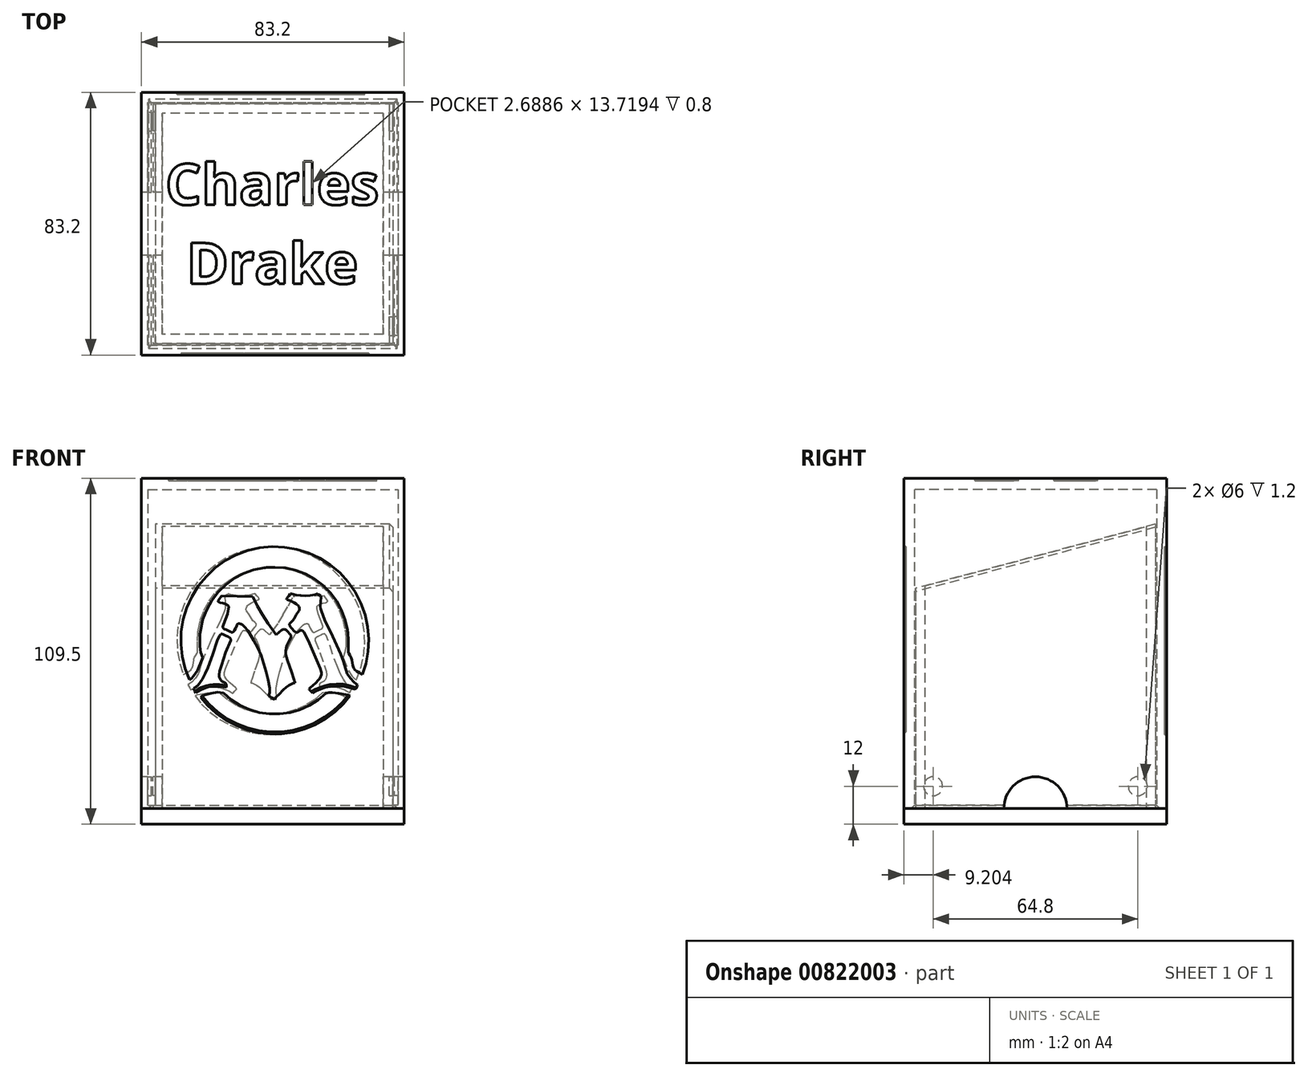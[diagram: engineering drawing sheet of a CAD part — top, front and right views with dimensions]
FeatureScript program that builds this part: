
annotation { "Feature Type Name" : "Feature", "Feature Type Description" : "" }
export const myFeature = defineFeature(function(context is Context, id is Id, definition is map)
    precondition{}
    {
        {
            var Q0;
            Q0=qCreatedBy(makeId("Top.planeOp"),FACE);
            var sketch = newSketch(context, id + "F0", { "sketchPlane" : qUnion([Q0])});
            skLineSegment(sketch, "E0.bottom", {"start": v(-37.57, 59.17) * mm, "end": v(32.43, 59.17) * mm});
            skLineSegment(sketch, "E0.top", {"start": v(-37.57, -10.83) * mm, "end": v(32.43, -10.83) * mm});
            skLineSegment(sketch, "E0.left", {"start": v(-37.57, 59.17) * mm, "end": v(-37.57, -10.83) * mm});
            skLineSegment(sketch, "E0.right", {"start": v(32.43, 59.17) * mm, "end": v(32.43, -10.83) * mm});
            skLineSegment(sketch, "E1.0", {"start": v(-40.57, 62.17) * mm, "end": v(35.43, 62.17) * mm});
            skLineSegment(sketch, "E1.1", {"start": v(-40.57, 62.17) * mm, "end": v(-40.57, -13.83) * mm});
            skLineSegment(sketch, "E1.2", {"start": v(-40.57, -13.83) * mm, "end": v(35.43, -13.83) * mm});
            skLineSegment(sketch, "E1.3", {"start": v(35.43, 62.17) * mm, "end": v(35.43, -13.83) * mm});
            skSolve(sketch);
        }
        {
            var Q0;
            Q0=makeQuery(id+"F0.imprint","IMPRINT",FACE,{"disambiguationData":[TD([[makeQuery(id+"F0.imprint","IMPRINT",EDGE,{"derivedFrom":sQuery(id+"F0.wireOp",EDGE,"E0.bottom")}),1.0]])]});
            extrude(context, id + "F1", {"entities" : qUnion([Q0]), "depth" : 101 * mm, "offsetDistance" : 25 * mm});
        }
        {
            var Q0;
            Q0=makeQuery(id+"F1.opExtrude","CAP_FACE",FACE,{"disambiguationData":[OSD([sQuery(id+"F0.wireOp",EDGE,"E0.bottom"),sQuery(id+"F0.wireOp",EDGE,"E0.top"),sQuery(id+"F0.wireOp",EDGE,"E0.left"),sQuery(id+"F0.wireOp",EDGE,"E0.right"),sQuery(id+"F0.wireOp",EDGE,"E1.0"),sQuery(id+"F0.wireOp",EDGE,"E1.1"),sQuery(id+"F0.wireOp",EDGE,"E1.2"),sQuery(id+"F0.wireOp",EDGE,"E1.3")])],"isStart":true});
            var sketch = newSketch(context, id + "F2", { "sketchPlane" : qUnion([Q0])});
            skLineSegment(sketch, "E2.0", {"start": v(-44.17, 17.43) * mm, "end": v(39.03, 17.43) * mm});
            skLineSegment(sketch, "E2.1", {"start": v(-44.17, -65.77) * mm, "end": v(-44.17, 17.43) * mm});
            skLineSegment(sketch, "E2.2", {"start": v(-44.17, -65.77) * mm, "end": v(39.03, -65.77) * mm});
            skLineSegment(sketch, "E2.3", {"start": v(39.03, -65.77) * mm, "end": v(39.03, 17.43) * mm});
            skSolve(sketch);
        }
        {
            var Q0;
            Q0=makeQuery(id+"F2.imprint","IMPRINT",FACE,{"disambiguationData":[TD([[makeQuery(id+"F2.imprint","IMPRINT",EDGE,{"derivedFrom":sQuery(id+"F2.wireOp",EDGE,"E2.0")}),-1.0]])]});
            var Q1;
            Q1=makeQuery(id+"F2.imprint","IMPRINT",FACE,{"disambiguationData":[TD([[makeQuery(id+"F2.imprint","IMPRINT",EDGE,{"derivedFrom":makeQuery(id+"F1.opExtrude","CAP_EDGE",EDGE,{"disambiguationData":[OSD([sQuery(id+"F0.wireOp",EDGE,"E0.bottom")])],"isStart":true})}),1.0]])]});
            var Q2;
            Q2=makeQuery(id+"F2.imprint","IMPRINT",FACE,{"disambiguationData":[TD([[makeQuery(id+"F2.imprint","IMPRINT",EDGE,{"derivedFrom":makeQuery(id+"F1.opExtrude","CAP_EDGE",EDGE,{"disambiguationData":[OSD([sQuery(id+"F0.wireOp",EDGE,"E0.bottom")])],"isStart":true})}),-1.0]])]});
            extrude(context, id + "F3", {"entities" : qUnion([Q0, Q1, Q2]), "operationType" : NewBodyOperationType.ADD, "depth" : 5 * mm, "offsetDistance" : 25 * mm});
        }
        {
            var Q0;
            Q0=makeQuery(id+"F1.opExtrude","SWEPT_FACE",FACE,{"disambiguationData":[OSD([sQuery(id+"F0.wireOp",EDGE,"E1.1")])]});
            var sketch = newSketch(context, id + "F4", { "sketchPlane" : qUnion([Q0])});
            skLineSegment(sketch, "E3", {"start": v(-62.17, 90) * mm, "end": v(13.83, 69.64) * mm});
            skSolve(sketch);
        }
        {
            var Q0;
            {var subQ0=sQuery(id+"F4.wireOp",EDGE,"E3");Q0=makeQuery(id+"F4.imprint","IMPRINT",FACE,{"disambiguationData":[TD([[makeQuery(id+"F4.imprint","IMPRINT",EDGE,{"derivedFrom":subQ0}),1.0]])]});}
            extrude(context, id + "F5", {"entities" : qUnion([Q0]), "operationType" : NewBodyOperationType.REMOVE, "endBound" : BoundingType.THROUGH_ALL, "oppositeDirection" : true, "depth" : 25 * mm, "offsetDistance" : 25 * mm});
        }
        {
            var Q0;
            {var subQ0=sQuery(id+"F2.wireOp",EDGE,"E2.3");var subQ1=sQuery(id+"F2.wireOp",EDGE,"E2.0");var subQ2=sQuery(id+"F2.wireOp",EDGE,"E2.1");var subQ3=sQuery(id+"F2.wireOp",EDGE,"E2.2");Q0=makeQuery(id+"F3.boolean.opBoolean","SPLIT",FACE,{"disambiguationData":[TD([makeQuery(id+"F1.opExtrude","SWEPT_FACE",FACE,{"disambiguationData":[OSD([sQuery(id+"F0.wireOp",EDGE,"E1.0")])]})])],"derivedFrom":makeQuery(id+"F3.opExtrude","CAP_FACE",FACE,{"disambiguationData":[OSD([subQ1,subQ2,subQ3,subQ0])],"isStart":true})});}
            var sketch = newSketch(context, id + "F6", { "sketchPlane" : qUnion([Q0])});
            skLineSegment(sketch, "E4.0", {"start": v(-44.17, 65.77) * mm, "end": v(-44.17, -17.43) * mm});
            skLineSegment(sketch, "E5.0", {"start": v(-44.17, -17.43) * mm, "end": v(39.03, -17.43) * mm});
            skLineSegment(sketch, "E6.0", {"start": v(39.03, 65.77) * mm, "end": v(39.03, -17.43) * mm});
            skLineSegment(sketch, "E7.0", {"start": v(-44.17, 65.77) * mm, "end": v(39.03, 65.77) * mm});
            skLineSegment(sketch, "E8.0", {"start": v(-40.97, 62.57) * mm, "end": v(35.83, 62.57) * mm});
            skLineSegment(sketch, "E8.1", {"start": v(-40.97, 62.57) * mm, "end": v(-40.97, -14.23) * mm});
            skLineSegment(sketch, "E8.2", {"start": v(-40.97, -14.23) * mm, "end": v(35.83, -14.23) * mm});
            skLineSegment(sketch, "E8.3", {"start": v(35.83, 62.57) * mm, "end": v(35.83, -14.23) * mm});
            skSolve(sketch);
        }
        {
            var Q0;
            Q0=makeQuery(id+"F6.imprint","IMPRINT",FACE,{"disambiguationData":[TD([[makeQuery(id+"F6.imprint","IMPRINT",EDGE,{"derivedFrom":sQuery(id+"F6.wireOp",EDGE,"E4.0")}),1.0]])]});
            extrude(context, id + "F7", {"entities" : qUnion([Q0]), "depth" : 101 * mm, "offsetDistance" : 25 * mm});
        }
        {
            var Q0;
            Q0=makeQuery(id+"F7.opExtrude","CAP_FACE",FACE,{"disambiguationData":[OSD([sQuery(id+"F6.wireOp",EDGE,"E4.0"),sQuery(id+"F6.wireOp",EDGE,"E5.0"),sQuery(id+"F6.wireOp",EDGE,"E6.0"),sQuery(id+"F6.wireOp",EDGE,"E7.0"),sQuery(id+"F6.wireOp",EDGE,"E8.0"),sQuery(id+"F6.wireOp",EDGE,"E8.1"),sQuery(id+"F6.wireOp",EDGE,"E8.2"),sQuery(id+"F6.wireOp",EDGE,"E8.3")])],"isStart":false});
            var sketch = newSketch(context, id + "F8", { "sketchPlane" : qUnion([Q0])});
            skSolve(sketch);
        }
        {
            var Q0;
            Q0=makeQuery(id+"F8.imprint","IMPRINT",FACE,{"disambiguationData":[TD([[makeQuery(id+"F8.imprint","IMPRINT",EDGE,{"derivedFrom":makeQuery(id+"F7.opExtrude","CAP_EDGE",EDGE,{"disambiguationData":[OSD([sQuery(id+"F6.wireOp",EDGE,"E4.0")])],"isStart":false})}),1.0]])]});
            var Q1;
            Q1=makeQuery(id+"F8.imprint","IMPRINT",FACE,{"disambiguationData":[TD([[makeQuery(id+"F8.imprint","IMPRINT",EDGE,{"derivedFrom":makeQuery(id+"F7.opExtrude","CAP_EDGE",EDGE,{"disambiguationData":[OSD([sQuery(id+"F6.wireOp",EDGE,"E8.0")])],"isStart":false})}),-1.0]])]});
            extrude(context, id + "F9", {"entities" : qUnion([Q0, Q1]), "operationType" : NewBodyOperationType.ADD, "depth" : 3.5 * mm, "offsetDistance" : 25 * mm});
        }
        {
            var Q0;
            Q0=makeQuery(id+"F9.opExtrude","CAP_FACE",FACE,{"disambiguationData":[OSD([sQuery(id+"F6.wireOp",EDGE,"E4.0"),sQuery(id+"F6.wireOp",EDGE,"E5.0"),sQuery(id+"F6.wireOp",EDGE,"E6.0"),sQuery(id+"F6.wireOp",EDGE,"E7.0")])],"isStart":false});
            var sketch = newSketch(context, id + "F10", { "sketchPlane" : qUnion([Q0])});
            skLineSegment(sketch, "E9", {"start": v(-2.57, 65.77) * mm, "end": v(-2.57, -17.43) * mm, "construction": true});
            skLineSegment(sketch, "E10", {"start": v(-44.17, 24.17) * mm, "end": v(39.03, 24.17) * mm, "construction": true});
            skText(sketch, "E11", { "text": "Charles", "fontName": "OpenSans-Bold.ttf"});
            skText(sketch, "E12", { "text": "Drake", "fontName": "OpenSans-Bold.ttf"});
            const initialGuessF10  = {"E11": [-0.03662, 0.03017, 1, 0, 0.013], "E12": [-0.02993, 0.00517, 1, 0, 0.013]};
            skSetInitialGuess(sketch, initialGuessF10);
            skSolve(sketch);
        }
        {
            var Q0;
            Q0 = qSketchRegion(id + "F10", true);
            extrude(context, id + "F11", {"entities" : qUnion([Q0]), "operationType" : NewBodyOperationType.REMOVE, "oppositeDirection" : true, "depth" : 0.8 * mm, "offsetDistance" : 25 * mm});
        }
        {
            var Q0;
            {var subQ0=sQuery(id+"F6.wireOp",EDGE,"E5.0");Q0=makeQuery(id+"F9.boolean.opBoolean","MERGE",FACE,{"derivedFrom":[makeQuery(id+"F7.opExtrude","SWEPT_FACE",FACE,{"disambiguationData":[OSD([subQ0])]}),makeQuery(id+"F9.opExtrude","SWEPT_FACE",FACE,{"disambiguationData":[OSD([subQ0])]})]});}
            var sketch = newSketch(context, id + "F12", { "sketchPlane" : qUnion([Q0])});
            skLineSegment(sketch, "E13", {"start": v(-6.68, 82.48) * mm, "end": v(-2.78, 82.85) * mm});
            skLineSegment(sketch, "E14", {"start": v(-10.5, 81.6) * mm, "end": v(-6.68, 82.48) * mm});
            skLineSegment(sketch, "E15", {"start": v(-14.17, 80.24) * mm, "end": v(-10.5, 81.6) * mm});
            skLineSegment(sketch, "E16", {"start": v(-17.63, 78.4) * mm, "end": v(-14.17, 80.24) * mm});
            skLineSegment(sketch, "E17", {"start": v(-20.82, 76.12) * mm, "end": v(-17.63, 78.4) * mm});
            skLineSegment(sketch, "E18", {"start": v(-23.68, 73.44) * mm, "end": v(-20.82, 76.12) * mm});
            skLineSegment(sketch, "E19", {"start": v(-26.17, 70.4) * mm, "end": v(-23.68, 73.44) * mm});
            skLineSegment(sketch, "E20", {"start": v(-28.23, 67.07) * mm, "end": v(-26.17, 70.4) * mm});
            skLineSegment(sketch, "E21", {"start": v(-29.84, 63.5) * mm, "end": v(-28.23, 67.07) * mm});
            skLineSegment(sketch, "E22", {"start": v(-30.96, 59.74) * mm, "end": v(-29.84, 63.5) * mm});
            skLineSegment(sketch, "E23", {"start": v(-31.58, 55.87) * mm, "end": v(-30.96, 59.74) * mm});
            skLineSegment(sketch, "E24", {"start": v(-31.69, 51.95) * mm, "end": v(-31.58, 55.87) * mm});
            skLineSegment(sketch, "E25", {"start": v(-31.28, 48.06) * mm, "end": v(-31.69, 51.95) * mm});
            skLineSegment(sketch, "E26", {"start": v(-30.36, 44.25) * mm, "end": v(-31.28, 48.06) * mm});
            skLineSegment(sketch, "E27", {"start": v(-29.02, 40.8) * mm, "end": v(-30.36, 44.25) * mm});
            skLineSegment(sketch, "E28", {"start": v(-28.74, 40.9) * mm, "end": v(-29.02, 40.8) * mm});
            skLineSegment(sketch, "E29", {"start": v(-28.52, 41) * mm, "end": v(-28.74, 40.9) * mm});
            skLineSegment(sketch, "E30", {"start": v(-28.34, 41.12) * mm, "end": v(-28.52, 41) * mm});
            skLineSegment(sketch, "E31", {"start": v(-27.64, 41.91) * mm, "end": v(-28.34, 41.12) * mm});
            skLineSegment(sketch, "E32", {"start": v(-26.45, 43.7) * mm, "end": v(-27.64, 41.91) * mm});
            skLineSegment(sketch, "E33", {"start": v(-24.83, 47.7) * mm, "end": v(-26.45, 43.7) * mm});
            skLineSegment(sketch, "E34", {"start": v(-25.38, 49.39) * mm, "end": v(-24.83, 47.7) * mm});
            skLineSegment(sketch, "E35", {"start": v(-25.68, 51.24) * mm, "end": v(-25.38, 49.39) * mm});
            skLineSegment(sketch, "E36", {"start": v(-25.7, 53.11) * mm, "end": v(-25.68, 51.24) * mm});
            skLineSegment(sketch, "E37", {"start": v(-25.7, 53.37) * mm, "end": v(-25.7, 53.11) * mm});
            skLineSegment(sketch, "E38", {"start": v(-25.7, 53.63) * mm, "end": v(-25.7, 53.37) * mm});
            skLineSegment(sketch, "E39", {"start": v(-25.68, 54.14) * mm, "end": v(-25.7, 53.63) * mm});
            skLineSegment(sketch, "E40", {"start": v(-25.61, 55.16) * mm, "end": v(-25.68, 54.14) * mm});
            skLineSegment(sketch, "E41", {"start": v(-25.46, 56.47) * mm, "end": v(-25.61, 55.16) * mm});
            skLineSegment(sketch, "E42", {"start": v(-24.73, 59.75) * mm, "end": v(-25.46, 56.47) * mm});
            skLineSegment(sketch, "E43", {"start": v(-23.54, 62.89) * mm, "end": v(-24.73, 59.75) * mm});
            skLineSegment(sketch, "E44", {"start": v(-21.9, 65.83) * mm, "end": v(-23.54, 62.89) * mm});
            skLineSegment(sketch, "E45", {"start": v(-19.86, 68.5) * mm, "end": v(-21.9, 65.83) * mm});
            skLineSegment(sketch, "E46", {"start": v(-17.46, 70.85) * mm, "end": v(-19.86, 68.5) * mm});
            skLineSegment(sketch, "E47", {"start": v(-14.75, 72.83) * mm, "end": v(-17.46, 70.85) * mm});
            skLineSegment(sketch, "E48", {"start": v(-11.77, 74.4) * mm, "end": v(-14.75, 72.83) * mm});
            skLineSegment(sketch, "E49", {"start": v(-8.6, 75.53) * mm, "end": v(-11.77, 74.4) * mm});
            skLineSegment(sketch, "E50", {"start": v(-5.32, 76.18) * mm, "end": v(-8.6, 75.53) * mm});
            skLineSegment(sketch, "E51", {"start": v(-5.23, 76.2) * mm, "end": v(-5.32, 76.18) * mm});
            skLineSegment(sketch, "E52", {"start": v(-5.14, 76.2) * mm, "end": v(-5.23, 76.2) * mm});
            skLineSegment(sketch, "E53", {"start": v(-4.98, 76.22) * mm, "end": v(-5.14, 76.2) * mm});
            skLineSegment(sketch, "E54", {"start": v(-4.64, 76.26) * mm, "end": v(-4.98, 76.22) * mm});
            skLineSegment(sketch, "E55", {"start": v(-1.95, 76.36) * mm, "end": v(-4.64, 76.26) * mm});
            skLineSegment(sketch, "E56", {"start": v(1.35, 76.13) * mm, "end": v(-1.95, 76.36) * mm});
            skLineSegment(sketch, "E57", {"start": v(4.6, 75.42) * mm, "end": v(1.35, 76.13) * mm});
            skLineSegment(sketch, "E58", {"start": v(7.7, 74.26) * mm, "end": v(4.6, 75.42) * mm});
            skLineSegment(sketch, "E59", {"start": v(10.61, 72.67) * mm, "end": v(7.7, 74.26) * mm});
            skLineSegment(sketch, "E60", {"start": v(13.27, 70.68) * mm, "end": v(10.61, 72.67) * mm});
            skLineSegment(sketch, "E61", {"start": v(15.61, 68.34) * mm, "end": v(13.27, 70.68) * mm});
            skLineSegment(sketch, "E62", {"start": v(17.6, 65.68) * mm, "end": v(15.61, 68.34) * mm});
            skLineSegment(sketch, "E63", {"start": v(19.2, 62.77) * mm, "end": v(17.6, 65.68) * mm});
            skLineSegment(sketch, "E64", {"start": v(20.35, 59.66) * mm, "end": v(19.2, 62.77) * mm});
            skLineSegment(sketch, "E65", {"start": v(21.05, 56.43) * mm, "end": v(20.35, 59.66) * mm});
            skLineSegment(sketch, "E66", {"start": v(21.07, 56.34) * mm, "end": v(21.05, 56.43) * mm});
            skLineSegment(sketch, "E67", {"start": v(21.08, 56.26) * mm, "end": v(21.07, 56.34) * mm});
            skLineSegment(sketch, "E68", {"start": v(21.1, 56.1) * mm, "end": v(21.08, 56.26) * mm});
            skLineSegment(sketch, "E69", {"start": v(21.14, 55.76) * mm, "end": v(21.1, 56.1) * mm});
            skLineSegment(sketch, "E70", {"start": v(21.3, 53.12) * mm, "end": v(21.14, 55.76) * mm});
            skLineSegment(sketch, "E71", {"start": v(21.28, 49.86) * mm, "end": v(21.3, 53.12) * mm});
            skLineSegment(sketch, "E72", {"start": v(21.31, 49.49) * mm, "end": v(21.28, 49.86) * mm});
            skLineSegment(sketch, "E73", {"start": v(21.41, 49.15) * mm, "end": v(21.31, 49.49) * mm});
            skLineSegment(sketch, "E74", {"start": v(21.8, 48.47) * mm, "end": v(21.41, 49.15) * mm});
            skLineSegment(sketch, "E75", {"start": v(22.25, 47.76) * mm, "end": v(21.8, 48.47) * mm});
            skLineSegment(sketch, "E76", {"start": v(22.4, 47.34) * mm, "end": v(22.25, 47.76) * mm});
            skLineSegment(sketch, "E77", {"start": v(22.48, 46.91) * mm, "end": v(22.4, 47.34) * mm});
            skLineSegment(sketch, "E78", {"start": v(22.7, 45.3) * mm, "end": v(22.48, 46.91) * mm});
            skLineSegment(sketch, "E79", {"start": v(22.95, 44.58) * mm, "end": v(22.7, 45.3) * mm});
            skLineSegment(sketch, "E80", {"start": v(23.14, 44.26) * mm, "end": v(22.95, 44.58) * mm});
            skLineSegment(sketch, "E81", {"start": v(23.36, 43.97) * mm, "end": v(23.14, 44.26) * mm});
            skLineSegment(sketch, "E82", {"start": v(23.94, 43.46) * mm, "end": v(23.36, 43.97) * mm});
            skLineSegment(sketch, "E83", {"start": v(24.62, 43.01) * mm, "end": v(23.94, 43.46) * mm});
            skLineSegment(sketch, "E84", {"start": v(25.76, 42.37) * mm, "end": v(24.62, 43.01) * mm});
            skLineSegment(sketch, "E85", {"start": v(26.88, 45.83) * mm, "end": v(25.76, 42.37) * mm});
            skLineSegment(sketch, "E86", {"start": v(27.6, 49.68) * mm, "end": v(26.88, 45.83) * mm});
            skLineSegment(sketch, "E87", {"start": v(27.79, 53.6) * mm, "end": v(27.6, 49.68) * mm});
            skLineSegment(sketch, "E88", {"start": v(27.46, 57.5) * mm, "end": v(27.79, 53.6) * mm});
            skLineSegment(sketch, "E89", {"start": v(26.63, 61.33) * mm, "end": v(27.46, 57.5) * mm});
            skLineSegment(sketch, "E90", {"start": v(25.3, 65.02) * mm, "end": v(26.63, 61.33) * mm});
            skLineSegment(sketch, "E91", {"start": v(23.5, 68.5) * mm, "end": v(25.3, 65.02) * mm});
            skLineSegment(sketch, "E92", {"start": v(21.26, 71.71) * mm, "end": v(23.5, 68.5) * mm});
            skLineSegment(sketch, "E93", {"start": v(18.61, 74.6) * mm, "end": v(21.26, 71.71) * mm});
            skLineSegment(sketch, "E94", {"start": v(15.6, 77.12) * mm, "end": v(18.61, 74.6) * mm});
            skLineSegment(sketch, "E95", {"start": v(12.3, 79.22) * mm, "end": v(15.6, 77.12) * mm});
            skLineSegment(sketch, "E96", {"start": v(8.74, 80.87) * mm, "end": v(12.3, 79.22) * mm});
            skLineSegment(sketch, "E97", {"start": v(5, 82.04) * mm, "end": v(8.74, 80.87) * mm});
            skLineSegment(sketch, "E98", {"start": v(1.14, 82.7) * mm, "end": v(5, 82.04) * mm});
            skLineSegment(sketch, "E99", {"start": v(-2.78, 82.85) * mm, "end": v(1.14, 82.7) * mm});
            skLineSegment(sketch, "E100", {"start": v(4.29, 40.3) * mm, "end": v(4.3, 40.25) * mm});
            skLineSegment(sketch, "E101", {"start": v(4.27, 40.35) * mm, "end": v(4.29, 40.3) * mm});
            skLineSegment(sketch, "E102", {"start": v(4.24, 40.46) * mm, "end": v(4.27, 40.35) * mm});
            skLineSegment(sketch, "E103", {"start": v(4.18, 40.67) * mm, "end": v(4.24, 40.46) * mm});
            skLineSegment(sketch, "E104", {"start": v(3.3, 43.43) * mm, "end": v(4.18, 40.67) * mm});
            skLineSegment(sketch, "E105", {"start": v(2.11, 46.57) * mm, "end": v(3.3, 43.43) * mm});
            skLineSegment(sketch, "E106", {"start": v(1.67, 48.21) * mm, "end": v(2.11, 46.57) * mm});
            skLineSegment(sketch, "E107", {"start": v(1.55, 49.08) * mm, "end": v(1.67, 48.21) * mm});
            skLineSegment(sketch, "E108", {"start": v(1.55, 49.95) * mm, "end": v(1.55, 49.08) * mm});
            skLineSegment(sketch, "E109", {"start": v(1.68, 50.82) * mm, "end": v(1.55, 49.95) * mm});
            skLineSegment(sketch, "E110", {"start": v(1.93, 51.65) * mm, "end": v(1.68, 50.82) * mm});
            skLineSegment(sketch, "E111", {"start": v(2.6, 53.23) * mm, "end": v(1.93, 51.65) * mm});
            skLineSegment(sketch, "E112", {"start": v(3.2, 54.07) * mm, "end": v(2.6, 53.23) * mm});
            skLineSegment(sketch, "E113", {"start": v(3.21, 54.13) * mm, "end": v(3.2, 54.07) * mm});
            skLineSegment(sketch, "E114", {"start": v(3.22, 54.2) * mm, "end": v(3.21, 54.13) * mm});
            skLineSegment(sketch, "E115", {"start": v(3.2, 54.43) * mm, "end": v(3.22, 54.2) * mm});
            skLineSegment(sketch, "E116", {"start": v(3.17, 54.67) * mm, "end": v(3.2, 54.43) * mm});
            skLineSegment(sketch, "E117", {"start": v(3.14, 54.76) * mm, "end": v(3.17, 54.67) * mm});
            skLineSegment(sketch, "E118", {"start": v(3.12, 54.8) * mm, "end": v(3.14, 54.76) * mm});
            skLineSegment(sketch, "E119", {"start": v(1.79, 56.34) * mm, "end": v(3.12, 54.8) * mm});
            skLineSegment(sketch, "E120", {"start": v(1.62, 56.49) * mm, "end": v(1.79, 56.34) * mm});
            skLineSegment(sketch, "E121", {"start": v(1.45, 56.6) * mm, "end": v(1.62, 56.49) * mm});
            skLineSegment(sketch, "E122", {"start": v(1.26, 56.67) * mm, "end": v(1.45, 56.6) * mm});
            skLineSegment(sketch, "E123", {"start": v(1.07, 56.7) * mm, "end": v(1.26, 56.67) * mm});
            skLineSegment(sketch, "E124", {"start": v(0.6, 56.63) * mm, "end": v(1.07, 56.7) * mm});
            skLineSegment(sketch, "E125", {"start": v(0.4, 56.57) * mm, "end": v(0.6, 56.63) * mm});
            skLineSegment(sketch, "E126", {"start": v(0.22, 56.47) * mm, "end": v(0.4, 56.57) * mm});
            skLineSegment(sketch, "E127", {"start": v(-1.5, 54.94) * mm, "end": v(0.22, 56.47) * mm});
            skLineSegment(sketch, "E128", {"start": v(-2.16, 55.83) * mm, "end": v(-1.5, 54.94) * mm});
            skLineSegment(sketch, "E129", {"start": v(-4.07, 58.52) * mm, "end": v(-2.16, 55.83) * mm});
            skLineSegment(sketch, "E130", {"start": v(-5.83, 61.31) * mm, "end": v(-4.07, 58.52) * mm});
            skLineSegment(sketch, "E131", {"start": v(-5.83, 61.31) * mm, "end": v(-7.5, 64.16) * mm});
            skLineSegment(sketch, "E132", {"start": v(-7.5, 64.16) * mm, "end": v(-8.91, 66.97) * mm});
            skLineSegment(sketch, "E133", {"start": v(-18.83, 67.26) * mm, "end": v(-8.91, 66.97) * mm});
            skLineSegment(sketch, "E134", {"start": v(-19.75, 65.97) * mm, "end": v(-18.83, 67.26) * mm});
            skLineSegment(sketch, "E135", {"start": v(-19.99, 65.62) * mm, "end": v(-19.75, 65.97) * mm});
            skLineSegment(sketch, "E136", {"start": v(-19.92, 65.55) * mm, "end": v(-19.99, 65.62) * mm});
            skLineSegment(sketch, "E137", {"start": v(-19.62, 65.28) * mm, "end": v(-19.92, 65.55) * mm});
            skLineSegment(sketch, "E138", {"start": v(-19.48, 65.2) * mm, "end": v(-19.62, 65.28) * mm});
            skLineSegment(sketch, "E139", {"start": v(-19.33, 65.14) * mm, "end": v(-19.48, 65.2) * mm});
            skLineSegment(sketch, "E140", {"start": v(-18.48, 65.04) * mm, "end": v(-19.33, 65.14) * mm});
            skLineSegment(sketch, "E141", {"start": v(-17.64, 64.74) * mm, "end": v(-18.48, 65.04) * mm});
            skLineSegment(sketch, "E142", {"start": v(-17.21, 64.54) * mm, "end": v(-17.64, 64.74) * mm});
            skLineSegment(sketch, "E143", {"start": v(-16.98, 64.42) * mm, "end": v(-17.21, 64.54) * mm});
            skLineSegment(sketch, "E144", {"start": v(-16.77, 64.26) * mm, "end": v(-16.98, 64.42) * mm});
            skLineSegment(sketch, "E145", {"start": v(-16.67, 64.14) * mm, "end": v(-16.77, 64.26) * mm});
            skLineSegment(sketch, "E146", {"start": v(-16.6, 64) * mm, "end": v(-16.67, 64.14) * mm});
            skLineSegment(sketch, "E147", {"start": v(-16.56, 63.86) * mm, "end": v(-16.6, 64) * mm});
            skLineSegment(sketch, "E148", {"start": v(-16.54, 63.7) * mm, "end": v(-16.56, 63.86) * mm});
            skLineSegment(sketch, "E149", {"start": v(-16.58, 63.22) * mm, "end": v(-16.54, 63.7) * mm});
            skLineSegment(sketch, "E150", {"start": v(-16.95, 61.52) * mm, "end": v(-16.58, 63.22) * mm});
            skLineSegment(sketch, "E151", {"start": v(-17.58, 59.88) * mm, "end": v(-16.95, 61.52) * mm});
            skLineSegment(sketch, "E152", {"start": v(-18.2, 58.29) * mm, "end": v(-17.58, 59.88) * mm});
            skLineSegment(sketch, "E153", {"start": v(-18.33, 57.88) * mm, "end": v(-18.2, 58.29) * mm});
            skLineSegment(sketch, "E154", {"start": v(-18.41, 57.5) * mm, "end": v(-18.33, 57.88) * mm});
            skLineSegment(sketch, "E155", {"start": v(-18.4, 57.35) * mm, "end": v(-18.41, 57.5) * mm});
            skLineSegment(sketch, "E156", {"start": v(-18.36, 57.2) * mm, "end": v(-18.4, 57.35) * mm});
            skLineSegment(sketch, "E157", {"start": v(-18.28, 57.07) * mm, "end": v(-18.36, 57.2) * mm});
            skLineSegment(sketch, "E158", {"start": v(-18.17, 56.94) * mm, "end": v(-18.28, 57.07) * mm});
            skLineSegment(sketch, "E159", {"start": v(-18.03, 56.84) * mm, "end": v(-18.17, 56.94) * mm});
            skLineSegment(sketch, "E160", {"start": v(-17.86, 56.76) * mm, "end": v(-18.03, 56.84) * mm});
            skLineSegment(sketch, "E161", {"start": v(-17.46, 56.6) * mm, "end": v(-17.86, 56.76) * mm});
            skLineSegment(sketch, "E162", {"start": v(-16.68, 56.25) * mm, "end": v(-17.46, 56.6) * mm});
            skLineSegment(sketch, "E163", {"start": v(-15.89, 55.84) * mm, "end": v(-16.68, 56.25) * mm});
            skLineSegment(sketch, "E164", {"start": v(-15.72, 55.78) * mm, "end": v(-15.89, 55.84) * mm});
            skLineSegment(sketch, "E165", {"start": v(-15.55, 55.74) * mm, "end": v(-15.72, 55.78) * mm});
            skLineSegment(sketch, "E166", {"start": v(-15.49, 55.74) * mm, "end": v(-15.55, 55.74) * mm});
            skLineSegment(sketch, "E167", {"start": v(-15.43, 55.75) * mm, "end": v(-15.49, 55.74) * mm});
            skLineSegment(sketch, "E168", {"start": v(-15.28, 55.8) * mm, "end": v(-15.43, 55.75) * mm});
            skLineSegment(sketch, "E169", {"start": v(-15.13, 55.89) * mm, "end": v(-15.28, 55.8) * mm});
            skLineSegment(sketch, "E170", {"start": v(-15, 56) * mm, "end": v(-15.13, 55.89) * mm});
            skLineSegment(sketch, "E171", {"start": v(-14.76, 56.31) * mm, "end": v(-15, 56) * mm});
            skLineSegment(sketch, "E172", {"start": v(-14.38, 57.05) * mm, "end": v(-14.76, 56.31) * mm});
            skLineSegment(sketch, "E173", {"start": v(-14.02, 57.88) * mm, "end": v(-14.38, 57.05) * mm});
            skLineSegment(sketch, "E174", {"start": v(-13.92, 58.1) * mm, "end": v(-14.02, 57.88) * mm});
            skLineSegment(sketch, "E175", {"start": v(-13.84, 58.22) * mm, "end": v(-13.92, 58.1) * mm});
            skLineSegment(sketch, "E176", {"start": v(-13.74, 58.33) * mm, "end": v(-13.84, 58.22) * mm});
            skLineSegment(sketch, "E177", {"start": v(-13.61, 58.42) * mm, "end": v(-13.74, 58.33) * mm});
            skLineSegment(sketch, "E178", {"start": v(-13.46, 58.47) * mm, "end": v(-13.61, 58.42) * mm});
            skLineSegment(sketch, "E179", {"start": v(-13.3, 58.49) * mm, "end": v(-13.46, 58.47) * mm});
            skLineSegment(sketch, "E180", {"start": v(-13.16, 58.48) * mm, "end": v(-13.3, 58.49) * mm});
            skLineSegment(sketch, "E181", {"start": v(-12.9, 58.43) * mm, "end": v(-13.16, 58.48) * mm});
            skLineSegment(sketch, "E182", {"start": v(-12.65, 58.33) * mm, "end": v(-12.9, 58.43) * mm});
            skLineSegment(sketch, "E183", {"start": v(-12.26, 58.09) * mm, "end": v(-12.65, 58.33) * mm});
            skLineSegment(sketch, "E184", {"start": v(-12.26, 58.09) * mm, "end": v(-11.56, 57.53) * mm});
            skLineSegment(sketch, "E185", {"start": v(-11.56, 57.53) * mm, "end": v(-10.37, 56.22) * mm});
            skLineSegment(sketch, "E186", {"start": v(-8.6, 53.23) * mm, "end": v(-10.37, 56.22) * mm});
            skLineSegment(sketch, "E187", {"start": v(-7.35, 50.86) * mm, "end": v(-8.6, 53.23) * mm});
            skLineSegment(sketch, "E188", {"start": v(-6.25, 48.4) * mm, "end": v(-7.35, 50.86) * mm});
            skLineSegment(sketch, "E189", {"start": v(-4.75, 43.27) * mm, "end": v(-6.25, 48.4) * mm});
            skLineSegment(sketch, "E190", {"start": v(-4.11, 40.68) * mm, "end": v(-4.75, 43.27) * mm});
            skLineSegment(sketch, "E191", {"start": v(-3.6, 38.02) * mm, "end": v(-4.11, 40.68) * mm});
            skLineSegment(sketch, "E192", {"start": v(-3.55, 37.32) * mm, "end": v(-3.6, 38.02) * mm});
            skLineSegment(sketch, "E193", {"start": v(-3.62, 36.62) * mm, "end": v(-3.55, 37.32) * mm});
            skLineSegment(sketch, "E194", {"start": v(-3.79, 35.94) * mm, "end": v(-3.62, 36.62) * mm});
            skLineSegment(sketch, "E195", {"start": v(-3.85, 35.76) * mm, "end": v(-3.79, 35.94) * mm});
            skLineSegment(sketch, "E196", {"start": v(-3.94, 35.6) * mm, "end": v(-3.85, 35.76) * mm});
            skLineSegment(sketch, "E197", {"start": v(-3.97, 35.54) * mm, "end": v(-3.94, 35.6) * mm});
            skLineSegment(sketch, "E198", {"start": v(-3.85, 35.51) * mm, "end": v(-3.97, 35.54) * mm});
            skLineSegment(sketch, "E199", {"start": v(-3.49, 35.36) * mm, "end": v(-3.85, 35.51) * mm});
            skLineSegment(sketch, "E200", {"start": v(-2.92, 35.01) * mm, "end": v(-3.49, 35.36) * mm});
            skLineSegment(sketch, "E201", {"start": v(-2.35, 34.67) * mm, "end": v(-2.92, 35.01) * mm});
            skLineSegment(sketch, "E202", {"start": v(-2.05, 34.46) * mm, "end": v(-2.35, 34.67) * mm});
            skLineSegment(sketch, "E203", {"start": v(-1.94, 34.34) * mm, "end": v(-2.05, 34.46) * mm});
            skLineSegment(sketch, "E204", {"start": v(-1.79, 34.73) * mm, "end": v(-1.94, 34.34) * mm});
            skLineSegment(sketch, "E205", {"start": v(-1.48, 35.22) * mm, "end": v(-1.79, 34.73) * mm});
            skLineSegment(sketch, "E206", {"start": v(-0.7, 36.02) * mm, "end": v(-1.48, 35.22) * mm});
            skLineSegment(sketch, "E207", {"start": v(0.82, 37.56) * mm, "end": v(-0.7, 36.02) * mm});
            skLineSegment(sketch, "E208", {"start": v(1.62, 38.33) * mm, "end": v(0.82, 37.56) * mm});
            skLineSegment(sketch, "E209", {"start": v(2.54, 38.92) * mm, "end": v(1.62, 38.33) * mm});
            skLineSegment(sketch, "E210", {"start": v(3.5, 39.5) * mm, "end": v(2.54, 38.92) * mm});
            skLineSegment(sketch, "E211", {"start": v(3.76, 39.63) * mm, "end": v(3.5, 39.5) * mm});
            skLineSegment(sketch, "E212", {"start": v(4.05, 39.73) * mm, "end": v(3.76, 39.63) * mm});
            skLineSegment(sketch, "E213", {"start": v(4.36, 39.77) * mm, "end": v(4.05, 39.73) * mm});
            skLineSegment(sketch, "E214", {"start": v(4.4, 39.77) * mm, "end": v(4.36, 39.77) * mm});
            skLineSegment(sketch, "E215", {"start": v(4.4, 39.89) * mm, "end": v(4.4, 39.77) * mm});
            skLineSegment(sketch, "E216", {"start": v(4.3, 40.25) * mm, "end": v(4.4, 39.89) * mm});
            skLineSegment(sketch, "E217", {"start": v(16.41, 54.4) * mm, "end": v(17.06, 53) * mm});
            skLineSegment(sketch, "E218", {"start": v(13.86, 59.7) * mm, "end": v(16.41, 54.4) * mm});
            skLineSegment(sketch, "E219", {"start": v(12.79, 62.44) * mm, "end": v(13.86, 59.7) * mm});
            skLineSegment(sketch, "E220", {"start": v(12.57, 63.17) * mm, "end": v(12.79, 62.44) * mm});
            skLineSegment(sketch, "E221", {"start": v(12.5, 63.94) * mm, "end": v(12.57, 63.17) * mm});
            skLineSegment(sketch, "E222", {"start": v(12.56, 65.43) * mm, "end": v(12.5, 63.94) * mm});
            skLineSegment(sketch, "E223", {"start": v(12.7, 66.88) * mm, "end": v(12.56, 65.43) * mm});
            skLineSegment(sketch, "E224", {"start": v(12.7, 67.05) * mm, "end": v(12.7, 66.88) * mm});
            skLineSegment(sketch, "E225", {"start": v(12.67, 67.2) * mm, "end": v(12.7, 67.05) * mm});
            skLineSegment(sketch, "E226", {"start": v(12.65, 67.25) * mm, "end": v(12.67, 67.2) * mm});
            skLineSegment(sketch, "E227", {"start": v(12.62, 67.28) * mm, "end": v(12.65, 67.25) * mm});
            skLineSegment(sketch, "E228", {"start": v(12.57, 67.31) * mm, "end": v(12.62, 67.28) * mm});
            skLineSegment(sketch, "E229", {"start": v(11.93, 67.66) * mm, "end": v(12.57, 67.31) * mm});
            skLineSegment(sketch, "E230", {"start": v(11.63, 67.85) * mm, "end": v(11.93, 67.66) * mm});
            skLineSegment(sketch, "E231", {"start": v(11.58, 67.87) * mm, "end": v(11.63, 67.85) * mm});
            skLineSegment(sketch, "E232", {"start": v(11.54, 67.88) * mm, "end": v(11.58, 67.87) * mm});
            skLineSegment(sketch, "E233", {"start": v(11.5, 67.88) * mm, "end": v(11.54, 67.88) * mm});
            skLineSegment(sketch, "E234", {"start": v(11.45, 67.88) * mm, "end": v(11.5, 67.88) * mm});
            skLineSegment(sketch, "E235", {"start": v(10.74, 67.63) * mm, "end": v(11.45, 67.88) * mm});
            skLineSegment(sketch, "E236", {"start": v(9.28, 67.35) * mm, "end": v(10.74, 67.63) * mm});
            skLineSegment(sketch, "E237", {"start": v(7.79, 67.26) * mm, "end": v(9.28, 67.35) * mm});
            skLineSegment(sketch, "E238", {"start": v(6.3, 67.4) * mm, "end": v(7.79, 67.26) * mm});
            skLineSegment(sketch, "E239", {"start": v(4.82, 67.53) * mm, "end": v(6.3, 67.4) * mm});
            skLineSegment(sketch, "E240", {"start": v(3.4, 67.94) * mm, "end": v(4.82, 67.53) * mm});
            skLineSegment(sketch, "E241", {"start": v(3.26, 67.97) * mm, "end": v(3.4, 67.94) * mm});
            skLineSegment(sketch, "E242", {"start": v(3.13, 67.97) * mm, "end": v(3.26, 67.97) * mm});
            skLineSegment(sketch, "E243", {"start": v(3.1, 67.96) * mm, "end": v(3.13, 67.97) * mm});
            skLineSegment(sketch, "E244", {"start": v(3.06, 67.95) * mm, "end": v(3.1, 67.96) * mm});
            skLineSegment(sketch, "E245", {"start": v(2.95, 67.87) * mm, "end": v(3.06, 67.95) * mm});
            skLineSegment(sketch, "E246", {"start": v(2.47, 67.34) * mm, "end": v(2.95, 67.87) * mm});
            skLineSegment(sketch, "E247", {"start": v(2.02, 66.8) * mm, "end": v(2.47, 67.34) * mm});
            skLineSegment(sketch, "E248", {"start": v(1.84, 66.52) * mm, "end": v(2.02, 66.8) * mm});
            skLineSegment(sketch, "E249", {"start": v(1.8, 66.4) * mm, "end": v(1.84, 66.52) * mm});
            skLineSegment(sketch, "E250", {"start": v(1.77, 66.25) * mm, "end": v(1.8, 66.4) * mm});
            skLineSegment(sketch, "E251", {"start": v(1.77, 66.2) * mm, "end": v(1.77, 66.25) * mm});
            skLineSegment(sketch, "E252", {"start": v(1.8, 66.18) * mm, "end": v(1.77, 66.2) * mm});
            skLineSegment(sketch, "E253", {"start": v(1.93, 66.11) * mm, "end": v(1.8, 66.18) * mm});
            skLineSegment(sketch, "E254", {"start": v(2.11, 66.05) * mm, "end": v(1.93, 66.11) * mm});
            skLineSegment(sketch, "E255", {"start": v(2.87, 65.76) * mm, "end": v(2.11, 66.05) * mm});
            skLineSegment(sketch, "E256", {"start": v(4.15, 65.08) * mm, "end": v(2.87, 65.76) * mm});
            skLineSegment(sketch, "E257", {"start": v(4.78, 64.7) * mm, "end": v(4.15, 65.08) * mm});
            skLineSegment(sketch, "E258", {"start": v(5.1, 64.48) * mm, "end": v(4.78, 64.7) * mm});
            skLineSegment(sketch, "E259", {"start": v(5.4, 64.2) * mm, "end": v(5.1, 64.48) * mm});
            skLineSegment(sketch, "E260", {"start": v(5.65, 63.87) * mm, "end": v(5.4, 64.2) * mm});
            skLineSegment(sketch, "E261", {"start": v(5.82, 63.48) * mm, "end": v(5.65, 63.87) * mm});
            skLineSegment(sketch, "E262", {"start": v(5.88, 63.26) * mm, "end": v(5.82, 63.48) * mm});
            skLineSegment(sketch, "E263", {"start": v(5.9, 63.03) * mm, "end": v(5.88, 63.26) * mm});
            skLineSegment(sketch, "E264", {"start": v(5.86, 62.8) * mm, "end": v(5.9, 63.03) * mm});
            skLineSegment(sketch, "E265", {"start": v(5.78, 62.58) * mm, "end": v(5.86, 62.8) * mm});
            skLineSegment(sketch, "E266", {"start": v(4.88, 61.35) * mm, "end": v(5.78, 62.58) * mm});
            skLineSegment(sketch, "E267", {"start": v(4.17, 60.09) * mm, "end": v(4.88, 61.35) * mm});
            skLineSegment(sketch, "E268", {"start": v(3.72, 59.45) * mm, "end": v(4.17, 60.09) * mm});
            skLineSegment(sketch, "E269", {"start": v(3.15, 58.9) * mm, "end": v(3.72, 59.45) * mm});
            skLineSegment(sketch, "E270", {"start": v(2.88, 58.66) * mm, "end": v(3.15, 58.9) * mm});
            skLineSegment(sketch, "E271", {"start": v(2.78, 58.55) * mm, "end": v(2.88, 58.66) * mm});
            skLineSegment(sketch, "E272", {"start": v(2.72, 58.44) * mm, "end": v(2.78, 58.55) * mm});
            skLineSegment(sketch, "E273", {"start": v(2.68, 58.33) * mm, "end": v(2.72, 58.44) * mm});
            skLineSegment(sketch, "E274", {"start": v(2.67, 58.2) * mm, "end": v(2.68, 58.33) * mm});
            skLineSegment(sketch, "E275", {"start": v(2.69, 58.06) * mm, "end": v(2.67, 58.2) * mm});
            skLineSegment(sketch, "E276", {"start": v(2.73, 57.93) * mm, "end": v(2.69, 58.06) * mm});
            skLineSegment(sketch, "E277", {"start": v(2.88, 57.65) * mm, "end": v(2.73, 57.93) * mm});
            skLineSegment(sketch, "E278", {"start": v(3.08, 57.37) * mm, "end": v(2.88, 57.65) * mm});
            skLineSegment(sketch, "E279", {"start": v(3.54, 56.82) * mm, "end": v(3.08, 57.37) * mm});
            skLineSegment(sketch, "E280", {"start": v(4.03, 56.28) * mm, "end": v(3.54, 56.82) * mm});
            skLineSegment(sketch, "E281", {"start": v(4.28, 56.02) * mm, "end": v(4.03, 56.28) * mm});
            skLineSegment(sketch, "E282", {"start": v(4.4, 55.93) * mm, "end": v(4.28, 56.02) * mm});
            skLineSegment(sketch, "E283", {"start": v(4.51, 55.86) * mm, "end": v(4.4, 55.93) * mm});
            skLineSegment(sketch, "E284", {"start": v(4.64, 55.8) * mm, "end": v(4.51, 55.86) * mm});
            skLineSegment(sketch, "E285", {"start": v(4.8, 55.77) * mm, "end": v(4.64, 55.8) * mm});
            skLineSegment(sketch, "E286", {"start": v(5.14, 55.73) * mm, "end": v(4.8, 55.77) * mm});
            skLineSegment(sketch, "E287", {"start": v(5.19, 55.73) * mm, "end": v(5.14, 55.73) * mm});
            skLineSegment(sketch, "E288", {"start": v(5.24, 55.74) * mm, "end": v(5.19, 55.73) * mm});
            skLineSegment(sketch, "E289", {"start": v(5.28, 55.76) * mm, "end": v(5.24, 55.74) * mm});
            skLineSegment(sketch, "E290", {"start": v(5.32, 55.78) * mm, "end": v(5.28, 55.76) * mm});
            skLineSegment(sketch, "E291", {"start": v(5.6, 56.02) * mm, "end": v(5.32, 55.78) * mm});
            skLineSegment(sketch, "E292", {"start": v(5.94, 56.24) * mm, "end": v(5.6, 56.02) * mm});
            skLineSegment(sketch, "E293", {"start": v(6.16, 56.33) * mm, "end": v(5.94, 56.24) * mm});
            skLineSegment(sketch, "E294", {"start": v(6.28, 56.36) * mm, "end": v(6.16, 56.33) * mm});
            skLineSegment(sketch, "E295", {"start": v(6.42, 56.36) * mm, "end": v(6.28, 56.36) * mm});
            skLineSegment(sketch, "E296", {"start": v(6.55, 56.35) * mm, "end": v(6.42, 56.36) * mm});
            skLineSegment(sketch, "E297", {"start": v(6.69, 56.3) * mm, "end": v(6.55, 56.35) * mm});
            skLineSegment(sketch, "E298", {"start": v(6.9, 56.2) * mm, "end": v(6.69, 56.3) * mm});
            skLineSegment(sketch, "E299", {"start": v(7.07, 56.04) * mm, "end": v(6.9, 56.2) * mm});
            skLineSegment(sketch, "E300", {"start": v(7.22, 55.86) * mm, "end": v(7.07, 56.04) * mm});
            skLineSegment(sketch, "E301", {"start": v(8.57, 53.22) * mm, "end": v(7.22, 55.86) * mm});
            skLineSegment(sketch, "E302", {"start": v(12.44, 44.28) * mm, "end": v(8.57, 53.22) * mm});
            skLineSegment(sketch, "E303", {"start": v(12.8, 43.07) * mm, "end": v(12.44, 44.28) * mm});
            skLineSegment(sketch, "E304", {"start": v(12.83, 42.72) * mm, "end": v(12.8, 43.07) * mm});
            skLineSegment(sketch, "E305", {"start": v(12.8, 42.38) * mm, "end": v(12.83, 42.72) * mm});
            skLineSegment(sketch, "E306", {"start": v(12.72, 42.05) * mm, "end": v(12.8, 42.38) * mm});
            skLineSegment(sketch, "E307", {"start": v(12.6, 41.73) * mm, "end": v(12.72, 42.05) * mm});
            skLineSegment(sketch, "E308", {"start": v(12.27, 41.17) * mm, "end": v(12.6, 41.73) * mm});
            skLineSegment(sketch, "E309", {"start": v(11.87, 40.66) * mm, "end": v(12.27, 41.17) * mm});
            skLineSegment(sketch, "E310", {"start": v(10.98, 39.78) * mm, "end": v(11.87, 40.66) * mm});
            skLineSegment(sketch, "E311", {"start": v(9.21, 38.17) * mm, "end": v(10.98, 39.78) * mm});
            skLineSegment(sketch, "E312", {"start": v(9, 37.95) * mm, "end": v(9.21, 38.17) * mm});
            skLineSegment(sketch, "E313", {"start": v(8.9, 37.83) * mm, "end": v(9, 37.95) * mm});
            skLineSegment(sketch, "E314", {"start": v(8.86, 37.77) * mm, "end": v(8.9, 37.83) * mm});
            skLineSegment(sketch, "E315", {"start": v(9.08, 37.55) * mm, "end": v(8.86, 37.77) * mm});
            skLineSegment(sketch, "E316", {"start": v(9.56, 37.07) * mm, "end": v(9.08, 37.55) * mm});
            skLineSegment(sketch, "E317", {"start": v(9.89, 36.62) * mm, "end": v(9.56, 37.07) * mm});
            skLineSegment(sketch, "E318", {"start": v(10.15, 36.42) * mm, "end": v(9.89, 36.62) * mm});
            skLineSegment(sketch, "E319", {"start": v(11.28, 37.12) * mm, "end": v(10.15, 36.42) * mm});
            skLineSegment(sketch, "E320", {"start": v(12.67, 37.7) * mm, "end": v(11.28, 37.12) * mm});
            skLineSegment(sketch, "E321", {"start": v(14.1, 38.19) * mm, "end": v(12.67, 37.7) * mm});
            skLineSegment(sketch, "E322", {"start": v(15.57, 38.5) * mm, "end": v(14.1, 38.19) * mm});
            skLineSegment(sketch, "E323", {"start": v(17.6, 38.66) * mm, "end": v(15.57, 38.5) * mm});
            skLineSegment(sketch, "E324", {"start": v(19.66, 38.64) * mm, "end": v(17.6, 38.66) * mm});
            skLineSegment(sketch, "E325", {"start": v(21.67, 38.16) * mm, "end": v(19.66, 38.64) * mm});
            skLineSegment(sketch, "E326", {"start": v(23.39, 37.54) * mm, "end": v(21.67, 38.16) * mm});
            skLineSegment(sketch, "E327", {"start": v(23.68, 38.03) * mm, "end": v(23.39, 37.54) * mm});
            skLineSegment(sketch, "E328", {"start": v(24.06, 38.7) * mm, "end": v(23.68, 38.03) * mm});
            skLineSegment(sketch, "E329", {"start": v(24.3, 39.15) * mm, "end": v(24.06, 38.7) * mm});
            skLineSegment(sketch, "E330", {"start": v(23.77, 39.42) * mm, "end": v(24.3, 39.15) * mm});
            skLineSegment(sketch, "E331", {"start": v(23.08, 39.98) * mm, "end": v(23.77, 39.42) * mm});
            skLineSegment(sketch, "E332", {"start": v(21.98, 41.3) * mm, "end": v(23.08, 39.98) * mm});
            skLineSegment(sketch, "E333", {"start": v(21, 42.7) * mm, "end": v(21.98, 41.3) * mm});
            skLineSegment(sketch, "E334", {"start": v(20.68, 43.52) * mm, "end": v(21, 42.7) * mm});
            skLineSegment(sketch, "E335", {"start": v(20.5, 44.35) * mm, "end": v(20.68, 43.52) * mm});
            skLineSegment(sketch, "E336", {"start": v(19.84, 46.43) * mm, "end": v(20.5, 44.35) * mm});
            skLineSegment(sketch, "E337", {"start": v(18.91, 48.82) * mm, "end": v(19.84, 46.43) * mm});
            skLineSegment(sketch, "E338", {"start": v(17.06, 53) * mm, "end": v(18.91, 48.82) * mm});
            skLineSegment(sketch, "E339", {"start": v(-27.6, 38.1) * mm, "end": v(-27.47, 38.14) * mm});
            skLineSegment(sketch, "E340", {"start": v(-27.65, 38.08) * mm, "end": v(-27.6, 38.1) * mm});
            skLineSegment(sketch, "E341", {"start": v(-27.27, 37.13) * mm, "end": v(-27.65, 38.08) * mm});
            skLineSegment(sketch, "E342", {"start": v(-26.82, 36.5) * mm, "end": v(-27.27, 37.13) * mm});
            skLineSegment(sketch, "E343", {"start": v(-26.54, 36.74) * mm, "end": v(-26.82, 36.5) * mm});
            skLineSegment(sketch, "E344", {"start": v(-26.11, 37.01) * mm, "end": v(-26.54, 36.74) * mm});
            skLineSegment(sketch, "E345", {"start": v(-25.26, 37.53) * mm, "end": v(-26.11, 37.01) * mm});
            skLineSegment(sketch, "E346", {"start": v(-23.4, 38.21) * mm, "end": v(-25.26, 37.53) * mm});
            skLineSegment(sketch, "E347", {"start": v(-22.42, 38.42) * mm, "end": v(-23.4, 38.21) * mm});
            skLineSegment(sketch, "E348", {"start": v(-21.43, 38.48) * mm, "end": v(-22.42, 38.42) * mm});
            skLineSegment(sketch, "E349", {"start": v(-19.47, 38.47) * mm, "end": v(-21.43, 38.48) * mm});
            skLineSegment(sketch, "E350", {"start": v(-17.3, 38.28) * mm, "end": v(-19.47, 38.47) * mm});
            skLineSegment(sketch, "E351", {"start": v(-17.3, 39.04) * mm, "end": v(-17.3, 38.28) * mm});
            skLineSegment(sketch, "E352", {"start": v(-17.33, 39.27) * mm, "end": v(-17.3, 39.04) * mm});
            skLineSegment(sketch, "E353", {"start": v(-17.36, 39.35) * mm, "end": v(-17.33, 39.27) * mm});
            skLineSegment(sketch, "E354", {"start": v(-17.4, 39.42) * mm, "end": v(-17.36, 39.35) * mm});
            skLineSegment(sketch, "E355", {"start": v(-17.45, 39.49) * mm, "end": v(-17.4, 39.42) * mm});
            skLineSegment(sketch, "E356", {"start": v(-17.52, 39.55) * mm, "end": v(-17.45, 39.49) * mm});
            skLineSegment(sketch, "E357", {"start": v(-17.72, 39.68) * mm, "end": v(-17.52, 39.55) * mm});
            skLineSegment(sketch, "E358", {"start": v(-18.66, 40.19) * mm, "end": v(-17.72, 39.68) * mm});
            skLineSegment(sketch, "E359", {"start": v(-19.06, 40.63) * mm, "end": v(-18.66, 40.19) * mm});
            skLineSegment(sketch, "E360", {"start": v(-19.35, 41.14) * mm, "end": v(-19.06, 40.63) * mm});
            skLineSegment(sketch, "E361", {"start": v(-19.54, 41.69) * mm, "end": v(-19.35, 41.14) * mm});
            skLineSegment(sketch, "E362", {"start": v(-19.61, 42.26) * mm, "end": v(-19.54, 41.69) * mm});
            skLineSegment(sketch, "E363", {"start": v(-19.46, 43.35) * mm, "end": v(-19.61, 42.26) * mm});
            skLineSegment(sketch, "E364", {"start": v(-18.86, 45.37) * mm, "end": v(-19.46, 43.35) * mm});
            skLineSegment(sketch, "E365", {"start": v(-17.51, 49.35) * mm, "end": v(-18.86, 45.37) * mm});
            skLineSegment(sketch, "E366", {"start": v(-15.93, 53.17) * mm, "end": v(-17.51, 49.35) * mm});
            skLineSegment(sketch, "E367", {"start": v(-15.91, 53.55) * mm, "end": v(-15.93, 53.17) * mm});
            skLineSegment(sketch, "E368", {"start": v(-15.94, 53.72) * mm, "end": v(-15.91, 53.55) * mm});
            skLineSegment(sketch, "E369", {"start": v(-15.97, 53.77) * mm, "end": v(-15.94, 53.72) * mm});
            skLineSegment(sketch, "E370", {"start": v(-16, 53.81) * mm, "end": v(-15.97, 53.77) * mm});
            skLineSegment(sketch, "E371", {"start": v(-16.13, 53.93) * mm, "end": v(-16, 53.81) * mm});
            skLineSegment(sketch, "E372", {"start": v(-16.3, 54.04) * mm, "end": v(-16.13, 53.93) * mm});
            skLineSegment(sketch, "E373", {"start": v(-16.7, 54.28) * mm, "end": v(-16.3, 54.04) * mm});
            skLineSegment(sketch, "E374", {"start": v(-16.82, 54.36) * mm, "end": v(-16.7, 54.28) * mm});
            skLineSegment(sketch, "E375", {"start": v(-16.96, 54.43) * mm, "end": v(-16.82, 54.36) * mm});
            skLineSegment(sketch, "E376", {"start": v(-17.23, 54.58) * mm, "end": v(-16.96, 54.43) * mm});
            skLineSegment(sketch, "E377", {"start": v(-17.79, 54.85) * mm, "end": v(-17.23, 54.58) * mm});
            skLineSegment(sketch, "E378", {"start": v(-18.25, 55.05) * mm, "end": v(-17.79, 54.85) * mm});
            skLineSegment(sketch, "E379", {"start": v(-18.65, 55.2) * mm, "end": v(-18.25, 55.05) * mm});
            skLineSegment(sketch, "E380", {"start": v(-18.72, 55.22) * mm, "end": v(-18.65, 55.2) * mm});
            skLineSegment(sketch, "E381", {"start": v(-18.8, 55.22) * mm, "end": v(-18.72, 55.22) * mm});
            skLineSegment(sketch, "E382", {"start": v(-18.88, 55.21) * mm, "end": v(-18.8, 55.22) * mm});
            skLineSegment(sketch, "E383", {"start": v(-18.96, 55.2) * mm, "end": v(-18.88, 55.21) * mm});
            skLineSegment(sketch, "E384", {"start": v(-19.04, 55.16) * mm, "end": v(-18.96, 55.2) * mm});
            skLineSegment(sketch, "E385", {"start": v(-19.1, 55.13) * mm, "end": v(-19.04, 55.16) * mm});
            skLineSegment(sketch, "E386", {"start": v(-19.22, 55.01) * mm, "end": v(-19.1, 55.13) * mm});
            skLineSegment(sketch, "E387", {"start": v(-19.45, 54.67) * mm, "end": v(-19.22, 55.01) * mm});
            skLineSegment(sketch, "E388", {"start": v(-20.17, 53.02) * mm, "end": v(-19.45, 54.67) * mm});
            skLineSegment(sketch, "E389", {"start": v(-21.53, 48.78) * mm, "end": v(-20.17, 53.02) * mm});
            skLineSegment(sketch, "E390", {"start": v(-23.12, 44.57) * mm, "end": v(-21.53, 48.78) * mm});
            skLineSegment(sketch, "E391", {"start": v(-23.95, 42.67) * mm, "end": v(-23.12, 44.57) * mm});
            skLineSegment(sketch, "E392", {"start": v(-24.92, 40.83) * mm, "end": v(-23.95, 42.67) * mm});
            skLineSegment(sketch, "E393", {"start": v(-26.11, 39.1) * mm, "end": v(-24.92, 40.83) * mm});
            skLineSegment(sketch, "E394", {"start": v(-26.94, 38.42) * mm, "end": v(-26.11, 39.1) * mm});
            skLineSegment(sketch, "E395", {"start": v(-27.19, 38.26) * mm, "end": v(-26.94, 38.42) * mm});
            skLineSegment(sketch, "E396", {"start": v(-27.47, 38.14) * mm, "end": v(-27.19, 38.26) * mm});
            skLineSegment(sketch, "E397", {"start": v(21.45, 35.88) * mm, "end": v(22.1, 35.65) * mm});
            skLineSegment(sketch, "E398", {"start": v(20.43, 36.09) * mm, "end": v(21.45, 35.88) * mm});
            skLineSegment(sketch, "E399", {"start": v(18.32, 36.37) * mm, "end": v(20.43, 36.09) * mm});
            skLineSegment(sketch, "E400", {"start": v(16.2, 36.65) * mm, "end": v(18.32, 36.37) * mm});
            skLineSegment(sketch, "E401", {"start": v(15.18, 36.64) * mm, "end": v(16.2, 36.65) * mm});
            skLineSegment(sketch, "E402", {"start": v(14.23, 36.43) * mm, "end": v(15.18, 36.64) * mm});
            skLineSegment(sketch, "E403", {"start": v(11.79, 34.36) * mm, "end": v(14.23, 36.43) * mm});
            skLineSegment(sketch, "E404", {"start": v(9.02, 32.62) * mm, "end": v(11.79, 34.36) * mm});
            skLineSegment(sketch, "E405", {"start": v(6.03, 31.28) * mm, "end": v(9.02, 32.62) * mm});
            skLineSegment(sketch, "E406", {"start": v(2.88, 30.37) * mm, "end": v(6.03, 31.28) * mm});
            skLineSegment(sketch, "E407", {"start": v(-0.36, 29.92) * mm, "end": v(2.88, 30.37) * mm});
            skLineSegment(sketch, "E408", {"start": v(-3.64, 29.92) * mm, "end": v(-0.36, 29.92) * mm});
            skLineSegment(sketch, "E409", {"start": v(-6.88, 30.39) * mm, "end": v(-3.64, 29.92) * mm});
            skLineSegment(sketch, "E410", {"start": v(-10.02, 31.3) * mm, "end": v(-6.88, 30.39) * mm});
            skLineSegment(sketch, "E411", {"start": v(-13, 32.65) * mm, "end": v(-10.02, 31.3) * mm});
            skLineSegment(sketch, "E412", {"start": v(-15.77, 34.4) * mm, "end": v(-13, 32.65) * mm});
            skLineSegment(sketch, "E413", {"start": v(-18.2, 36.49) * mm, "end": v(-15.77, 34.4) * mm});
            skLineSegment(sketch, "E414", {"start": v(-19.13, 36.72) * mm, "end": v(-18.2, 36.49) * mm});
            skLineSegment(sketch, "E415", {"start": v(-20.1, 36.77) * mm, "end": v(-19.13, 36.72) * mm});
            skLineSegment(sketch, "E416", {"start": v(-22.13, 36.46) * mm, "end": v(-20.1, 36.77) * mm});
            skLineSegment(sketch, "E417", {"start": v(-24.1, 35.93) * mm, "end": v(-22.13, 36.46) * mm});
            skLineSegment(sketch, "E418", {"start": v(-24.97, 35.48) * mm, "end": v(-24.1, 35.93) * mm});
            skLineSegment(sketch, "E419", {"start": v(-25.59, 35.06) * mm, "end": v(-24.97, 35.48) * mm});
            skLineSegment(sketch, "E420", {"start": v(-23.34, 32.42) * mm, "end": v(-25.59, 35.06) * mm});
            skLineSegment(sketch, "E421", {"start": v(-20.58, 29.91) * mm, "end": v(-23.34, 32.42) * mm});
            skLineSegment(sketch, "E422", {"start": v(-17.53, 27.76) * mm, "end": v(-20.58, 29.91) * mm});
            skLineSegment(sketch, "E423", {"start": v(-14.24, 26.02) * mm, "end": v(-17.53, 27.76) * mm});
            skLineSegment(sketch, "E424", {"start": v(-10.75, 24.7) * mm, "end": v(-14.24, 26.02) * mm});
            skLineSegment(sketch, "E425", {"start": v(-7.13, 23.81) * mm, "end": v(-10.75, 24.7) * mm});
            skLineSegment(sketch, "E426", {"start": v(-3.42, 23.4) * mm, "end": v(-7.13, 23.81) * mm});
            skLineSegment(sketch, "E427", {"start": v(0.3, 23.45) * mm, "end": v(-3.42, 23.4) * mm});
            skLineSegment(sketch, "E428", {"start": v(4, 23.97) * mm, "end": v(0.3, 23.45) * mm});
            skLineSegment(sketch, "E429", {"start": v(7.6, 24.94) * mm, "end": v(4, 23.97) * mm});
            skLineSegment(sketch, "E430", {"start": v(11.05, 26.36) * mm, "end": v(7.6, 24.94) * mm});
            skLineSegment(sketch, "E431", {"start": v(14.3, 28.2) * mm, "end": v(11.05, 26.36) * mm});
            skLineSegment(sketch, "E432", {"start": v(17.28, 30.42) * mm, "end": v(14.3, 28.2) * mm});
            skLineSegment(sketch, "E433", {"start": v(19.97, 33.01) * mm, "end": v(17.28, 30.42) * mm});
            skLineSegment(sketch, "E434", {"start": v(22.1, 35.65) * mm, "end": v(19.97, 33.01) * mm});
            skSolve(sketch);
        }
        {
            var Q0;
            Q0=makeQuery(id+"F12.imprint","IMPRINT",FACE,{"disambiguationData":[TD([[makeQuery(id+"F12.imprint","IMPRINT",EDGE,{"derivedFrom":sQuery(id+"F12.wireOp",EDGE,"E13")}),-1.0]])]});
            var Q1;
            Q1=makeQuery(id+"F12.imprint","IMPRINT",FACE,{"disambiguationData":[TD([[makeQuery(id+"F12.imprint","IMPRINT",EDGE,{"derivedFrom":sQuery(id+"F12.wireOp",EDGE,"E100")}),-1.0]])]});
            var Q2;
            Q2=makeQuery(id+"F12.imprint","IMPRINT",FACE,{"disambiguationData":[TD([[makeQuery(id+"F12.imprint","IMPRINT",EDGE,{"derivedFrom":sQuery(id+"F12.wireOp",EDGE,"E217")}),-1.0]])]});
            var Q3;
            Q3=makeQuery(id+"F12.imprint","IMPRINT",FACE,{"disambiguationData":[TD([[makeQuery(id+"F12.imprint","IMPRINT",EDGE,{"derivedFrom":sQuery(id+"F12.wireOp",EDGE,"E397")}),-1.0]])]});
            var Q4;
            Q4=makeQuery(id+"F12.imprint","IMPRINT",FACE,{"disambiguationData":[TD([[makeQuery(id+"F12.imprint","IMPRINT",EDGE,{"derivedFrom":sQuery(id+"F12.wireOp",EDGE,"E339")}),-1.0]])]});
            var Q5;
            Q5=sQuery(id+"F12.wireOp",EDGE,"E13");
            var Q6;
            Q6=sQuery(id+"F12.wireOp",EDGE,"E14");
            var Q7;
            Q7=sQuery(id+"F12.wireOp",EDGE,"E15");
            var Q8;
            Q8=sQuery(id+"F12.wireOp",EDGE,"E16");
            var Q9;
            Q9=sQuery(id+"F12.wireOp",EDGE,"E17");
            var Q10;
            Q10=sQuery(id+"F12.wireOp",EDGE,"E18");
            var Q11;
            Q11=sQuery(id+"F12.wireOp",EDGE,"E19");
            var Q12;
            Q12=sQuery(id+"F12.wireOp",EDGE,"E20");
            var Q13;
            Q13=sQuery(id+"F12.wireOp",EDGE,"E21");
            var Q14;
            Q14=sQuery(id+"F12.wireOp",EDGE,"E22");
            var Q15;
            Q15=sQuery(id+"F12.wireOp",EDGE,"E23");
            var Q16;
            Q16=sQuery(id+"F12.wireOp",EDGE,"E24");
            var Q17;
            Q17=sQuery(id+"F12.wireOp",EDGE,"E25");
            var Q18;
            Q18=sQuery(id+"F12.wireOp",EDGE,"E26");
            var Q19;
            Q19=sQuery(id+"F12.wireOp",EDGE,"E27");
            var Q20;
            Q20=sQuery(id+"F12.wireOp",EDGE,"E28");
            var Q21;
            Q21=sQuery(id+"F12.wireOp",EDGE,"E29");
            var Q22;
            Q22=sQuery(id+"F12.wireOp",EDGE,"E30");
            var Q23;
            Q23=sQuery(id+"F12.wireOp",EDGE,"E31");
            var Q24;
            Q24=sQuery(id+"F12.wireOp",EDGE,"E32");
            var Q25;
            Q25=sQuery(id+"F12.wireOp",EDGE,"E33");
            var Q26;
            Q26=sQuery(id+"F12.wireOp",EDGE,"E34");
            var Q27;
            Q27=sQuery(id+"F12.wireOp",EDGE,"E35");
            var Q28;
            Q28=sQuery(id+"F12.wireOp",EDGE,"E36");
            var Q29;
            Q29=sQuery(id+"F12.wireOp",EDGE,"E37");
            var Q30;
            Q30=sQuery(id+"F12.wireOp",EDGE,"E38");
            var Q31;
            Q31=sQuery(id+"F12.wireOp",EDGE,"E39");
            var Q32;
            Q32=sQuery(id+"F12.wireOp",EDGE,"E40");
            var Q33;
            Q33=sQuery(id+"F12.wireOp",EDGE,"E41");
            var Q34;
            Q34=sQuery(id+"F12.wireOp",EDGE,"E42");
            var Q35;
            Q35=sQuery(id+"F12.wireOp",EDGE,"E43");
            var Q36;
            Q36=sQuery(id+"F12.wireOp",EDGE,"E44");
            var Q37;
            Q37=sQuery(id+"F12.wireOp",EDGE,"E45");
            var Q38;
            Q38=sQuery(id+"F12.wireOp",EDGE,"E46");
            var Q39;
            Q39=sQuery(id+"F12.wireOp",EDGE,"E47");
            var Q40;
            Q40=sQuery(id+"F12.wireOp",EDGE,"E48");
            var Q41;
            Q41=sQuery(id+"F12.wireOp",EDGE,"E49");
            var Q42;
            Q42=sQuery(id+"F12.wireOp",EDGE,"E50");
            var Q43;
            Q43=sQuery(id+"F12.wireOp",EDGE,"E51");
            var Q44;
            Q44=sQuery(id+"F12.wireOp",EDGE,"E52");
            var Q45;
            Q45=sQuery(id+"F12.wireOp",EDGE,"E53");
            var Q46;
            Q46=sQuery(id+"F12.wireOp",EDGE,"E54");
            var Q47;
            Q47=sQuery(id+"F12.wireOp",EDGE,"E55");
            var Q48;
            Q48=sQuery(id+"F12.wireOp",EDGE,"E56");
            var Q49;
            Q49=sQuery(id+"F12.wireOp",EDGE,"E57");
            var Q50;
            Q50=sQuery(id+"F12.wireOp",EDGE,"E58");
            var Q51;
            Q51=sQuery(id+"F12.wireOp",EDGE,"E59");
            var Q52;
            Q52=sQuery(id+"F12.wireOp",EDGE,"E60");
            var Q53;
            Q53=sQuery(id+"F12.wireOp",EDGE,"E61");
            var Q54;
            Q54=sQuery(id+"F12.wireOp",EDGE,"E62");
            var Q55;
            Q55=sQuery(id+"F12.wireOp",EDGE,"E63");
            var Q56;
            Q56=sQuery(id+"F12.wireOp",EDGE,"E64");
            var Q57;
            Q57=sQuery(id+"F12.wireOp",EDGE,"E65");
            var Q58;
            Q58=sQuery(id+"F12.wireOp",EDGE,"E66");
            var Q59;
            Q59=sQuery(id+"F12.wireOp",EDGE,"E67");
            var Q60;
            Q60=sQuery(id+"F12.wireOp",EDGE,"E68");
            var Q61;
            Q61=sQuery(id+"F12.wireOp",EDGE,"E69");
            var Q62;
            Q62=sQuery(id+"F12.wireOp",EDGE,"E70");
            var Q63;
            Q63=sQuery(id+"F12.wireOp",EDGE,"E71");
            var Q64;
            Q64=sQuery(id+"F12.wireOp",EDGE,"E72");
            var Q65;
            Q65=sQuery(id+"F12.wireOp",EDGE,"E73");
            var Q66;
            Q66=sQuery(id+"F12.wireOp",EDGE,"E74");
            var Q67;
            Q67=sQuery(id+"F12.wireOp",EDGE,"E75");
            var Q68;
            Q68=sQuery(id+"F12.wireOp",EDGE,"E76");
            var Q69;
            Q69=sQuery(id+"F12.wireOp",EDGE,"E77");
            var Q70;
            Q70=sQuery(id+"F12.wireOp",EDGE,"E78");
            var Q71;
            Q71=sQuery(id+"F12.wireOp",EDGE,"E79");
            var Q72;
            Q72=sQuery(id+"F12.wireOp",EDGE,"E80");
            var Q73;
            Q73=sQuery(id+"F12.wireOp",EDGE,"E81");
            var Q74;
            Q74=sQuery(id+"F12.wireOp",EDGE,"E82");
            var Q75;
            Q75=sQuery(id+"F12.wireOp",EDGE,"E83");
            var Q76;
            Q76=sQuery(id+"F12.wireOp",EDGE,"E84");
            var Q77;
            Q77=sQuery(id+"F12.wireOp",EDGE,"E85");
            var Q78;
            Q78=sQuery(id+"F12.wireOp",EDGE,"E86");
            var Q79;
            Q79=sQuery(id+"F12.wireOp",EDGE,"E87");
            var Q80;
            Q80=sQuery(id+"F12.wireOp",EDGE,"E88");
            var Q81;
            Q81=sQuery(id+"F12.wireOp",EDGE,"E89");
            var Q82;
            Q82=sQuery(id+"F12.wireOp",EDGE,"E90");
            var Q83;
            Q83=sQuery(id+"F12.wireOp",EDGE,"E91");
            var Q84;
            Q84=sQuery(id+"F12.wireOp",EDGE,"E92");
            var Q85;
            Q85=sQuery(id+"F12.wireOp",EDGE,"E93");
            var Q86;
            Q86=sQuery(id+"F12.wireOp",EDGE,"E94");
            var Q87;
            Q87=sQuery(id+"F12.wireOp",EDGE,"E95");
            var Q88;
            Q88=sQuery(id+"F12.wireOp",EDGE,"E96");
            var Q89;
            Q89=sQuery(id+"F12.wireOp",EDGE,"E97");
            var Q90;
            Q90=sQuery(id+"F12.wireOp",EDGE,"E98");
            var Q91;
            Q91=sQuery(id+"F12.wireOp",EDGE,"E99");
            var Q92;
            Q92=sQuery(id+"F12.wireOp",EDGE,"E100");
            var Q93;
            Q93=sQuery(id+"F12.wireOp",EDGE,"E101");
            var Q94;
            Q94=sQuery(id+"F12.wireOp",EDGE,"E102");
            var Q95;
            Q95=sQuery(id+"F12.wireOp",EDGE,"E103");
            var Q96;
            Q96=sQuery(id+"F12.wireOp",EDGE,"E104");
            var Q97;
            Q97=sQuery(id+"F12.wireOp",EDGE,"E105");
            var Q98;
            Q98=sQuery(id+"F12.wireOp",EDGE,"E106");
            var Q99;
            Q99=sQuery(id+"F12.wireOp",EDGE,"E107");
            var Q100;
            Q100=sQuery(id+"F12.wireOp",EDGE,"E108");
            var Q101;
            Q101=sQuery(id+"F12.wireOp",EDGE,"E109");
            var Q102;
            Q102=sQuery(id+"F12.wireOp",EDGE,"E110");
            var Q103;
            Q103=sQuery(id+"F12.wireOp",EDGE,"E111");
            var Q104;
            Q104=sQuery(id+"F12.wireOp",EDGE,"E112");
            var Q105;
            Q105=sQuery(id+"F12.wireOp",EDGE,"E113");
            var Q106;
            Q106=sQuery(id+"F12.wireOp",EDGE,"E114");
            var Q107;
            Q107=sQuery(id+"F12.wireOp",EDGE,"E115");
            var Q108;
            Q108=sQuery(id+"F12.wireOp",EDGE,"E116");
            var Q109;
            Q109=sQuery(id+"F12.wireOp",EDGE,"E117");
            var Q110;
            Q110=sQuery(id+"F12.wireOp",EDGE,"E118");
            var Q111;
            Q111=sQuery(id+"F12.wireOp",EDGE,"E119");
            var Q112;
            Q112=sQuery(id+"F12.wireOp",EDGE,"E120");
            var Q113;
            Q113=sQuery(id+"F12.wireOp",EDGE,"E121");
            var Q114;
            Q114=sQuery(id+"F12.wireOp",EDGE,"E122");
            var Q115;
            Q115=sQuery(id+"F12.wireOp",EDGE,"E123");
            var Q116;
            Q116=sQuery(id+"F12.wireOp",EDGE,"E124");
            var Q117;
            Q117=sQuery(id+"F12.wireOp",EDGE,"E125");
            var Q118;
            Q118=sQuery(id+"F12.wireOp",EDGE,"E126");
            var Q119;
            Q119=sQuery(id+"F12.wireOp",EDGE,"E127");
            var Q120;
            Q120=sQuery(id+"F12.wireOp",EDGE,"E128");
            var Q121;
            Q121=sQuery(id+"F12.wireOp",EDGE,"E129");
            var Q122;
            Q122=sQuery(id+"F12.wireOp",EDGE,"E130");
            var Q123;
            Q123=sQuery(id+"F12.wireOp",EDGE,"E131");
            var Q124;
            Q124=sQuery(id+"F12.wireOp",EDGE,"E132");
            var Q125;
            Q125=sQuery(id+"F12.wireOp",EDGE,"E133");
            var Q126;
            Q126=sQuery(id+"F12.wireOp",EDGE,"E134");
            var Q127;
            Q127=sQuery(id+"F12.wireOp",EDGE,"E135");
            var Q128;
            Q128=sQuery(id+"F12.wireOp",EDGE,"E136");
            var Q129;
            Q129=sQuery(id+"F12.wireOp",EDGE,"E137");
            var Q130;
            Q130=sQuery(id+"F12.wireOp",EDGE,"E138");
            var Q131;
            Q131=sQuery(id+"F12.wireOp",EDGE,"E139");
            var Q132;
            Q132=sQuery(id+"F12.wireOp",EDGE,"E140");
            var Q133;
            Q133=sQuery(id+"F12.wireOp",EDGE,"E141");
            var Q134;
            Q134=sQuery(id+"F12.wireOp",EDGE,"E142");
            var Q135;
            Q135=sQuery(id+"F12.wireOp",EDGE,"E143");
            var Q136;
            Q136=sQuery(id+"F12.wireOp",EDGE,"E144");
            var Q137;
            Q137=sQuery(id+"F12.wireOp",EDGE,"E145");
            var Q138;
            Q138=sQuery(id+"F12.wireOp",EDGE,"E146");
            var Q139;
            Q139=sQuery(id+"F12.wireOp",EDGE,"E147");
            var Q140;
            Q140=sQuery(id+"F12.wireOp",EDGE,"E148");
            var Q141;
            Q141=sQuery(id+"F12.wireOp",EDGE,"E149");
            var Q142;
            Q142=sQuery(id+"F12.wireOp",EDGE,"E150");
            var Q143;
            Q143=sQuery(id+"F12.wireOp",EDGE,"E151");
            var Q144;
            Q144=sQuery(id+"F12.wireOp",EDGE,"E152");
            var Q145;
            Q145=sQuery(id+"F12.wireOp",EDGE,"E153");
            var Q146;
            Q146=sQuery(id+"F12.wireOp",EDGE,"E154");
            var Q147;
            Q147=sQuery(id+"F12.wireOp",EDGE,"E155");
            var Q148;
            Q148=sQuery(id+"F12.wireOp",EDGE,"E156");
            var Q149;
            Q149=sQuery(id+"F12.wireOp",EDGE,"E157");
            var Q150;
            Q150=sQuery(id+"F12.wireOp",EDGE,"E158");
            var Q151;
            Q151=sQuery(id+"F12.wireOp",EDGE,"E159");
            var Q152;
            Q152=sQuery(id+"F12.wireOp",EDGE,"E160");
            var Q153;
            Q153=sQuery(id+"F12.wireOp",EDGE,"E161");
            var Q154;
            Q154=sQuery(id+"F12.wireOp",EDGE,"E162");
            var Q155;
            Q155=sQuery(id+"F12.wireOp",EDGE,"E163");
            var Q156;
            Q156=sQuery(id+"F12.wireOp",EDGE,"E164");
            var Q157;
            Q157=sQuery(id+"F12.wireOp",EDGE,"E165");
            var Q158;
            Q158=sQuery(id+"F12.wireOp",EDGE,"E166");
            var Q159;
            Q159=sQuery(id+"F12.wireOp",EDGE,"E167");
            var Q160;
            Q160=sQuery(id+"F12.wireOp",EDGE,"E168");
            var Q161;
            Q161=sQuery(id+"F12.wireOp",EDGE,"E169");
            var Q162;
            Q162=sQuery(id+"F12.wireOp",EDGE,"E170");
            var Q163;
            Q163=sQuery(id+"F12.wireOp",EDGE,"E171");
            var Q164;
            Q164=sQuery(id+"F12.wireOp",EDGE,"E172");
            var Q165;
            Q165=sQuery(id+"F12.wireOp",EDGE,"E173");
            var Q166;
            Q166=sQuery(id+"F12.wireOp",EDGE,"E174");
            var Q167;
            Q167=sQuery(id+"F12.wireOp",EDGE,"E175");
            var Q168;
            Q168=sQuery(id+"F12.wireOp",EDGE,"E176");
            var Q169;
            Q169=sQuery(id+"F12.wireOp",EDGE,"E177");
            var Q170;
            Q170=sQuery(id+"F12.wireOp",EDGE,"E178");
            var Q171;
            Q171=sQuery(id+"F12.wireOp",EDGE,"E179");
            var Q172;
            Q172=sQuery(id+"F12.wireOp",EDGE,"E180");
            var Q173;
            Q173=sQuery(id+"F12.wireOp",EDGE,"E181");
            var Q174;
            Q174=sQuery(id+"F12.wireOp",EDGE,"E182");
            var Q175;
            Q175=sQuery(id+"F12.wireOp",EDGE,"E183");
            var Q176;
            Q176=sQuery(id+"F12.wireOp",EDGE,"E184");
            var Q177;
            Q177=sQuery(id+"F12.wireOp",EDGE,"E185");
            var Q178;
            Q178=sQuery(id+"F12.wireOp",EDGE,"E186");
            var Q179;
            Q179=sQuery(id+"F12.wireOp",EDGE,"E187");
            var Q180;
            Q180=sQuery(id+"F12.wireOp",EDGE,"E188");
            var Q181;
            Q181=sQuery(id+"F12.wireOp",EDGE,"E189");
            var Q182;
            Q182=sQuery(id+"F12.wireOp",EDGE,"E190");
            var Q183;
            Q183=sQuery(id+"F12.wireOp",EDGE,"E191");
            var Q184;
            Q184=sQuery(id+"F12.wireOp",EDGE,"E192");
            var Q185;
            Q185=sQuery(id+"F12.wireOp",EDGE,"E193");
            var Q186;
            Q186=sQuery(id+"F12.wireOp",EDGE,"E194");
            var Q187;
            Q187=sQuery(id+"F12.wireOp",EDGE,"E195");
            var Q188;
            Q188=sQuery(id+"F12.wireOp",EDGE,"E196");
            var Q189;
            Q189=sQuery(id+"F12.wireOp",EDGE,"E197");
            var Q190;
            Q190=sQuery(id+"F12.wireOp",EDGE,"E198");
            var Q191;
            Q191=sQuery(id+"F12.wireOp",EDGE,"E199");
            var Q192;
            Q192=sQuery(id+"F12.wireOp",EDGE,"E200");
            var Q193;
            Q193=sQuery(id+"F12.wireOp",EDGE,"E201");
            var Q194;
            Q194=sQuery(id+"F12.wireOp",EDGE,"E202");
            var Q195;
            Q195=sQuery(id+"F12.wireOp",EDGE,"E203");
            var Q196;
            Q196=sQuery(id+"F12.wireOp",EDGE,"E204");
            var Q197;
            Q197=sQuery(id+"F12.wireOp",EDGE,"E205");
            var Q198;
            Q198=sQuery(id+"F12.wireOp",EDGE,"E206");
            var Q199;
            Q199=sQuery(id+"F12.wireOp",EDGE,"E207");
            var Q200;
            Q200=sQuery(id+"F12.wireOp",EDGE,"E208");
            var Q201;
            Q201=sQuery(id+"F12.wireOp",EDGE,"E209");
            var Q202;
            Q202=sQuery(id+"F12.wireOp",EDGE,"E210");
            var Q203;
            Q203=sQuery(id+"F12.wireOp",EDGE,"E211");
            var Q204;
            Q204=sQuery(id+"F12.wireOp",EDGE,"E212");
            var Q205;
            Q205=sQuery(id+"F12.wireOp",EDGE,"E213");
            var Q206;
            Q206=sQuery(id+"F12.wireOp",EDGE,"E214");
            var Q207;
            Q207=sQuery(id+"F12.wireOp",EDGE,"E215");
            var Q208;
            Q208=sQuery(id+"F12.wireOp",EDGE,"E216");
            var Q209;
            Q209=sQuery(id+"F12.wireOp",EDGE,"E217");
            var Q210;
            Q210=sQuery(id+"F12.wireOp",EDGE,"E218");
            var Q211;
            Q211=sQuery(id+"F12.wireOp",EDGE,"E219");
            var Q212;
            Q212=sQuery(id+"F12.wireOp",EDGE,"E220");
            var Q213;
            Q213=sQuery(id+"F12.wireOp",EDGE,"E221");
            var Q214;
            Q214=sQuery(id+"F12.wireOp",EDGE,"E222");
            var Q215;
            Q215=sQuery(id+"F12.wireOp",EDGE,"E223");
            var Q216;
            Q216=sQuery(id+"F12.wireOp",EDGE,"E224");
            var Q217;
            Q217=sQuery(id+"F12.wireOp",EDGE,"E225");
            var Q218;
            Q218=sQuery(id+"F12.wireOp",EDGE,"E226");
            var Q219;
            Q219=sQuery(id+"F12.wireOp",EDGE,"E227");
            var Q220;
            Q220=sQuery(id+"F12.wireOp",EDGE,"E228");
            var Q221;
            Q221=sQuery(id+"F12.wireOp",EDGE,"E229");
            var Q222;
            Q222=sQuery(id+"F12.wireOp",EDGE,"E230");
            var Q223;
            Q223=sQuery(id+"F12.wireOp",EDGE,"E231");
            var Q224;
            Q224=sQuery(id+"F12.wireOp",EDGE,"E232");
            var Q225;
            Q225=sQuery(id+"F12.wireOp",EDGE,"E233");
            var Q226;
            Q226=sQuery(id+"F12.wireOp",EDGE,"E234");
            var Q227;
            Q227=sQuery(id+"F12.wireOp",EDGE,"E235");
            var Q228;
            Q228=sQuery(id+"F12.wireOp",EDGE,"E236");
            var Q229;
            Q229=sQuery(id+"F12.wireOp",EDGE,"E237");
            var Q230;
            Q230=sQuery(id+"F12.wireOp",EDGE,"E238");
            var Q231;
            Q231=sQuery(id+"F12.wireOp",EDGE,"E239");
            var Q232;
            Q232=sQuery(id+"F12.wireOp",EDGE,"E240");
            var Q233;
            Q233=sQuery(id+"F12.wireOp",EDGE,"E241");
            var Q234;
            Q234=sQuery(id+"F12.wireOp",EDGE,"E242");
            var Q235;
            Q235=sQuery(id+"F12.wireOp",EDGE,"E243");
            var Q236;
            Q236=sQuery(id+"F12.wireOp",EDGE,"E244");
            var Q237;
            Q237=sQuery(id+"F12.wireOp",EDGE,"E245");
            var Q238;
            Q238=sQuery(id+"F12.wireOp",EDGE,"E246");
            var Q239;
            Q239=sQuery(id+"F12.wireOp",EDGE,"E247");
            var Q240;
            Q240=sQuery(id+"F12.wireOp",EDGE,"E248");
            var Q241;
            Q241=sQuery(id+"F12.wireOp",EDGE,"E249");
            var Q242;
            Q242=sQuery(id+"F12.wireOp",EDGE,"E250");
            var Q243;
            Q243=sQuery(id+"F12.wireOp",EDGE,"E251");
            var Q244;
            Q244=sQuery(id+"F12.wireOp",EDGE,"E252");
            var Q245;
            Q245=sQuery(id+"F12.wireOp",EDGE,"E253");
            var Q246;
            Q246=sQuery(id+"F12.wireOp",EDGE,"E254");
            var Q247;
            Q247=sQuery(id+"F12.wireOp",EDGE,"E255");
            var Q248;
            Q248=sQuery(id+"F12.wireOp",EDGE,"E256");
            var Q249;
            Q249=sQuery(id+"F12.wireOp",EDGE,"E257");
            var Q250;
            Q250=sQuery(id+"F12.wireOp",EDGE,"E258");
            var Q251;
            Q251=sQuery(id+"F12.wireOp",EDGE,"E259");
            var Q252;
            Q252=sQuery(id+"F12.wireOp",EDGE,"E260");
            var Q253;
            Q253=sQuery(id+"F12.wireOp",EDGE,"E261");
            var Q254;
            Q254=sQuery(id+"F12.wireOp",EDGE,"E262");
            var Q255;
            Q255=sQuery(id+"F12.wireOp",EDGE,"E263");
            var Q256;
            Q256=sQuery(id+"F12.wireOp",EDGE,"E264");
            var Q257;
            Q257=sQuery(id+"F12.wireOp",EDGE,"E265");
            var Q258;
            Q258=sQuery(id+"F12.wireOp",EDGE,"E266");
            var Q259;
            Q259=sQuery(id+"F12.wireOp",EDGE,"E267");
            var Q260;
            Q260=sQuery(id+"F12.wireOp",EDGE,"E268");
            var Q261;
            Q261=sQuery(id+"F12.wireOp",EDGE,"E269");
            var Q262;
            Q262=sQuery(id+"F12.wireOp",EDGE,"E270");
            var Q263;
            Q263=sQuery(id+"F12.wireOp",EDGE,"E271");
            var Q264;
            Q264=sQuery(id+"F12.wireOp",EDGE,"E272");
            var Q265;
            Q265=sQuery(id+"F12.wireOp",EDGE,"E273");
            var Q266;
            Q266=sQuery(id+"F12.wireOp",EDGE,"E274");
            var Q267;
            Q267=sQuery(id+"F12.wireOp",EDGE,"E275");
            var Q268;
            Q268=sQuery(id+"F12.wireOp",EDGE,"E276");
            var Q269;
            Q269=sQuery(id+"F12.wireOp",EDGE,"E277");
            var Q270;
            Q270=sQuery(id+"F12.wireOp",EDGE,"E278");
            var Q271;
            Q271=sQuery(id+"F12.wireOp",EDGE,"E279");
            var Q272;
            Q272=sQuery(id+"F12.wireOp",EDGE,"E280");
            var Q273;
            Q273=sQuery(id+"F12.wireOp",EDGE,"E281");
            var Q274;
            Q274=sQuery(id+"F12.wireOp",EDGE,"E282");
            var Q275;
            Q275=sQuery(id+"F12.wireOp",EDGE,"E283");
            var Q276;
            Q276=sQuery(id+"F12.wireOp",EDGE,"E284");
            var Q277;
            Q277=sQuery(id+"F12.wireOp",EDGE,"E285");
            var Q278;
            Q278=sQuery(id+"F12.wireOp",EDGE,"E286");
            var Q279;
            Q279=sQuery(id+"F12.wireOp",EDGE,"E287");
            var Q280;
            Q280=sQuery(id+"F12.wireOp",EDGE,"E288");
            var Q281;
            Q281=sQuery(id+"F12.wireOp",EDGE,"E289");
            var Q282;
            Q282=sQuery(id+"F12.wireOp",EDGE,"E290");
            var Q283;
            Q283=sQuery(id+"F12.wireOp",EDGE,"E291");
            var Q284;
            Q284=sQuery(id+"F12.wireOp",EDGE,"E292");
            var Q285;
            Q285=sQuery(id+"F12.wireOp",EDGE,"E293");
            var Q286;
            Q286=sQuery(id+"F12.wireOp",EDGE,"E294");
            var Q287;
            Q287=sQuery(id+"F12.wireOp",EDGE,"E295");
            var Q288;
            Q288=sQuery(id+"F12.wireOp",EDGE,"E296");
            var Q289;
            Q289=sQuery(id+"F12.wireOp",EDGE,"E297");
            var Q290;
            Q290=sQuery(id+"F12.wireOp",EDGE,"E298");
            var Q291;
            Q291=sQuery(id+"F12.wireOp",EDGE,"E299");
            var Q292;
            Q292=sQuery(id+"F12.wireOp",EDGE,"E300");
            var Q293;
            Q293=sQuery(id+"F12.wireOp",EDGE,"E301");
            var Q294;
            Q294=sQuery(id+"F12.wireOp",EDGE,"E302");
            var Q295;
            Q295=sQuery(id+"F12.wireOp",EDGE,"E303");
            var Q296;
            Q296=sQuery(id+"F12.wireOp",EDGE,"E304");
            var Q297;
            Q297=sQuery(id+"F12.wireOp",EDGE,"E305");
            var Q298;
            Q298=sQuery(id+"F12.wireOp",EDGE,"E306");
            var Q299;
            Q299=sQuery(id+"F12.wireOp",EDGE,"E307");
            var Q300;
            Q300=sQuery(id+"F12.wireOp",EDGE,"E308");
            var Q301;
            Q301=sQuery(id+"F12.wireOp",EDGE,"E309");
            var Q302;
            Q302=sQuery(id+"F12.wireOp",EDGE,"E310");
            var Q303;
            Q303=sQuery(id+"F12.wireOp",EDGE,"E311");
            var Q304;
            Q304=sQuery(id+"F12.wireOp",EDGE,"E312");
            var Q305;
            Q305=sQuery(id+"F12.wireOp",EDGE,"E313");
            var Q306;
            Q306=sQuery(id+"F12.wireOp",EDGE,"E314");
            var Q307;
            Q307=sQuery(id+"F12.wireOp",EDGE,"E315");
            var Q308;
            Q308=sQuery(id+"F12.wireOp",EDGE,"E316");
            var Q309;
            Q309=sQuery(id+"F12.wireOp",EDGE,"E317");
            var Q310;
            Q310=sQuery(id+"F12.wireOp",EDGE,"E318");
            var Q311;
            Q311=sQuery(id+"F12.wireOp",EDGE,"E319");
            var Q312;
            Q312=sQuery(id+"F12.wireOp",EDGE,"E320");
            var Q313;
            Q313=sQuery(id+"F12.wireOp",EDGE,"E321");
            var Q314;
            Q314=sQuery(id+"F12.wireOp",EDGE,"E322");
            var Q315;
            Q315=sQuery(id+"F12.wireOp",EDGE,"E323");
            var Q316;
            Q316=sQuery(id+"F12.wireOp",EDGE,"E324");
            var Q317;
            Q317=sQuery(id+"F12.wireOp",EDGE,"E325");
            var Q318;
            Q318=sQuery(id+"F12.wireOp",EDGE,"E326");
            var Q319;
            Q319=sQuery(id+"F12.wireOp",EDGE,"E327");
            var Q320;
            Q320=sQuery(id+"F12.wireOp",EDGE,"E328");
            var Q321;
            Q321=sQuery(id+"F12.wireOp",EDGE,"E329");
            var Q322;
            Q322=sQuery(id+"F12.wireOp",EDGE,"E330");
            var Q323;
            Q323=sQuery(id+"F12.wireOp",EDGE,"E331");
            var Q324;
            Q324=sQuery(id+"F12.wireOp",EDGE,"E332");
            var Q325;
            Q325=sQuery(id+"F12.wireOp",EDGE,"E333");
            var Q326;
            Q326=sQuery(id+"F12.wireOp",EDGE,"E334");
            var Q327;
            Q327=sQuery(id+"F12.wireOp",EDGE,"E335");
            var Q328;
            Q328=sQuery(id+"F12.wireOp",EDGE,"E336");
            var Q329;
            Q329=sQuery(id+"F12.wireOp",EDGE,"E337");
            var Q330;
            Q330=sQuery(id+"F12.wireOp",EDGE,"E338");
            var Q331;
            Q331=sQuery(id+"F12.wireOp",EDGE,"E339");
            var Q332;
            Q332=sQuery(id+"F12.wireOp",EDGE,"E340");
            var Q333;
            Q333=sQuery(id+"F12.wireOp",EDGE,"E341");
            var Q334;
            Q334=sQuery(id+"F12.wireOp",EDGE,"E342");
            var Q335;
            Q335=sQuery(id+"F12.wireOp",EDGE,"E343");
            var Q336;
            Q336=sQuery(id+"F12.wireOp",EDGE,"E344");
            var Q337;
            Q337=sQuery(id+"F12.wireOp",EDGE,"E345");
            var Q338;
            Q338=sQuery(id+"F12.wireOp",EDGE,"E346");
            var Q339;
            Q339=sQuery(id+"F12.wireOp",EDGE,"E347");
            var Q340;
            Q340=sQuery(id+"F12.wireOp",EDGE,"E348");
            var Q341;
            Q341=sQuery(id+"F12.wireOp",EDGE,"E349");
            var Q342;
            Q342=sQuery(id+"F12.wireOp",EDGE,"E350");
            var Q343;
            Q343=sQuery(id+"F12.wireOp",EDGE,"E351");
            var Q344;
            Q344=sQuery(id+"F12.wireOp",EDGE,"E352");
            var Q345;
            Q345=sQuery(id+"F12.wireOp",EDGE,"E353");
            var Q346;
            Q346=sQuery(id+"F12.wireOp",EDGE,"E354");
            var Q347;
            Q347=sQuery(id+"F12.wireOp",EDGE,"E355");
            var Q348;
            Q348=sQuery(id+"F12.wireOp",EDGE,"E356");
            var Q349;
            Q349=sQuery(id+"F12.wireOp",EDGE,"E357");
            var Q350;
            Q350=sQuery(id+"F12.wireOp",EDGE,"E358");
            var Q351;
            Q351=sQuery(id+"F12.wireOp",EDGE,"E359");
            var Q352;
            Q352=sQuery(id+"F12.wireOp",EDGE,"E360");
            var Q353;
            Q353=sQuery(id+"F12.wireOp",EDGE,"E361");
            var Q354;
            Q354=sQuery(id+"F12.wireOp",EDGE,"E362");
            var Q355;
            Q355=sQuery(id+"F12.wireOp",EDGE,"E363");
            var Q356;
            Q356=sQuery(id+"F12.wireOp",EDGE,"E364");
            var Q357;
            Q357=sQuery(id+"F12.wireOp",EDGE,"E365");
            var Q358;
            Q358=sQuery(id+"F12.wireOp",EDGE,"E366");
            var Q359;
            Q359=sQuery(id+"F12.wireOp",EDGE,"E367");
            var Q360;
            Q360=sQuery(id+"F12.wireOp",EDGE,"E368");
            var Q361;
            Q361=sQuery(id+"F12.wireOp",EDGE,"E369");
            var Q362;
            Q362=sQuery(id+"F12.wireOp",EDGE,"E370");
            var Q363;
            Q363=sQuery(id+"F12.wireOp",EDGE,"E371");
            var Q364;
            Q364=sQuery(id+"F12.wireOp",EDGE,"E372");
            var Q365;
            Q365=sQuery(id+"F12.wireOp",EDGE,"E373");
            var Q366;
            Q366=sQuery(id+"F12.wireOp",EDGE,"E374");
            var Q367;
            Q367=sQuery(id+"F12.wireOp",EDGE,"E375");
            var Q368;
            Q368=sQuery(id+"F12.wireOp",EDGE,"E376");
            var Q369;
            Q369=sQuery(id+"F12.wireOp",EDGE,"E377");
            var Q370;
            Q370=sQuery(id+"F12.wireOp",EDGE,"E378");
            var Q371;
            Q371=sQuery(id+"F12.wireOp",EDGE,"E379");
            var Q372;
            Q372=sQuery(id+"F12.wireOp",EDGE,"E380");
            var Q373;
            Q373=sQuery(id+"F12.wireOp",EDGE,"E381");
            var Q374;
            Q374=sQuery(id+"F12.wireOp",EDGE,"E382");
            var Q375;
            Q375=sQuery(id+"F12.wireOp",EDGE,"E383");
            var Q376;
            Q376=sQuery(id+"F12.wireOp",EDGE,"E384");
            var Q377;
            Q377=sQuery(id+"F12.wireOp",EDGE,"E385");
            var Q378;
            Q378=sQuery(id+"F12.wireOp",EDGE,"E386");
            var Q379;
            Q379=sQuery(id+"F12.wireOp",EDGE,"E387");
            var Q380;
            Q380=sQuery(id+"F12.wireOp",EDGE,"E388");
            var Q381;
            Q381=sQuery(id+"F12.wireOp",EDGE,"E389");
            var Q382;
            Q382=sQuery(id+"F12.wireOp",EDGE,"E390");
            var Q383;
            Q383=sQuery(id+"F12.wireOp",EDGE,"E391");
            var Q384;
            Q384=sQuery(id+"F12.wireOp",EDGE,"E392");
            var Q385;
            Q385=sQuery(id+"F12.wireOp",EDGE,"E393");
            var Q386;
            Q386=sQuery(id+"F12.wireOp",EDGE,"E394");
            var Q387;
            Q387=sQuery(id+"F12.wireOp",EDGE,"E395");
            var Q388;
            Q388=sQuery(id+"F12.wireOp",EDGE,"E396");
            var Q389;
            Q389=sQuery(id+"F12.wireOp",EDGE,"E397");
            var Q390;
            Q390=sQuery(id+"F12.wireOp",EDGE,"E398");
            var Q391;
            Q391=sQuery(id+"F12.wireOp",EDGE,"E399");
            var Q392;
            Q392=sQuery(id+"F12.wireOp",EDGE,"E400");
            var Q393;
            Q393=sQuery(id+"F12.wireOp",EDGE,"E401");
            var Q394;
            Q394=sQuery(id+"F12.wireOp",EDGE,"E402");
            var Q395;
            Q395=sQuery(id+"F12.wireOp",EDGE,"E403");
            var Q396;
            Q396=sQuery(id+"F12.wireOp",EDGE,"E404");
            var Q397;
            Q397=sQuery(id+"F12.wireOp",EDGE,"E405");
            var Q398;
            Q398=sQuery(id+"F12.wireOp",EDGE,"E406");
            var Q399;
            Q399=sQuery(id+"F12.wireOp",EDGE,"E407");
            var Q400;
            Q400=sQuery(id+"F12.wireOp",EDGE,"E408");
            var Q401;
            Q401=sQuery(id+"F12.wireOp",EDGE,"E409");
            var Q402;
            Q402=sQuery(id+"F12.wireOp",EDGE,"E410");
            var Q403;
            Q403=sQuery(id+"F12.wireOp",EDGE,"E411");
            var Q404;
            Q404=sQuery(id+"F12.wireOp",EDGE,"E412");
            var Q405;
            Q405=sQuery(id+"F12.wireOp",EDGE,"E413");
            var Q406;
            Q406=sQuery(id+"F12.wireOp",EDGE,"E414");
            var Q407;
            Q407=sQuery(id+"F12.wireOp",EDGE,"E415");
            var Q408;
            Q408=sQuery(id+"F12.wireOp",EDGE,"E416");
            var Q409;
            Q409=sQuery(id+"F12.wireOp",EDGE,"E417");
            var Q410;
            Q410=sQuery(id+"F12.wireOp",EDGE,"E418");
            var Q411;
            Q411=sQuery(id+"F12.wireOp",EDGE,"E419");
            var Q412;
            Q412=sQuery(id+"F12.wireOp",EDGE,"E420");
            var Q413;
            Q413=sQuery(id+"F12.wireOp",EDGE,"E421");
            var Q414;
            Q414=sQuery(id+"F12.wireOp",EDGE,"E422");
            var Q415;
            Q415=sQuery(id+"F12.wireOp",EDGE,"E423");
            var Q416;
            Q416=sQuery(id+"F12.wireOp",EDGE,"E424");
            var Q417;
            Q417=sQuery(id+"F12.wireOp",EDGE,"E425");
            var Q418;
            Q418=sQuery(id+"F12.wireOp",EDGE,"E426");
            var Q419;
            Q419=sQuery(id+"F12.wireOp",EDGE,"E427");
            var Q420;
            Q420=sQuery(id+"F12.wireOp",EDGE,"E428");
            var Q421;
            Q421=sQuery(id+"F12.wireOp",EDGE,"E429");
            var Q422;
            Q422=sQuery(id+"F12.wireOp",EDGE,"E430");
            var Q423;
            Q423=sQuery(id+"F12.wireOp",EDGE,"E431");
            var Q424;
            Q424=sQuery(id+"F12.wireOp",EDGE,"E432");
            var Q425;
            Q425=sQuery(id+"F12.wireOp",EDGE,"E433");
            var Q426;
            Q426=sQuery(id+"F12.wireOp",EDGE,"E434");
            extrude(context, id + "F13", {"entities" : qUnion([Q0, Q1, Q2, Q3, Q4]), "operationType" : NewBodyOperationType.REMOVE, "surfaceEntities" : qUnion([Q5, Q6, Q7, Q8, Q9, Q10, Q11, Q12, Q13, Q14, Q15, Q16, Q17, Q18, Q19, Q20, Q21, Q22, Q23, Q24, Q25, Q26, Q27, Q28, Q29, Q30, Q31, Q32, Q33, Q34, Q35, Q36, Q37, Q38, Q39, Q40, Q41, Q42, Q43, Q44, Q45, Q46, Q47, Q48, Q49, Q50, Q51, Q52, Q53, Q54, Q55, Q56, Q57, Q58, Q59, Q60, Q61, Q62, Q63, Q64, Q65, Q66, Q67, Q68, Q69, Q70, Q71, Q72, Q73, Q74, Q75, Q76, Q77, Q78, Q79, Q80, Q81, Q82, Q83, Q84, Q85, Q86, Q87, Q88, Q89, Q90, Q91, Q92, Q93, Q94, Q95, Q96, Q97, Q98, Q99, Q100, Q101, Q102, Q103, Q104, Q105, Q106, Q107, Q108, Q109, Q110, Q111, Q112, Q113, Q114, Q115, Q116, Q117, Q118, Q119, Q120, Q121, Q122, Q123, Q124, Q125, Q126, Q127, Q128, Q129, Q130, Q131, Q132, Q133, Q134, Q135, Q136, Q137, Q138, Q139, Q140, Q141, Q142, Q143, Q144, Q145, Q146, Q147, Q148, Q149, Q150, Q151, Q152, Q153, Q154, Q155, Q156, Q157, Q158, Q159, Q160, Q161, Q162, Q163, Q164, Q165, Q166, Q167, Q168, Q169, Q170, Q171, Q172, Q173, Q174, Q175, Q176, Q177, Q178, Q179, Q180, Q181, Q182, Q183, Q184, Q185, Q186, Q187, Q188, Q189, Q190, Q191, Q192, Q193, Q194, Q195, Q196, Q197, Q198, Q199, Q200, Q201, Q202, Q203, Q204, Q205, Q206, Q207, Q208, Q209, Q210, Q211, Q212, Q213, Q214, Q215, Q216, Q217, Q218, Q219, Q220, Q221, Q222, Q223, Q224, Q225, Q226, Q227, Q228, Q229, Q230, Q231, Q232, Q233, Q234, Q235, Q236, Q237, Q238, Q239, Q240, Q241, Q242, Q243, Q244, Q245, Q246, Q247, Q248, Q249, Q250, Q251, Q252, Q253, Q254, Q255, Q256, Q257, Q258, Q259, Q260, Q261, Q262, Q263, Q264, Q265, Q266, Q267, Q268, Q269, Q270, Q271, Q272, Q273, Q274, Q275, Q276, Q277, Q278, Q279, Q280, Q281, Q282, Q283, Q284, Q285, Q286, Q287, Q288, Q289, Q290, Q291, Q292, Q293, Q294, Q295, Q296, Q297, Q298, Q299, Q300, Q301, Q302, Q303, Q304, Q305, Q306, Q307, Q308, Q309, Q310, Q311, Q312, Q313, Q314, Q315, Q316, Q317, Q318, Q319, Q320, Q321, Q322, Q323, Q324, Q325, Q326, Q327, Q328, Q329, Q330, Q331, Q332, Q333, Q334, Q335, Q336, Q337, Q338, Q339, Q340, Q341, Q342, Q343, Q344, Q345, Q346, Q347, Q348, Q349, Q350, Q351, Q352, Q353, Q354, Q355, Q356, Q357, Q358, Q359, Q360, Q361, Q362, Q363, Q364, Q365, Q366, Q367, Q368, Q369, Q370, Q371, Q372, Q373, Q374, Q375, Q376, Q377, Q378, Q379, Q380, Q381, Q382, Q383, Q384, Q385, Q386, Q387, Q388, Q389, Q390, Q391, Q392, Q393, Q394, Q395, Q396, Q397, Q398, Q399, Q400, Q401, Q402, Q403, Q404, Q405, Q406, Q407, Q408, Q409, Q410, Q411, Q412, Q413, Q414, Q415, Q416, Q417, Q418, Q419, Q420, Q421, Q422, Q423, Q424, Q425, Q426]), "oppositeDirection" : true, "depth" : .6 * mm, "offsetDistance" : 25 * mm});
        }
        {
            var Q0;
            {var subQ0=sQuery(id+"F6.wireOp",EDGE,"E4.0");Q0=makeQuery(id+"F9.boolean.opBoolean","MERGE",FACE,{"derivedFrom":[makeQuery(id+"F7.opExtrude","SWEPT_FACE",FACE,{"disambiguationData":[OSD([subQ0])]}),makeQuery(id+"F9.opExtrude","SWEPT_FACE",FACE,{"disambiguationData":[OSD([subQ0])]})]});}
            var sketch = newSketch(context, id + "F14", { "sketchPlane" : qUnion([Q0])});
            skLineSegment(sketch, "E435", {"start": v(-24.17, 104.5) * mm, "end": v(-24.17, 0) * mm, "construction": true});
            skCircle(sketch, "E436", {"center": v(-24.17, 0) * mm, "radius": 10 * mm});
            skSolve(sketch);
        }
        {
            var Q0;
            {var subQ0=sQuery(id+"F14.wireOp",EDGE,"E436");var subQ1=makeQuery(id+"F7.opExtrude","CAP_EDGE",EDGE,{"disambiguationData":[OSD([sQuery(id+"F6.wireOp",EDGE,"E4.0")])],"isStart":true});var subQ2=makeQuery(id+"F14.imprint","INTERSECT",VERTEX,{"disambiguationData":[OD(0.0)],"derivedFrom":[subQ1,subQ0]});Q0=makeQuery(id+"F14.imprint","IMPRINT",FACE,{"disambiguationData":[TD([[makeQuery(id+"F14.imprint","IMPRINT",EDGE,{"disambiguationData":[TD([[subQ2,-1.0]])],"derivedFrom":subQ0}),1.0]])]});}
            extrude(context, id + "F15", {"entities" : qUnion([Q0]), "operationType" : NewBodyOperationType.REMOVE, "endBound" : BoundingType.THROUGH_ALL, "oppositeDirection" : true, "depth" : 25 * mm, "offsetDistance" : 25 * mm});
        }
        {
            var Q0;
            {var subQ0=sQuery(id+"F6.wireOp",EDGE,"E7.0");Q0=makeQuery(id+"F9.boolean.opBoolean","MERGE",FACE,{"derivedFrom":[makeQuery(id+"F7.opExtrude","SWEPT_FACE",FACE,{"disambiguationData":[OSD([subQ0])]}),makeQuery(id+"F9.opExtrude","SWEPT_FACE",FACE,{"disambiguationData":[OSD([subQ0])]})]});}
            var sketch = newSketch(context, id + "F16", { "sketchPlane" : qUnion([Q0])});
            skLineSegment(sketch, "E437", {"start": v(-1.54, 82.48) * mm, "end": v(2.36, 82.85) * mm});
            skLineSegment(sketch, "E438", {"start": v(-5.37, 81.6) * mm, "end": v(-1.54, 82.48) * mm});
            skLineSegment(sketch, "E439", {"start": v(-9.04, 80.24) * mm, "end": v(-5.37, 81.6) * mm});
            skLineSegment(sketch, "E440", {"start": v(-12.5, 78.4) * mm, "end": v(-9.04, 80.24) * mm});
            skLineSegment(sketch, "E441", {"start": v(-15.69, 76.12) * mm, "end": v(-12.5, 78.4) * mm});
            skLineSegment(sketch, "E442", {"start": v(-18.55, 73.44) * mm, "end": v(-15.69, 76.12) * mm});
            skLineSegment(sketch, "E443", {"start": v(-21.03, 70.4) * mm, "end": v(-18.55, 73.44) * mm});
            skLineSegment(sketch, "E444", {"start": v(-23.1, 67.07) * mm, "end": v(-21.03, 70.4) * mm});
            skLineSegment(sketch, "E445", {"start": v(-24.7, 63.5) * mm, "end": v(-23.1, 67.07) * mm});
            skLineSegment(sketch, "E446", {"start": v(-25.82, 59.74) * mm, "end": v(-24.7, 63.5) * mm});
            skLineSegment(sketch, "E447", {"start": v(-26.44, 55.87) * mm, "end": v(-25.82, 59.74) * mm});
            skLineSegment(sketch, "E448", {"start": v(-26.55, 51.95) * mm, "end": v(-26.44, 55.87) * mm});
            skLineSegment(sketch, "E449", {"start": v(-26.14, 48.06) * mm, "end": v(-26.55, 51.95) * mm});
            skLineSegment(sketch, "E450", {"start": v(-25.22, 44.25) * mm, "end": v(-26.14, 48.06) * mm});
            skLineSegment(sketch, "E451", {"start": v(-23.89, 40.8) * mm, "end": v(-25.22, 44.25) * mm});
            skLineSegment(sketch, "E452", {"start": v(-23.6, 40.9) * mm, "end": v(-23.89, 40.8) * mm});
            skLineSegment(sketch, "E453", {"start": v(-23.39, 41) * mm, "end": v(-23.6, 40.9) * mm});
            skLineSegment(sketch, "E454", {"start": v(-23.2, 41.12) * mm, "end": v(-23.39, 41) * mm});
            skLineSegment(sketch, "E455", {"start": v(-22.5, 41.91) * mm, "end": v(-23.2, 41.12) * mm});
            skLineSegment(sketch, "E456", {"start": v(-21.3, 43.7) * mm, "end": v(-22.5, 41.91) * mm});
            skLineSegment(sketch, "E457", {"start": v(-19.7, 47.7) * mm, "end": v(-21.3, 43.7) * mm});
            skLineSegment(sketch, "E458", {"start": v(-20.24, 49.39) * mm, "end": v(-19.7, 47.7) * mm});
            skLineSegment(sketch, "E459", {"start": v(-20.55, 51.24) * mm, "end": v(-20.24, 49.39) * mm});
            skLineSegment(sketch, "E460", {"start": v(-20.57, 53.11) * mm, "end": v(-20.55, 51.24) * mm});
            skLineSegment(sketch, "E461", {"start": v(-20.57, 53.37) * mm, "end": v(-20.57, 53.11) * mm});
            skLineSegment(sketch, "E462", {"start": v(-20.57, 53.63) * mm, "end": v(-20.57, 53.37) * mm});
            skLineSegment(sketch, "E463", {"start": v(-20.55, 54.14) * mm, "end": v(-20.57, 53.63) * mm});
            skLineSegment(sketch, "E464", {"start": v(-20.48, 55.16) * mm, "end": v(-20.55, 54.14) * mm});
            skLineSegment(sketch, "E465", {"start": v(-20.32, 56.47) * mm, "end": v(-20.48, 55.16) * mm});
            skLineSegment(sketch, "E466", {"start": v(-19.6, 59.75) * mm, "end": v(-20.32, 56.47) * mm});
            skLineSegment(sketch, "E467", {"start": v(-18.4, 62.89) * mm, "end": v(-19.6, 59.75) * mm});
            skLineSegment(sketch, "E468", {"start": v(-16.77, 65.83) * mm, "end": v(-18.4, 62.89) * mm});
            skLineSegment(sketch, "E469", {"start": v(-14.73, 68.5) * mm, "end": v(-16.77, 65.83) * mm});
            skLineSegment(sketch, "E470", {"start": v(-12.33, 70.85) * mm, "end": v(-14.73, 68.5) * mm});
            skLineSegment(sketch, "E471", {"start": v(-9.6, 72.83) * mm, "end": v(-12.33, 70.85) * mm});
            skLineSegment(sketch, "E472", {"start": v(-6.64, 74.4) * mm, "end": v(-9.6, 72.83) * mm});
            skLineSegment(sketch, "E473", {"start": v(-3.47, 75.53) * mm, "end": v(-6.64, 74.4) * mm});
            skLineSegment(sketch, "E474", {"start": v(-0.18, 76.18) * mm, "end": v(-3.47, 75.53) * mm});
            skLineSegment(sketch, "E475", {"start": v(-0.1, 76.2) * mm, "end": v(-0.18, 76.18) * mm});
            skLineSegment(sketch, "E476", {"start": v(0, 76.2) * mm, "end": v(-0.1, 76.2) * mm});
            skLineSegment(sketch, "E477", {"start": v(0.16, 76.22) * mm, "end": v(0, 76.2) * mm});
            skLineSegment(sketch, "E478", {"start": v(0.5, 76.26) * mm, "end": v(0.16, 76.22) * mm});
            skLineSegment(sketch, "E479", {"start": v(3.18, 76.36) * mm, "end": v(0.5, 76.26) * mm});
            skLineSegment(sketch, "E480", {"start": v(6.49, 76.13) * mm, "end": v(3.18, 76.36) * mm});
            skLineSegment(sketch, "E481", {"start": v(9.73, 75.42) * mm, "end": v(6.49, 76.13) * mm});
            skLineSegment(sketch, "E482", {"start": v(12.84, 74.26) * mm, "end": v(9.73, 75.42) * mm});
            skLineSegment(sketch, "E483", {"start": v(15.75, 72.67) * mm, "end": v(12.84, 74.26) * mm});
            skLineSegment(sketch, "E484", {"start": v(18.4, 70.68) * mm, "end": v(15.75, 72.67) * mm});
            skLineSegment(sketch, "E485", {"start": v(20.75, 68.34) * mm, "end": v(18.4, 70.68) * mm});
            skLineSegment(sketch, "E486", {"start": v(22.74, 65.68) * mm, "end": v(20.75, 68.34) * mm});
            skLineSegment(sketch, "E487", {"start": v(24.33, 62.77) * mm, "end": v(22.74, 65.68) * mm});
            skLineSegment(sketch, "E488", {"start": v(25.49, 59.66) * mm, "end": v(24.33, 62.77) * mm});
            skLineSegment(sketch, "E489", {"start": v(26.2, 56.43) * mm, "end": v(25.49, 59.66) * mm});
            skLineSegment(sketch, "E490", {"start": v(26.2, 56.34) * mm, "end": v(26.2, 56.43) * mm});
            skLineSegment(sketch, "E491", {"start": v(26.21, 56.26) * mm, "end": v(26.2, 56.34) * mm});
            skLineSegment(sketch, "E492", {"start": v(26.24, 56.1) * mm, "end": v(26.21, 56.26) * mm});
            skLineSegment(sketch, "E493", {"start": v(26.28, 55.76) * mm, "end": v(26.24, 56.1) * mm});
            skLineSegment(sketch, "E494", {"start": v(26.43, 53.12) * mm, "end": v(26.28, 55.76) * mm});
            skLineSegment(sketch, "E495", {"start": v(26.41, 49.86) * mm, "end": v(26.43, 53.12) * mm});
            skLineSegment(sketch, "E496", {"start": v(26.45, 49.49) * mm, "end": v(26.41, 49.86) * mm});
            skLineSegment(sketch, "E497", {"start": v(26.55, 49.15) * mm, "end": v(26.45, 49.49) * mm});
            skLineSegment(sketch, "E498", {"start": v(26.93, 48.47) * mm, "end": v(26.55, 49.15) * mm});
            skLineSegment(sketch, "E499", {"start": v(27.38, 47.76) * mm, "end": v(26.93, 48.47) * mm});
            skLineSegment(sketch, "E500", {"start": v(27.54, 47.34) * mm, "end": v(27.38, 47.76) * mm});
            skLineSegment(sketch, "E501", {"start": v(27.61, 46.91) * mm, "end": v(27.54, 47.34) * mm});
            skLineSegment(sketch, "E502", {"start": v(27.84, 45.3) * mm, "end": v(27.61, 46.91) * mm});
            skLineSegment(sketch, "E503", {"start": v(28.1, 44.58) * mm, "end": v(27.84, 45.3) * mm});
            skLineSegment(sketch, "E504", {"start": v(28.27, 44.26) * mm, "end": v(28.1, 44.58) * mm});
            skLineSegment(sketch, "E505", {"start": v(28.5, 43.97) * mm, "end": v(28.27, 44.26) * mm});
            skLineSegment(sketch, "E506", {"start": v(29.08, 43.46) * mm, "end": v(28.5, 43.97) * mm});
            skLineSegment(sketch, "E507", {"start": v(29.75, 43.01) * mm, "end": v(29.08, 43.46) * mm});
            skLineSegment(sketch, "E508", {"start": v(30.9, 42.37) * mm, "end": v(29.75, 43.01) * mm});
            skLineSegment(sketch, "E509", {"start": v(32.02, 45.83) * mm, "end": v(30.9, 42.37) * mm});
            skLineSegment(sketch, "E510", {"start": v(32.73, 49.68) * mm, "end": v(32.02, 45.83) * mm});
            skLineSegment(sketch, "E511", {"start": v(32.92, 53.6) * mm, "end": v(32.73, 49.68) * mm});
            skLineSegment(sketch, "E512", {"start": v(32.6, 57.5) * mm, "end": v(32.92, 53.6) * mm});
            skLineSegment(sketch, "E513", {"start": v(31.77, 61.33) * mm, "end": v(32.6, 57.5) * mm});
            skLineSegment(sketch, "E514", {"start": v(30.44, 65.02) * mm, "end": v(31.77, 61.33) * mm});
            skLineSegment(sketch, "E515", {"start": v(28.64, 68.5) * mm, "end": v(30.44, 65.02) * mm});
            skLineSegment(sketch, "E516", {"start": v(26.4, 71.71) * mm, "end": v(28.64, 68.5) * mm});
            skLineSegment(sketch, "E517", {"start": v(23.75, 74.6) * mm, "end": v(26.4, 71.71) * mm});
            skLineSegment(sketch, "E518", {"start": v(20.74, 77.12) * mm, "end": v(23.75, 74.6) * mm});
            skLineSegment(sketch, "E519", {"start": v(17.44, 79.22) * mm, "end": v(20.74, 77.12) * mm});
            skLineSegment(sketch, "E520", {"start": v(13.88, 80.87) * mm, "end": v(17.44, 79.22) * mm});
            skLineSegment(sketch, "E521", {"start": v(10.14, 82.04) * mm, "end": v(13.88, 80.87) * mm});
            skLineSegment(sketch, "E522", {"start": v(6.27, 82.7) * mm, "end": v(10.14, 82.04) * mm});
            skLineSegment(sketch, "E523", {"start": v(2.36, 82.85) * mm, "end": v(6.27, 82.7) * mm});
            skLineSegment(sketch, "E524", {"start": v(9.42, 40.3) * mm, "end": v(9.44, 40.25) * mm});
            skLineSegment(sketch, "E525", {"start": v(9.4, 40.35) * mm, "end": v(9.42, 40.3) * mm});
            skLineSegment(sketch, "E526", {"start": v(9.38, 40.46) * mm, "end": v(9.4, 40.35) * mm});
            skLineSegment(sketch, "E527", {"start": v(9.32, 40.67) * mm, "end": v(9.38, 40.46) * mm});
            skLineSegment(sketch, "E528", {"start": v(8.43, 43.43) * mm, "end": v(9.32, 40.67) * mm});
            skLineSegment(sketch, "E529", {"start": v(7.25, 46.57) * mm, "end": v(8.43, 43.43) * mm});
            skLineSegment(sketch, "E530", {"start": v(6.8, 48.21) * mm, "end": v(7.25, 46.57) * mm});
            skLineSegment(sketch, "E531", {"start": v(6.69, 49.08) * mm, "end": v(6.8, 48.21) * mm});
            skLineSegment(sketch, "E532", {"start": v(6.69, 49.95) * mm, "end": v(6.69, 49.08) * mm});
            skLineSegment(sketch, "E533", {"start": v(6.82, 50.82) * mm, "end": v(6.69, 49.95) * mm});
            skLineSegment(sketch, "E534", {"start": v(7.06, 51.65) * mm, "end": v(6.82, 50.82) * mm});
            skLineSegment(sketch, "E535", {"start": v(7.74, 53.23) * mm, "end": v(7.06, 51.65) * mm});
            skLineSegment(sketch, "E536", {"start": v(8.33, 54.07) * mm, "end": v(7.74, 53.23) * mm});
            skLineSegment(sketch, "E537", {"start": v(8.35, 54.13) * mm, "end": v(8.33, 54.07) * mm});
            skLineSegment(sketch, "E538", {"start": v(8.36, 54.2) * mm, "end": v(8.35, 54.13) * mm});
            skLineSegment(sketch, "E539", {"start": v(8.34, 54.43) * mm, "end": v(8.36, 54.2) * mm});
            skLineSegment(sketch, "E540", {"start": v(8.3, 54.67) * mm, "end": v(8.34, 54.43) * mm});
            skLineSegment(sketch, "E541", {"start": v(8.28, 54.76) * mm, "end": v(8.3, 54.67) * mm});
            skLineSegment(sketch, "E542", {"start": v(8.25, 54.8) * mm, "end": v(8.28, 54.76) * mm});
            skLineSegment(sketch, "E543", {"start": v(6.93, 56.34) * mm, "end": v(8.25, 54.8) * mm});
            skLineSegment(sketch, "E544", {"start": v(6.76, 56.49) * mm, "end": v(6.93, 56.34) * mm});
            skLineSegment(sketch, "E545", {"start": v(6.58, 56.6) * mm, "end": v(6.76, 56.49) * mm});
            skLineSegment(sketch, "E546", {"start": v(6.4, 56.67) * mm, "end": v(6.58, 56.6) * mm});
            skLineSegment(sketch, "E547", {"start": v(6.2, 56.7) * mm, "end": v(6.4, 56.67) * mm});
            skLineSegment(sketch, "E548", {"start": v(5.74, 56.63) * mm, "end": v(6.2, 56.7) * mm});
            skLineSegment(sketch, "E549", {"start": v(5.54, 56.57) * mm, "end": v(5.74, 56.63) * mm});
            skLineSegment(sketch, "E550", {"start": v(5.35, 56.47) * mm, "end": v(5.54, 56.57) * mm});
            skLineSegment(sketch, "E551", {"start": v(3.64, 54.94) * mm, "end": v(5.35, 56.47) * mm});
            skLineSegment(sketch, "E552", {"start": v(2.98, 55.83) * mm, "end": v(3.64, 54.94) * mm});
            skLineSegment(sketch, "E553", {"start": v(1.07, 58.52) * mm, "end": v(2.98, 55.83) * mm});
            skLineSegment(sketch, "E554", {"start": v(-0.7, 61.31) * mm, "end": v(1.07, 58.52) * mm});
            skLineSegment(sketch, "E555", {"start": v(-0.7, 61.31) * mm, "end": v(-2.35, 64.16) * mm});
            skLineSegment(sketch, "E556", {"start": v(-2.35, 64.16) * mm, "end": v(-3.78, 66.97) * mm});
            skLineSegment(sketch, "E557", {"start": v(-13.7, 67.26) * mm, "end": v(-3.78, 66.97) * mm});
            skLineSegment(sketch, "E558", {"start": v(-14.62, 65.97) * mm, "end": v(-13.7, 67.26) * mm});
            skLineSegment(sketch, "E559", {"start": v(-14.85, 65.62) * mm, "end": v(-14.62, 65.97) * mm});
            skLineSegment(sketch, "E560", {"start": v(-14.79, 65.55) * mm, "end": v(-14.85, 65.62) * mm});
            skLineSegment(sketch, "E561", {"start": v(-14.48, 65.28) * mm, "end": v(-14.79, 65.55) * mm});
            skLineSegment(sketch, "E562", {"start": v(-14.34, 65.2) * mm, "end": v(-14.48, 65.28) * mm});
            skLineSegment(sketch, "E563", {"start": v(-14.2, 65.14) * mm, "end": v(-14.34, 65.2) * mm});
            skLineSegment(sketch, "E564", {"start": v(-13.34, 65.04) * mm, "end": v(-14.2, 65.14) * mm});
            skLineSegment(sketch, "E565", {"start": v(-12.5, 64.74) * mm, "end": v(-13.34, 65.04) * mm});
            skLineSegment(sketch, "E566", {"start": v(-12.07, 64.54) * mm, "end": v(-12.5, 64.74) * mm});
            skLineSegment(sketch, "E567", {"start": v(-11.85, 64.42) * mm, "end": v(-12.07, 64.54) * mm});
            skLineSegment(sketch, "E568", {"start": v(-11.64, 64.26) * mm, "end": v(-11.85, 64.42) * mm});
            skLineSegment(sketch, "E569", {"start": v(-11.53, 64.14) * mm, "end": v(-11.64, 64.26) * mm});
            skLineSegment(sketch, "E570", {"start": v(-11.46, 64) * mm, "end": v(-11.53, 64.14) * mm});
            skLineSegment(sketch, "E571", {"start": v(-11.42, 63.86) * mm, "end": v(-11.46, 64) * mm});
            skLineSegment(sketch, "E572", {"start": v(-11.4, 63.7) * mm, "end": v(-11.42, 63.86) * mm});
            skLineSegment(sketch, "E573", {"start": v(-11.45, 63.22) * mm, "end": v(-11.4, 63.7) * mm});
            skLineSegment(sketch, "E574", {"start": v(-11.82, 61.52) * mm, "end": v(-11.45, 63.22) * mm});
            skLineSegment(sketch, "E575", {"start": v(-12.44, 59.88) * mm, "end": v(-11.82, 61.52) * mm});
            skLineSegment(sketch, "E576", {"start": v(-13.05, 58.29) * mm, "end": v(-12.44, 59.88) * mm});
            skLineSegment(sketch, "E577", {"start": v(-13.2, 57.88) * mm, "end": v(-13.05, 58.29) * mm});
            skLineSegment(sketch, "E578", {"start": v(-13.27, 57.5) * mm, "end": v(-13.2, 57.88) * mm});
            skLineSegment(sketch, "E579", {"start": v(-13.27, 57.35) * mm, "end": v(-13.27, 57.5) * mm});
            skLineSegment(sketch, "E580", {"start": v(-13.22, 57.2) * mm, "end": v(-13.27, 57.35) * mm});
            skLineSegment(sketch, "E581", {"start": v(-13.14, 57.07) * mm, "end": v(-13.22, 57.2) * mm});
            skLineSegment(sketch, "E582", {"start": v(-13.03, 56.94) * mm, "end": v(-13.14, 57.07) * mm});
            skLineSegment(sketch, "E583", {"start": v(-12.9, 56.84) * mm, "end": v(-13.03, 56.94) * mm});
            skLineSegment(sketch, "E584", {"start": v(-12.73, 56.76) * mm, "end": v(-12.9, 56.84) * mm});
            skLineSegment(sketch, "E585", {"start": v(-12.33, 56.6) * mm, "end": v(-12.73, 56.76) * mm});
            skLineSegment(sketch, "E586", {"start": v(-11.54, 56.25) * mm, "end": v(-12.33, 56.6) * mm});
            skLineSegment(sketch, "E587", {"start": v(-10.75, 55.84) * mm, "end": v(-11.54, 56.25) * mm});
            skLineSegment(sketch, "E588", {"start": v(-10.58, 55.78) * mm, "end": v(-10.75, 55.84) * mm});
            skLineSegment(sketch, "E589", {"start": v(-10.41, 55.74) * mm, "end": v(-10.58, 55.78) * mm});
            skLineSegment(sketch, "E590", {"start": v(-10.35, 55.74) * mm, "end": v(-10.41, 55.74) * mm});
            skLineSegment(sketch, "E591", {"start": v(-10.3, 55.75) * mm, "end": v(-10.35, 55.74) * mm});
            skLineSegment(sketch, "E592", {"start": v(-10.14, 55.8) * mm, "end": v(-10.3, 55.75) * mm});
            skLineSegment(sketch, "E593", {"start": v(-10, 55.89) * mm, "end": v(-10.14, 55.8) * mm});
            skLineSegment(sketch, "E594", {"start": v(-9.86, 56) * mm, "end": v(-10, 55.89) * mm});
            skLineSegment(sketch, "E595", {"start": v(-9.62, 56.31) * mm, "end": v(-9.86, 56) * mm});
            skLineSegment(sketch, "E596", {"start": v(-9.24, 57.05) * mm, "end": v(-9.62, 56.31) * mm});
            skLineSegment(sketch, "E597", {"start": v(-8.88, 57.88) * mm, "end": v(-9.24, 57.05) * mm});
            skLineSegment(sketch, "E598", {"start": v(-8.78, 58.1) * mm, "end": v(-8.88, 57.88) * mm});
            skLineSegment(sketch, "E599", {"start": v(-8.7, 58.22) * mm, "end": v(-8.78, 58.1) * mm});
            skLineSegment(sketch, "E600", {"start": v(-8.6, 58.33) * mm, "end": v(-8.7, 58.22) * mm});
            skLineSegment(sketch, "E601", {"start": v(-8.47, 58.42) * mm, "end": v(-8.6, 58.33) * mm});
            skLineSegment(sketch, "E602", {"start": v(-8.32, 58.47) * mm, "end": v(-8.47, 58.42) * mm});
            skLineSegment(sketch, "E603", {"start": v(-8.17, 58.49) * mm, "end": v(-8.32, 58.47) * mm});
            skLineSegment(sketch, "E604", {"start": v(-8.02, 58.48) * mm, "end": v(-8.17, 58.49) * mm});
            skLineSegment(sketch, "E605", {"start": v(-7.76, 58.43) * mm, "end": v(-8.02, 58.48) * mm});
            skLineSegment(sketch, "E606", {"start": v(-7.52, 58.33) * mm, "end": v(-7.76, 58.43) * mm});
            skLineSegment(sketch, "E607", {"start": v(-7.12, 58.09) * mm, "end": v(-7.52, 58.33) * mm});
            skLineSegment(sketch, "E608", {"start": v(-7.12, 58.09) * mm, "end": v(-6.42, 57.53) * mm});
            skLineSegment(sketch, "E609", {"start": v(-6.42, 57.53) * mm, "end": v(-5.23, 56.22) * mm});
            skLineSegment(sketch, "E610", {"start": v(-3.46, 53.23) * mm, "end": v(-5.23, 56.22) * mm});
            skLineSegment(sketch, "E611", {"start": v(-2.22, 50.86) * mm, "end": v(-3.46, 53.23) * mm});
            skLineSegment(sketch, "E612", {"start": v(-1.11, 48.4) * mm, "end": v(-2.22, 50.86) * mm});
            skLineSegment(sketch, "E613", {"start": v(0.39, 43.27) * mm, "end": v(-1.11, 48.4) * mm});
            skLineSegment(sketch, "E614", {"start": v(1.02, 40.68) * mm, "end": v(0.39, 43.27) * mm});
            skLineSegment(sketch, "E615", {"start": v(1.53, 38.02) * mm, "end": v(1.02, 40.68) * mm});
            skLineSegment(sketch, "E616", {"start": v(1.59, 37.32) * mm, "end": v(1.53, 38.02) * mm});
            skLineSegment(sketch, "E617", {"start": v(1.51, 36.62) * mm, "end": v(1.59, 37.32) * mm});
            skLineSegment(sketch, "E618", {"start": v(1.35, 35.94) * mm, "end": v(1.51, 36.62) * mm});
            skLineSegment(sketch, "E619", {"start": v(1.29, 35.76) * mm, "end": v(1.35, 35.94) * mm});
            skLineSegment(sketch, "E620", {"start": v(1.2, 35.6) * mm, "end": v(1.29, 35.76) * mm});
            skLineSegment(sketch, "E621", {"start": v(1.17, 35.54) * mm, "end": v(1.2, 35.6) * mm});
            skLineSegment(sketch, "E622", {"start": v(1.3, 35.51) * mm, "end": v(1.17, 35.54) * mm});
            skLineSegment(sketch, "E623", {"start": v(1.65, 35.36) * mm, "end": v(1.3, 35.51) * mm});
            skLineSegment(sketch, "E624", {"start": v(2.22, 35.01) * mm, "end": v(1.65, 35.36) * mm});
            skLineSegment(sketch, "E625", {"start": v(2.78, 34.67) * mm, "end": v(2.22, 35.01) * mm});
            skLineSegment(sketch, "E626", {"start": v(3.09, 34.46) * mm, "end": v(2.78, 34.67) * mm});
            skLineSegment(sketch, "E627", {"start": v(3.2, 34.34) * mm, "end": v(3.09, 34.46) * mm});
            skLineSegment(sketch, "E628", {"start": v(3.35, 34.73) * mm, "end": v(3.2, 34.34) * mm});
            skLineSegment(sketch, "E629", {"start": v(3.66, 35.22) * mm, "end": v(3.35, 34.73) * mm});
            skLineSegment(sketch, "E630", {"start": v(4.44, 36.02) * mm, "end": v(3.66, 35.22) * mm});
            skLineSegment(sketch, "E631", {"start": v(5.96, 37.56) * mm, "end": v(4.44, 36.02) * mm});
            skLineSegment(sketch, "E632", {"start": v(6.75, 38.33) * mm, "end": v(5.96, 37.56) * mm});
            skLineSegment(sketch, "E633", {"start": v(7.67, 38.92) * mm, "end": v(6.75, 38.33) * mm});
            skLineSegment(sketch, "E634", {"start": v(8.63, 39.5) * mm, "end": v(7.67, 38.92) * mm});
            skLineSegment(sketch, "E635", {"start": v(8.9, 39.63) * mm, "end": v(8.63, 39.5) * mm});
            skLineSegment(sketch, "E636", {"start": v(9.19, 39.73) * mm, "end": v(8.9, 39.63) * mm});
            skLineSegment(sketch, "E637", {"start": v(9.5, 39.77) * mm, "end": v(9.19, 39.73) * mm});
            skLineSegment(sketch, "E638", {"start": v(9.53, 39.77) * mm, "end": v(9.5, 39.77) * mm});
            skLineSegment(sketch, "E639", {"start": v(9.53, 39.89) * mm, "end": v(9.53, 39.77) * mm});
            skLineSegment(sketch, "E640", {"start": v(9.44, 40.25) * mm, "end": v(9.53, 39.89) * mm});
            skLineSegment(sketch, "E641", {"start": v(21.55, 54.4) * mm, "end": v(22.2, 53) * mm});
            skLineSegment(sketch, "E642", {"start": v(19, 59.7) * mm, "end": v(21.55, 54.4) * mm});
            skLineSegment(sketch, "E643", {"start": v(17.93, 62.44) * mm, "end": v(19, 59.7) * mm});
            skLineSegment(sketch, "E644", {"start": v(17.7, 63.17) * mm, "end": v(17.93, 62.44) * mm});
            skLineSegment(sketch, "E645", {"start": v(17.63, 63.94) * mm, "end": v(17.7, 63.17) * mm});
            skLineSegment(sketch, "E646", {"start": v(17.7, 65.43) * mm, "end": v(17.63, 63.94) * mm});
            skLineSegment(sketch, "E647", {"start": v(17.83, 66.88) * mm, "end": v(17.7, 65.43) * mm});
            skLineSegment(sketch, "E648", {"start": v(17.83, 67.05) * mm, "end": v(17.83, 66.88) * mm});
            skLineSegment(sketch, "E649", {"start": v(17.8, 67.2) * mm, "end": v(17.83, 67.05) * mm});
            skLineSegment(sketch, "E650", {"start": v(17.8, 67.25) * mm, "end": v(17.8, 67.2) * mm});
            skLineSegment(sketch, "E651", {"start": v(17.76, 67.28) * mm, "end": v(17.8, 67.25) * mm});
            skLineSegment(sketch, "E652", {"start": v(17.7, 67.31) * mm, "end": v(17.76, 67.28) * mm});
            skLineSegment(sketch, "E653", {"start": v(17.07, 67.66) * mm, "end": v(17.7, 67.31) * mm});
            skLineSegment(sketch, "E654", {"start": v(16.76, 67.85) * mm, "end": v(17.07, 67.66) * mm});
            skLineSegment(sketch, "E655", {"start": v(16.71, 67.87) * mm, "end": v(16.76, 67.85) * mm});
            skLineSegment(sketch, "E656", {"start": v(16.67, 67.88) * mm, "end": v(16.71, 67.87) * mm});
            skLineSegment(sketch, "E657", {"start": v(16.63, 67.88) * mm, "end": v(16.67, 67.88) * mm});
            skLineSegment(sketch, "E658", {"start": v(16.58, 67.88) * mm, "end": v(16.63, 67.88) * mm});
            skLineSegment(sketch, "E659", {"start": v(15.88, 67.63) * mm, "end": v(16.58, 67.88) * mm});
            skLineSegment(sketch, "E660", {"start": v(14.42, 67.35) * mm, "end": v(15.88, 67.63) * mm});
            skLineSegment(sketch, "E661", {"start": v(12.92, 67.26) * mm, "end": v(14.42, 67.35) * mm});
            skLineSegment(sketch, "E662", {"start": v(11.44, 67.4) * mm, "end": v(12.92, 67.26) * mm});
            skLineSegment(sketch, "E663", {"start": v(9.96, 67.53) * mm, "end": v(11.44, 67.4) * mm});
            skLineSegment(sketch, "E664", {"start": v(8.54, 67.94) * mm, "end": v(9.96, 67.53) * mm});
            skLineSegment(sketch, "E665", {"start": v(8.4, 67.97) * mm, "end": v(8.54, 67.94) * mm});
            skLineSegment(sketch, "E666", {"start": v(8.26, 67.97) * mm, "end": v(8.4, 67.97) * mm});
            skLineSegment(sketch, "E667", {"start": v(8.23, 67.96) * mm, "end": v(8.26, 67.97) * mm});
            skLineSegment(sketch, "E668", {"start": v(8.2, 67.95) * mm, "end": v(8.23, 67.96) * mm});
            skLineSegment(sketch, "E669", {"start": v(8.09, 67.87) * mm, "end": v(8.2, 67.95) * mm});
            skLineSegment(sketch, "E670", {"start": v(7.61, 67.34) * mm, "end": v(8.09, 67.87) * mm});
            skLineSegment(sketch, "E671", {"start": v(7.15, 66.8) * mm, "end": v(7.61, 67.34) * mm});
            skLineSegment(sketch, "E672", {"start": v(6.98, 66.52) * mm, "end": v(7.15, 66.8) * mm});
            skLineSegment(sketch, "E673", {"start": v(6.93, 66.4) * mm, "end": v(6.98, 66.52) * mm});
            skLineSegment(sketch, "E674", {"start": v(6.9, 66.25) * mm, "end": v(6.93, 66.4) * mm});
            skLineSegment(sketch, "E675", {"start": v(6.91, 66.2) * mm, "end": v(6.9, 66.25) * mm});
            skLineSegment(sketch, "E676", {"start": v(6.94, 66.18) * mm, "end": v(6.91, 66.2) * mm});
            skLineSegment(sketch, "E677", {"start": v(7.07, 66.11) * mm, "end": v(6.94, 66.18) * mm});
            skLineSegment(sketch, "E678", {"start": v(7.25, 66.05) * mm, "end": v(7.07, 66.11) * mm});
            skLineSegment(sketch, "E679", {"start": v(8, 65.76) * mm, "end": v(7.25, 66.05) * mm});
            skLineSegment(sketch, "E680", {"start": v(9.28, 65.08) * mm, "end": v(8, 65.76) * mm});
            skLineSegment(sketch, "E681", {"start": v(9.91, 64.7) * mm, "end": v(9.28, 65.08) * mm});
            skLineSegment(sketch, "E682", {"start": v(10.24, 64.48) * mm, "end": v(9.91, 64.7) * mm});
            skLineSegment(sketch, "E683", {"start": v(10.54, 64.2) * mm, "end": v(10.24, 64.48) * mm});
            skLineSegment(sketch, "E684", {"start": v(10.78, 63.87) * mm, "end": v(10.54, 64.2) * mm});
            skLineSegment(sketch, "E685", {"start": v(10.96, 63.48) * mm, "end": v(10.78, 63.87) * mm});
            skLineSegment(sketch, "E686", {"start": v(11.01, 63.26) * mm, "end": v(10.96, 63.48) * mm});
            skLineSegment(sketch, "E687", {"start": v(11.03, 63.03) * mm, "end": v(11.01, 63.26) * mm});
            skLineSegment(sketch, "E688", {"start": v(11, 62.8) * mm, "end": v(11.03, 63.03) * mm});
            skLineSegment(sketch, "E689", {"start": v(10.91, 62.58) * mm, "end": v(11, 62.8) * mm});
            skLineSegment(sketch, "E690", {"start": v(10.02, 61.35) * mm, "end": v(10.91, 62.58) * mm});
            skLineSegment(sketch, "E691", {"start": v(9.3, 60.09) * mm, "end": v(10.02, 61.35) * mm});
            skLineSegment(sketch, "E692", {"start": v(8.86, 59.45) * mm, "end": v(9.3, 60.09) * mm});
            skLineSegment(sketch, "E693", {"start": v(8.29, 58.9) * mm, "end": v(8.86, 59.45) * mm});
            skLineSegment(sketch, "E694", {"start": v(8.01, 58.66) * mm, "end": v(8.29, 58.9) * mm});
            skLineSegment(sketch, "E695", {"start": v(7.92, 58.55) * mm, "end": v(8.01, 58.66) * mm});
            skLineSegment(sketch, "E696", {"start": v(7.85, 58.44) * mm, "end": v(7.92, 58.55) * mm});
            skLineSegment(sketch, "E697", {"start": v(7.82, 58.33) * mm, "end": v(7.85, 58.44) * mm});
            skLineSegment(sketch, "E698", {"start": v(7.8, 58.2) * mm, "end": v(7.82, 58.33) * mm});
            skLineSegment(sketch, "E699", {"start": v(7.82, 58.06) * mm, "end": v(7.8, 58.2) * mm});
            skLineSegment(sketch, "E700", {"start": v(7.86, 57.93) * mm, "end": v(7.82, 58.06) * mm});
            skLineSegment(sketch, "E701", {"start": v(8.02, 57.65) * mm, "end": v(7.86, 57.93) * mm});
            skLineSegment(sketch, "E702", {"start": v(8.22, 57.37) * mm, "end": v(8.02, 57.65) * mm});
            skLineSegment(sketch, "E703", {"start": v(8.67, 56.82) * mm, "end": v(8.22, 57.37) * mm});
            skLineSegment(sketch, "E704", {"start": v(9.16, 56.28) * mm, "end": v(8.67, 56.82) * mm});
            skLineSegment(sketch, "E705", {"start": v(9.41, 56.02) * mm, "end": v(9.16, 56.28) * mm});
            skLineSegment(sketch, "E706", {"start": v(9.53, 55.93) * mm, "end": v(9.41, 56.02) * mm});
            skLineSegment(sketch, "E707", {"start": v(9.65, 55.86) * mm, "end": v(9.53, 55.93) * mm});
            skLineSegment(sketch, "E708", {"start": v(9.78, 55.8) * mm, "end": v(9.65, 55.86) * mm});
            skLineSegment(sketch, "E709", {"start": v(9.93, 55.77) * mm, "end": v(9.78, 55.8) * mm});
            skLineSegment(sketch, "E710", {"start": v(10.27, 55.73) * mm, "end": v(9.93, 55.77) * mm});
            skLineSegment(sketch, "E711", {"start": v(10.33, 55.73) * mm, "end": v(10.27, 55.73) * mm});
            skLineSegment(sketch, "E712", {"start": v(10.37, 55.74) * mm, "end": v(10.33, 55.73) * mm});
            skLineSegment(sketch, "E713", {"start": v(10.42, 55.76) * mm, "end": v(10.37, 55.74) * mm});
            skLineSegment(sketch, "E714", {"start": v(10.46, 55.78) * mm, "end": v(10.42, 55.76) * mm});
            skLineSegment(sketch, "E715", {"start": v(10.74, 56.02) * mm, "end": v(10.46, 55.78) * mm});
            skLineSegment(sketch, "E716", {"start": v(11.08, 56.24) * mm, "end": v(10.74, 56.02) * mm});
            skLineSegment(sketch, "E717", {"start": v(11.3, 56.33) * mm, "end": v(11.08, 56.24) * mm});
            skLineSegment(sketch, "E718", {"start": v(11.42, 56.36) * mm, "end": v(11.3, 56.33) * mm});
            skLineSegment(sketch, "E719", {"start": v(11.55, 56.36) * mm, "end": v(11.42, 56.36) * mm});
            skLineSegment(sketch, "E720", {"start": v(11.69, 56.35) * mm, "end": v(11.55, 56.36) * mm});
            skLineSegment(sketch, "E721", {"start": v(11.82, 56.3) * mm, "end": v(11.69, 56.35) * mm});
            skLineSegment(sketch, "E722", {"start": v(12.03, 56.2) * mm, "end": v(11.82, 56.3) * mm});
            skLineSegment(sketch, "E723", {"start": v(12.2, 56.04) * mm, "end": v(12.03, 56.2) * mm});
            skLineSegment(sketch, "E724", {"start": v(12.36, 55.86) * mm, "end": v(12.2, 56.04) * mm});
            skLineSegment(sketch, "E725", {"start": v(13.71, 53.22) * mm, "end": v(12.36, 55.86) * mm});
            skLineSegment(sketch, "E726", {"start": v(17.57, 44.28) * mm, "end": v(13.71, 53.22) * mm});
            skLineSegment(sketch, "E727", {"start": v(17.94, 43.07) * mm, "end": v(17.57, 44.28) * mm});
            skLineSegment(sketch, "E728", {"start": v(17.96, 42.72) * mm, "end": v(17.94, 43.07) * mm});
            skLineSegment(sketch, "E729", {"start": v(17.93, 42.38) * mm, "end": v(17.96, 42.72) * mm});
            skLineSegment(sketch, "E730", {"start": v(17.86, 42.05) * mm, "end": v(17.93, 42.38) * mm});
            skLineSegment(sketch, "E731", {"start": v(17.74, 41.73) * mm, "end": v(17.86, 42.05) * mm});
            skLineSegment(sketch, "E732", {"start": v(17.4, 41.17) * mm, "end": v(17.74, 41.73) * mm});
            skLineSegment(sketch, "E733", {"start": v(17, 40.66) * mm, "end": v(17.4, 41.17) * mm});
            skLineSegment(sketch, "E734", {"start": v(16.12, 39.78) * mm, "end": v(17, 40.66) * mm});
            skLineSegment(sketch, "E735", {"start": v(14.35, 38.17) * mm, "end": v(16.12, 39.78) * mm});
            skLineSegment(sketch, "E736", {"start": v(14.14, 37.95) * mm, "end": v(14.35, 38.17) * mm});
            skLineSegment(sketch, "E737", {"start": v(14.04, 37.83) * mm, "end": v(14.14, 37.95) * mm});
            skLineSegment(sketch, "E738", {"start": v(14, 37.77) * mm, "end": v(14.04, 37.83) * mm});
            skLineSegment(sketch, "E739", {"start": v(14.22, 37.55) * mm, "end": v(14, 37.77) * mm});
            skLineSegment(sketch, "E740", {"start": v(14.7, 37.07) * mm, "end": v(14.22, 37.55) * mm});
            skLineSegment(sketch, "E741", {"start": v(15.03, 36.62) * mm, "end": v(14.7, 37.07) * mm});
            skLineSegment(sketch, "E742", {"start": v(15.3, 36.42) * mm, "end": v(15.03, 36.62) * mm});
            skLineSegment(sketch, "E743", {"start": v(16.41, 37.12) * mm, "end": v(15.3, 36.42) * mm});
            skLineSegment(sketch, "E744", {"start": v(17.8, 37.7) * mm, "end": v(16.41, 37.12) * mm});
            skLineSegment(sketch, "E745", {"start": v(19.23, 38.19) * mm, "end": v(17.8, 37.7) * mm});
            skLineSegment(sketch, "E746", {"start": v(20.7, 38.5) * mm, "end": v(19.23, 38.19) * mm});
            skLineSegment(sketch, "E747", {"start": v(22.74, 38.66) * mm, "end": v(20.7, 38.5) * mm});
            skLineSegment(sketch, "E748", {"start": v(24.8, 38.64) * mm, "end": v(22.74, 38.66) * mm});
            skLineSegment(sketch, "E749", {"start": v(26.8, 38.16) * mm, "end": v(24.8, 38.64) * mm});
            skLineSegment(sketch, "E750", {"start": v(28.53, 37.54) * mm, "end": v(26.8, 38.16) * mm});
            skLineSegment(sketch, "E751", {"start": v(28.82, 38.03) * mm, "end": v(28.53, 37.54) * mm});
            skLineSegment(sketch, "E752", {"start": v(29.2, 38.7) * mm, "end": v(28.82, 38.03) * mm});
            skLineSegment(sketch, "E753", {"start": v(29.44, 39.15) * mm, "end": v(29.2, 38.7) * mm});
            skLineSegment(sketch, "E754", {"start": v(28.9, 39.42) * mm, "end": v(29.44, 39.15) * mm});
            skLineSegment(sketch, "E755", {"start": v(28.21, 39.98) * mm, "end": v(28.9, 39.42) * mm});
            skLineSegment(sketch, "E756", {"start": v(27.12, 41.3) * mm, "end": v(28.21, 39.98) * mm});
            skLineSegment(sketch, "E757", {"start": v(26.14, 42.7) * mm, "end": v(27.12, 41.3) * mm});
            skLineSegment(sketch, "E758", {"start": v(25.82, 43.52) * mm, "end": v(26.14, 42.7) * mm});
            skLineSegment(sketch, "E759", {"start": v(25.64, 44.35) * mm, "end": v(25.82, 43.52) * mm});
            skLineSegment(sketch, "E760", {"start": v(24.97, 46.43) * mm, "end": v(25.64, 44.35) * mm});
            skLineSegment(sketch, "E761", {"start": v(24.05, 48.82) * mm, "end": v(24.97, 46.43) * mm});
            skLineSegment(sketch, "E762", {"start": v(22.2, 53) * mm, "end": v(24.05, 48.82) * mm});
            skLineSegment(sketch, "E763", {"start": v(-22.46, 38.1) * mm, "end": v(-22.34, 38.14) * mm});
            skLineSegment(sketch, "E764", {"start": v(-22.51, 38.08) * mm, "end": v(-22.46, 38.1) * mm});
            skLineSegment(sketch, "E765", {"start": v(-22.14, 37.13) * mm, "end": v(-22.51, 38.08) * mm});
            skLineSegment(sketch, "E766", {"start": v(-21.69, 36.5) * mm, "end": v(-22.14, 37.13) * mm});
            skLineSegment(sketch, "E767", {"start": v(-21.4, 36.74) * mm, "end": v(-21.69, 36.5) * mm});
            skLineSegment(sketch, "E768", {"start": v(-20.97, 37.01) * mm, "end": v(-21.4, 36.74) * mm});
            skLineSegment(sketch, "E769", {"start": v(-20.13, 37.53) * mm, "end": v(-20.97, 37.01) * mm});
            skLineSegment(sketch, "E770", {"start": v(-18.27, 38.21) * mm, "end": v(-20.13, 37.53) * mm});
            skLineSegment(sketch, "E771", {"start": v(-17.28, 38.42) * mm, "end": v(-18.27, 38.21) * mm});
            skLineSegment(sketch, "E772", {"start": v(-16.3, 38.48) * mm, "end": v(-17.28, 38.42) * mm});
            skLineSegment(sketch, "E773", {"start": v(-14.34, 38.47) * mm, "end": v(-16.3, 38.48) * mm});
            skLineSegment(sketch, "E774", {"start": v(-12.17, 38.28) * mm, "end": v(-14.34, 38.47) * mm});
            skLineSegment(sketch, "E775", {"start": v(-12.17, 39.04) * mm, "end": v(-12.17, 38.28) * mm});
            skLineSegment(sketch, "E776", {"start": v(-12.2, 39.27) * mm, "end": v(-12.17, 39.04) * mm});
            skLineSegment(sketch, "E777", {"start": v(-12.22, 39.35) * mm, "end": v(-12.2, 39.27) * mm});
            skLineSegment(sketch, "E778", {"start": v(-12.26, 39.42) * mm, "end": v(-12.22, 39.35) * mm});
            skLineSegment(sketch, "E779", {"start": v(-12.31, 39.49) * mm, "end": v(-12.26, 39.42) * mm});
            skLineSegment(sketch, "E780", {"start": v(-12.38, 39.55) * mm, "end": v(-12.31, 39.49) * mm});
            skLineSegment(sketch, "E781", {"start": v(-12.58, 39.68) * mm, "end": v(-12.38, 39.55) * mm});
            skLineSegment(sketch, "E782", {"start": v(-13.52, 40.19) * mm, "end": v(-12.58, 39.68) * mm});
            skLineSegment(sketch, "E783", {"start": v(-13.92, 40.63) * mm, "end": v(-13.52, 40.19) * mm});
            skLineSegment(sketch, "E784", {"start": v(-14.22, 41.14) * mm, "end": v(-13.92, 40.63) * mm});
            skLineSegment(sketch, "E785", {"start": v(-14.4, 41.69) * mm, "end": v(-14.22, 41.14) * mm});
            skLineSegment(sketch, "E786", {"start": v(-14.48, 42.26) * mm, "end": v(-14.4, 41.69) * mm});
            skLineSegment(sketch, "E787", {"start": v(-14.32, 43.35) * mm, "end": v(-14.48, 42.26) * mm});
            skLineSegment(sketch, "E788", {"start": v(-13.72, 45.37) * mm, "end": v(-14.32, 43.35) * mm});
            skLineSegment(sketch, "E789", {"start": v(-12.38, 49.35) * mm, "end": v(-13.72, 45.37) * mm});
            skLineSegment(sketch, "E790", {"start": v(-10.8, 53.17) * mm, "end": v(-12.38, 49.35) * mm});
            skLineSegment(sketch, "E791", {"start": v(-10.78, 53.55) * mm, "end": v(-10.8, 53.17) * mm});
            skLineSegment(sketch, "E792", {"start": v(-10.8, 53.72) * mm, "end": v(-10.78, 53.55) * mm});
            skLineSegment(sketch, "E793", {"start": v(-10.83, 53.77) * mm, "end": v(-10.8, 53.72) * mm});
            skLineSegment(sketch, "E794", {"start": v(-10.86, 53.81) * mm, "end": v(-10.83, 53.77) * mm});
            skLineSegment(sketch, "E795", {"start": v(-11, 53.93) * mm, "end": v(-10.86, 53.81) * mm});
            skLineSegment(sketch, "E796", {"start": v(-11.17, 54.04) * mm, "end": v(-11, 53.93) * mm});
            skLineSegment(sketch, "E797", {"start": v(-11.55, 54.28) * mm, "end": v(-11.17, 54.04) * mm});
            skLineSegment(sketch, "E798", {"start": v(-11.69, 54.36) * mm, "end": v(-11.55, 54.28) * mm});
            skLineSegment(sketch, "E799", {"start": v(-11.82, 54.43) * mm, "end": v(-11.69, 54.36) * mm});
            skLineSegment(sketch, "E800", {"start": v(-12.09, 54.58) * mm, "end": v(-11.82, 54.43) * mm});
            skLineSegment(sketch, "E801", {"start": v(-12.65, 54.85) * mm, "end": v(-12.09, 54.58) * mm});
            skLineSegment(sketch, "E802", {"start": v(-13.11, 55.05) * mm, "end": v(-12.65, 54.85) * mm});
            skLineSegment(sketch, "E803", {"start": v(-13.5, 55.2) * mm, "end": v(-13.11, 55.05) * mm});
            skLineSegment(sketch, "E804", {"start": v(-13.58, 55.22) * mm, "end": v(-13.5, 55.2) * mm});
            skLineSegment(sketch, "E805", {"start": v(-13.66, 55.22) * mm, "end": v(-13.58, 55.22) * mm});
            skLineSegment(sketch, "E806", {"start": v(-13.74, 55.21) * mm, "end": v(-13.66, 55.22) * mm});
            skLineSegment(sketch, "E807", {"start": v(-13.83, 55.2) * mm, "end": v(-13.74, 55.21) * mm});
            skLineSegment(sketch, "E808", {"start": v(-13.9, 55.16) * mm, "end": v(-13.83, 55.2) * mm});
            skLineSegment(sketch, "E809", {"start": v(-13.96, 55.13) * mm, "end": v(-13.9, 55.16) * mm});
            skLineSegment(sketch, "E810", {"start": v(-14.09, 55.01) * mm, "end": v(-13.96, 55.13) * mm});
            skLineSegment(sketch, "E811", {"start": v(-14.32, 54.67) * mm, "end": v(-14.09, 55.01) * mm});
            skLineSegment(sketch, "E812", {"start": v(-15.03, 53.02) * mm, "end": v(-14.32, 54.67) * mm});
            skLineSegment(sketch, "E813", {"start": v(-16.4, 48.78) * mm, "end": v(-15.03, 53.02) * mm});
            skLineSegment(sketch, "E814", {"start": v(-17.98, 44.57) * mm, "end": v(-16.4, 48.78) * mm});
            skLineSegment(sketch, "E815", {"start": v(-18.81, 42.67) * mm, "end": v(-17.98, 44.57) * mm});
            skLineSegment(sketch, "E816", {"start": v(-19.78, 40.83) * mm, "end": v(-18.81, 42.67) * mm});
            skLineSegment(sketch, "E817", {"start": v(-20.98, 39.1) * mm, "end": v(-19.78, 40.83) * mm});
            skLineSegment(sketch, "E818", {"start": v(-21.8, 38.42) * mm, "end": v(-20.98, 39.1) * mm});
            skLineSegment(sketch, "E819", {"start": v(-22.05, 38.26) * mm, "end": v(-21.8, 38.42) * mm});
            skLineSegment(sketch, "E820", {"start": v(-22.34, 38.14) * mm, "end": v(-22.05, 38.26) * mm});
            skLineSegment(sketch, "E821", {"start": v(26.58, 35.88) * mm, "end": v(27.24, 35.65) * mm});
            skLineSegment(sketch, "E822", {"start": v(25.56, 36.09) * mm, "end": v(26.58, 35.88) * mm});
            skLineSegment(sketch, "E823", {"start": v(23.46, 36.37) * mm, "end": v(25.56, 36.09) * mm});
            skLineSegment(sketch, "E824", {"start": v(21.34, 36.65) * mm, "end": v(23.46, 36.37) * mm});
            skLineSegment(sketch, "E825", {"start": v(20.31, 36.64) * mm, "end": v(21.34, 36.65) * mm});
            skLineSegment(sketch, "E826", {"start": v(19.36, 36.43) * mm, "end": v(20.31, 36.64) * mm});
            skLineSegment(sketch, "E827", {"start": v(16.93, 34.36) * mm, "end": v(19.36, 36.43) * mm});
            skLineSegment(sketch, "E828", {"start": v(14.15, 32.62) * mm, "end": v(16.93, 34.36) * mm});
            skLineSegment(sketch, "E829", {"start": v(11.17, 31.28) * mm, "end": v(14.15, 32.62) * mm});
            skLineSegment(sketch, "E830", {"start": v(8.02, 30.37) * mm, "end": v(11.17, 31.28) * mm});
            skLineSegment(sketch, "E831", {"start": v(4.78, 29.92) * mm, "end": v(8.02, 30.37) * mm});
            skLineSegment(sketch, "E832", {"start": v(1.5, 29.92) * mm, "end": v(4.78, 29.92) * mm});
            skLineSegment(sketch, "E833", {"start": v(-1.74, 30.39) * mm, "end": v(1.5, 29.92) * mm});
            skLineSegment(sketch, "E834", {"start": v(-4.89, 31.3) * mm, "end": v(-1.74, 30.39) * mm});
            skLineSegment(sketch, "E835", {"start": v(-7.87, 32.65) * mm, "end": v(-4.89, 31.3) * mm});
            skLineSegment(sketch, "E836", {"start": v(-10.64, 34.4) * mm, "end": v(-7.87, 32.65) * mm});
            skLineSegment(sketch, "E837", {"start": v(-13.07, 36.49) * mm, "end": v(-10.64, 34.4) * mm});
            skLineSegment(sketch, "E838", {"start": v(-14, 36.72) * mm, "end": v(-13.07, 36.49) * mm});
            skLineSegment(sketch, "E839", {"start": v(-14.96, 36.77) * mm, "end": v(-14, 36.72) * mm});
            skLineSegment(sketch, "E840", {"start": v(-17, 36.46) * mm, "end": v(-14.96, 36.77) * mm});
            skLineSegment(sketch, "E841", {"start": v(-18.96, 35.93) * mm, "end": v(-17, 36.46) * mm});
            skLineSegment(sketch, "E842", {"start": v(-19.84, 35.48) * mm, "end": v(-18.96, 35.93) * mm});
            skLineSegment(sketch, "E843", {"start": v(-20.45, 35.06) * mm, "end": v(-19.84, 35.48) * mm});
            skLineSegment(sketch, "E844", {"start": v(-18.2, 32.42) * mm, "end": v(-20.45, 35.06) * mm});
            skLineSegment(sketch, "E845", {"start": v(-15.45, 29.91) * mm, "end": v(-18.2, 32.42) * mm});
            skLineSegment(sketch, "E846", {"start": v(-12.4, 27.76) * mm, "end": v(-15.45, 29.91) * mm});
            skLineSegment(sketch, "E847", {"start": v(-9.1, 26.02) * mm, "end": v(-12.4, 27.76) * mm});
            skLineSegment(sketch, "E848", {"start": v(-5.62, 24.7) * mm, "end": v(-9.1, 26.02) * mm});
            skLineSegment(sketch, "E849", {"start": v(-2, 23.81) * mm, "end": v(-5.62, 24.7) * mm});
            skLineSegment(sketch, "E850", {"start": v(1.72, 23.4) * mm, "end": v(-2, 23.81) * mm});
            skLineSegment(sketch, "E851", {"start": v(5.44, 23.45) * mm, "end": v(1.72, 23.4) * mm});
            skLineSegment(sketch, "E852", {"start": v(9.14, 23.97) * mm, "end": v(5.44, 23.45) * mm});
            skLineSegment(sketch, "E853", {"start": v(12.74, 24.94) * mm, "end": v(9.14, 23.97) * mm});
            skLineSegment(sketch, "E854", {"start": v(16.19, 26.36) * mm, "end": v(12.74, 24.94) * mm});
            skLineSegment(sketch, "E855", {"start": v(19.43, 28.2) * mm, "end": v(16.19, 26.36) * mm});
            skLineSegment(sketch, "E856", {"start": v(22.42, 30.42) * mm, "end": v(19.43, 28.2) * mm});
            skLineSegment(sketch, "E857", {"start": v(25.1, 33.01) * mm, "end": v(22.42, 30.42) * mm});
            skLineSegment(sketch, "E858", {"start": v(27.24, 35.65) * mm, "end": v(25.1, 33.01) * mm});
            skSolve(sketch);
        }
        {
            var Q0;
            Q0=makeQuery(id+"F16.imprint","IMPRINT",FACE,{"disambiguationData":[TD([[makeQuery(id+"F16.imprint","IMPRINT",EDGE,{"derivedFrom":sQuery(id+"F16.wireOp",EDGE,"E437")}),-1.0]])]});
            var Q1;
            Q1=makeQuery(id+"F16.imprint","IMPRINT",FACE,{"disambiguationData":[TD([[makeQuery(id+"F16.imprint","IMPRINT",EDGE,{"derivedFrom":sQuery(id+"F16.wireOp",EDGE,"E524")}),-1.0]])]});
            var Q2;
            Q2=makeQuery(id+"F16.imprint","IMPRINT",FACE,{"disambiguationData":[TD([[makeQuery(id+"F16.imprint","IMPRINT",EDGE,{"derivedFrom":sQuery(id+"F16.wireOp",EDGE,"E641")}),-1.0]])]});
            var Q3;
            Q3=makeQuery(id+"F16.imprint","IMPRINT",FACE,{"disambiguationData":[TD([[makeQuery(id+"F16.imprint","IMPRINT",EDGE,{"derivedFrom":sQuery(id+"F16.wireOp",EDGE,"E821")}),-1.0]])]});
            var Q4;
            Q4=makeQuery(id+"F16.imprint","IMPRINT",FACE,{"disambiguationData":[TD([[makeQuery(id+"F16.imprint","IMPRINT",EDGE,{"derivedFrom":sQuery(id+"F16.wireOp",EDGE,"E763")}),-1.0]])]});
            var Q5;
            Q5=sQuery(id+"F16.wireOp",EDGE,"E437");
            var Q6;
            Q6=sQuery(id+"F16.wireOp",EDGE,"E438");
            var Q7;
            Q7=sQuery(id+"F16.wireOp",EDGE,"E439");
            var Q8;
            Q8=sQuery(id+"F16.wireOp",EDGE,"E440");
            var Q9;
            Q9=sQuery(id+"F16.wireOp",EDGE,"E441");
            var Q10;
            Q10=sQuery(id+"F16.wireOp",EDGE,"E442");
            var Q11;
            Q11=sQuery(id+"F16.wireOp",EDGE,"E443");
            var Q12;
            Q12=sQuery(id+"F16.wireOp",EDGE,"E444");
            var Q13;
            Q13=sQuery(id+"F16.wireOp",EDGE,"E445");
            var Q14;
            Q14=sQuery(id+"F16.wireOp",EDGE,"E446");
            var Q15;
            Q15=sQuery(id+"F16.wireOp",EDGE,"E447");
            var Q16;
            Q16=sQuery(id+"F16.wireOp",EDGE,"E448");
            var Q17;
            Q17=sQuery(id+"F16.wireOp",EDGE,"E449");
            var Q18;
            Q18=sQuery(id+"F16.wireOp",EDGE,"E450");
            var Q19;
            Q19=sQuery(id+"F16.wireOp",EDGE,"E451");
            var Q20;
            Q20=sQuery(id+"F16.wireOp",EDGE,"E452");
            var Q21;
            Q21=sQuery(id+"F16.wireOp",EDGE,"E453");
            var Q22;
            Q22=sQuery(id+"F16.wireOp",EDGE,"E454");
            var Q23;
            Q23=sQuery(id+"F16.wireOp",EDGE,"E455");
            var Q24;
            Q24=sQuery(id+"F16.wireOp",EDGE,"E456");
            var Q25;
            Q25=sQuery(id+"F16.wireOp",EDGE,"E457");
            var Q26;
            Q26=sQuery(id+"F16.wireOp",EDGE,"E458");
            var Q27;
            Q27=sQuery(id+"F16.wireOp",EDGE,"E459");
            var Q28;
            Q28=sQuery(id+"F16.wireOp",EDGE,"E460");
            var Q29;
            Q29=sQuery(id+"F16.wireOp",EDGE,"E461");
            var Q30;
            Q30=sQuery(id+"F16.wireOp",EDGE,"E462");
            var Q31;
            Q31=sQuery(id+"F16.wireOp",EDGE,"E463");
            var Q32;
            Q32=sQuery(id+"F16.wireOp",EDGE,"E464");
            var Q33;
            Q33=sQuery(id+"F16.wireOp",EDGE,"E465");
            var Q34;
            Q34=sQuery(id+"F16.wireOp",EDGE,"E466");
            var Q35;
            Q35=sQuery(id+"F16.wireOp",EDGE,"E467");
            var Q36;
            Q36=sQuery(id+"F16.wireOp",EDGE,"E468");
            var Q37;
            Q37=sQuery(id+"F16.wireOp",EDGE,"E469");
            var Q38;
            Q38=sQuery(id+"F16.wireOp",EDGE,"E470");
            var Q39;
            Q39=sQuery(id+"F16.wireOp",EDGE,"E471");
            var Q40;
            Q40=sQuery(id+"F16.wireOp",EDGE,"E472");
            var Q41;
            Q41=sQuery(id+"F16.wireOp",EDGE,"E473");
            var Q42;
            Q42=sQuery(id+"F16.wireOp",EDGE,"E474");
            var Q43;
            Q43=sQuery(id+"F16.wireOp",EDGE,"E475");
            var Q44;
            Q44=sQuery(id+"F16.wireOp",EDGE,"E476");
            var Q45;
            Q45=sQuery(id+"F16.wireOp",EDGE,"E477");
            var Q46;
            Q46=sQuery(id+"F16.wireOp",EDGE,"E478");
            var Q47;
            Q47=sQuery(id+"F16.wireOp",EDGE,"E479");
            var Q48;
            Q48=sQuery(id+"F16.wireOp",EDGE,"E480");
            var Q49;
            Q49=sQuery(id+"F16.wireOp",EDGE,"E481");
            var Q50;
            Q50=sQuery(id+"F16.wireOp",EDGE,"E482");
            var Q51;
            Q51=sQuery(id+"F16.wireOp",EDGE,"E483");
            var Q52;
            Q52=sQuery(id+"F16.wireOp",EDGE,"E484");
            var Q53;
            Q53=sQuery(id+"F16.wireOp",EDGE,"E485");
            var Q54;
            Q54=sQuery(id+"F16.wireOp",EDGE,"E486");
            var Q55;
            Q55=sQuery(id+"F16.wireOp",EDGE,"E487");
            var Q56;
            Q56=sQuery(id+"F16.wireOp",EDGE,"E488");
            var Q57;
            Q57=sQuery(id+"F16.wireOp",EDGE,"E489");
            var Q58;
            Q58=sQuery(id+"F16.wireOp",EDGE,"E490");
            var Q59;
            Q59=sQuery(id+"F16.wireOp",EDGE,"E491");
            var Q60;
            Q60=sQuery(id+"F16.wireOp",EDGE,"E492");
            var Q61;
            Q61=sQuery(id+"F16.wireOp",EDGE,"E493");
            var Q62;
            Q62=sQuery(id+"F16.wireOp",EDGE,"E494");
            var Q63;
            Q63=sQuery(id+"F16.wireOp",EDGE,"E495");
            var Q64;
            Q64=sQuery(id+"F16.wireOp",EDGE,"E496");
            var Q65;
            Q65=sQuery(id+"F16.wireOp",EDGE,"E497");
            var Q66;
            Q66=sQuery(id+"F16.wireOp",EDGE,"E498");
            var Q67;
            Q67=sQuery(id+"F16.wireOp",EDGE,"E499");
            var Q68;
            Q68=sQuery(id+"F16.wireOp",EDGE,"E500");
            var Q69;
            Q69=sQuery(id+"F16.wireOp",EDGE,"E501");
            var Q70;
            Q70=sQuery(id+"F16.wireOp",EDGE,"E502");
            var Q71;
            Q71=sQuery(id+"F16.wireOp",EDGE,"E503");
            var Q72;
            Q72=sQuery(id+"F16.wireOp",EDGE,"E504");
            var Q73;
            Q73=sQuery(id+"F16.wireOp",EDGE,"E505");
            var Q74;
            Q74=sQuery(id+"F16.wireOp",EDGE,"E506");
            var Q75;
            Q75=sQuery(id+"F16.wireOp",EDGE,"E507");
            var Q76;
            Q76=sQuery(id+"F16.wireOp",EDGE,"E508");
            var Q77;
            Q77=sQuery(id+"F16.wireOp",EDGE,"E509");
            var Q78;
            Q78=sQuery(id+"F16.wireOp",EDGE,"E510");
            var Q79;
            Q79=sQuery(id+"F16.wireOp",EDGE,"E511");
            var Q80;
            Q80=sQuery(id+"F16.wireOp",EDGE,"E512");
            var Q81;
            Q81=sQuery(id+"F16.wireOp",EDGE,"E513");
            var Q82;
            Q82=sQuery(id+"F16.wireOp",EDGE,"E514");
            var Q83;
            Q83=sQuery(id+"F16.wireOp",EDGE,"E515");
            var Q84;
            Q84=sQuery(id+"F16.wireOp",EDGE,"E516");
            var Q85;
            Q85=sQuery(id+"F16.wireOp",EDGE,"E517");
            var Q86;
            Q86=sQuery(id+"F16.wireOp",EDGE,"E518");
            var Q87;
            Q87=sQuery(id+"F16.wireOp",EDGE,"E519");
            var Q88;
            Q88=sQuery(id+"F16.wireOp",EDGE,"E520");
            var Q89;
            Q89=sQuery(id+"F16.wireOp",EDGE,"E521");
            var Q90;
            Q90=sQuery(id+"F16.wireOp",EDGE,"E522");
            var Q91;
            Q91=sQuery(id+"F16.wireOp",EDGE,"E523");
            var Q92;
            Q92=sQuery(id+"F16.wireOp",EDGE,"E524");
            var Q93;
            Q93=sQuery(id+"F16.wireOp",EDGE,"E525");
            var Q94;
            Q94=sQuery(id+"F16.wireOp",EDGE,"E526");
            var Q95;
            Q95=sQuery(id+"F16.wireOp",EDGE,"E527");
            var Q96;
            Q96=sQuery(id+"F16.wireOp",EDGE,"E528");
            var Q97;
            Q97=sQuery(id+"F16.wireOp",EDGE,"E529");
            var Q98;
            Q98=sQuery(id+"F16.wireOp",EDGE,"E530");
            var Q99;
            Q99=sQuery(id+"F16.wireOp",EDGE,"E531");
            var Q100;
            Q100=sQuery(id+"F16.wireOp",EDGE,"E532");
            var Q101;
            Q101=sQuery(id+"F16.wireOp",EDGE,"E533");
            var Q102;
            Q102=sQuery(id+"F16.wireOp",EDGE,"E534");
            var Q103;
            Q103=sQuery(id+"F16.wireOp",EDGE,"E535");
            var Q104;
            Q104=sQuery(id+"F16.wireOp",EDGE,"E536");
            var Q105;
            Q105=sQuery(id+"F16.wireOp",EDGE,"E537");
            var Q106;
            Q106=sQuery(id+"F16.wireOp",EDGE,"E538");
            var Q107;
            Q107=sQuery(id+"F16.wireOp",EDGE,"E539");
            var Q108;
            Q108=sQuery(id+"F16.wireOp",EDGE,"E540");
            var Q109;
            Q109=sQuery(id+"F16.wireOp",EDGE,"E541");
            var Q110;
            Q110=sQuery(id+"F16.wireOp",EDGE,"E542");
            var Q111;
            Q111=sQuery(id+"F16.wireOp",EDGE,"E543");
            var Q112;
            Q112=sQuery(id+"F16.wireOp",EDGE,"E544");
            var Q113;
            Q113=sQuery(id+"F16.wireOp",EDGE,"E545");
            var Q114;
            Q114=sQuery(id+"F16.wireOp",EDGE,"E546");
            var Q115;
            Q115=sQuery(id+"F16.wireOp",EDGE,"E547");
            var Q116;
            Q116=sQuery(id+"F16.wireOp",EDGE,"E548");
            var Q117;
            Q117=sQuery(id+"F16.wireOp",EDGE,"E549");
            var Q118;
            Q118=sQuery(id+"F16.wireOp",EDGE,"E550");
            var Q119;
            Q119=sQuery(id+"F16.wireOp",EDGE,"E551");
            var Q120;
            Q120=sQuery(id+"F16.wireOp",EDGE,"E552");
            var Q121;
            Q121=sQuery(id+"F16.wireOp",EDGE,"E553");
            var Q122;
            Q122=sQuery(id+"F16.wireOp",EDGE,"E554");
            var Q123;
            Q123=sQuery(id+"F16.wireOp",EDGE,"E555");
            var Q124;
            Q124=sQuery(id+"F16.wireOp",EDGE,"E556");
            var Q125;
            Q125=sQuery(id+"F16.wireOp",EDGE,"E557");
            var Q126;
            Q126=sQuery(id+"F16.wireOp",EDGE,"E558");
            var Q127;
            Q127=sQuery(id+"F16.wireOp",EDGE,"E559");
            var Q128;
            Q128=sQuery(id+"F16.wireOp",EDGE,"E560");
            var Q129;
            Q129=sQuery(id+"F16.wireOp",EDGE,"E561");
            var Q130;
            Q130=sQuery(id+"F16.wireOp",EDGE,"E562");
            var Q131;
            Q131=sQuery(id+"F16.wireOp",EDGE,"E563");
            var Q132;
            Q132=sQuery(id+"F16.wireOp",EDGE,"E564");
            var Q133;
            Q133=sQuery(id+"F16.wireOp",EDGE,"E565");
            var Q134;
            Q134=sQuery(id+"F16.wireOp",EDGE,"E566");
            var Q135;
            Q135=sQuery(id+"F16.wireOp",EDGE,"E567");
            var Q136;
            Q136=sQuery(id+"F16.wireOp",EDGE,"E568");
            var Q137;
            Q137=sQuery(id+"F16.wireOp",EDGE,"E569");
            var Q138;
            Q138=sQuery(id+"F16.wireOp",EDGE,"E570");
            var Q139;
            Q139=sQuery(id+"F16.wireOp",EDGE,"E571");
            var Q140;
            Q140=sQuery(id+"F16.wireOp",EDGE,"E572");
            var Q141;
            Q141=sQuery(id+"F16.wireOp",EDGE,"E573");
            var Q142;
            Q142=sQuery(id+"F16.wireOp",EDGE,"E574");
            var Q143;
            Q143=sQuery(id+"F16.wireOp",EDGE,"E575");
            var Q144;
            Q144=sQuery(id+"F16.wireOp",EDGE,"E576");
            var Q145;
            Q145=sQuery(id+"F16.wireOp",EDGE,"E577");
            var Q146;
            Q146=sQuery(id+"F16.wireOp",EDGE,"E578");
            var Q147;
            Q147=sQuery(id+"F16.wireOp",EDGE,"E579");
            var Q148;
            Q148=sQuery(id+"F16.wireOp",EDGE,"E580");
            var Q149;
            Q149=sQuery(id+"F16.wireOp",EDGE,"E581");
            var Q150;
            Q150=sQuery(id+"F16.wireOp",EDGE,"E582");
            var Q151;
            Q151=sQuery(id+"F16.wireOp",EDGE,"E583");
            var Q152;
            Q152=sQuery(id+"F16.wireOp",EDGE,"E584");
            var Q153;
            Q153=sQuery(id+"F16.wireOp",EDGE,"E585");
            var Q154;
            Q154=sQuery(id+"F16.wireOp",EDGE,"E586");
            var Q155;
            Q155=sQuery(id+"F16.wireOp",EDGE,"E587");
            var Q156;
            Q156=sQuery(id+"F16.wireOp",EDGE,"E588");
            var Q157;
            Q157=sQuery(id+"F16.wireOp",EDGE,"E589");
            var Q158;
            Q158=sQuery(id+"F16.wireOp",EDGE,"E590");
            var Q159;
            Q159=sQuery(id+"F16.wireOp",EDGE,"E591");
            var Q160;
            Q160=sQuery(id+"F16.wireOp",EDGE,"E592");
            var Q161;
            Q161=sQuery(id+"F16.wireOp",EDGE,"E593");
            var Q162;
            Q162=sQuery(id+"F16.wireOp",EDGE,"E594");
            var Q163;
            Q163=sQuery(id+"F16.wireOp",EDGE,"E595");
            var Q164;
            Q164=sQuery(id+"F16.wireOp",EDGE,"E596");
            var Q165;
            Q165=sQuery(id+"F16.wireOp",EDGE,"E597");
            var Q166;
            Q166=sQuery(id+"F16.wireOp",EDGE,"E598");
            var Q167;
            Q167=sQuery(id+"F16.wireOp",EDGE,"E599");
            var Q168;
            Q168=sQuery(id+"F16.wireOp",EDGE,"E600");
            var Q169;
            Q169=sQuery(id+"F16.wireOp",EDGE,"E601");
            var Q170;
            Q170=sQuery(id+"F16.wireOp",EDGE,"E602");
            var Q171;
            Q171=sQuery(id+"F16.wireOp",EDGE,"E603");
            var Q172;
            Q172=sQuery(id+"F16.wireOp",EDGE,"E604");
            var Q173;
            Q173=sQuery(id+"F16.wireOp",EDGE,"E605");
            var Q174;
            Q174=sQuery(id+"F16.wireOp",EDGE,"E606");
            var Q175;
            Q175=sQuery(id+"F16.wireOp",EDGE,"E607");
            var Q176;
            Q176=sQuery(id+"F16.wireOp",EDGE,"E608");
            var Q177;
            Q177=sQuery(id+"F16.wireOp",EDGE,"E609");
            var Q178;
            Q178=sQuery(id+"F16.wireOp",EDGE,"E610");
            var Q179;
            Q179=sQuery(id+"F16.wireOp",EDGE,"E611");
            var Q180;
            Q180=sQuery(id+"F16.wireOp",EDGE,"E612");
            var Q181;
            Q181=sQuery(id+"F16.wireOp",EDGE,"E613");
            var Q182;
            Q182=sQuery(id+"F16.wireOp",EDGE,"E614");
            var Q183;
            Q183=sQuery(id+"F16.wireOp",EDGE,"E615");
            var Q184;
            Q184=sQuery(id+"F16.wireOp",EDGE,"E616");
            var Q185;
            Q185=sQuery(id+"F16.wireOp",EDGE,"E617");
            var Q186;
            Q186=sQuery(id+"F16.wireOp",EDGE,"E618");
            var Q187;
            Q187=sQuery(id+"F16.wireOp",EDGE,"E619");
            var Q188;
            Q188=sQuery(id+"F16.wireOp",EDGE,"E620");
            var Q189;
            Q189=sQuery(id+"F16.wireOp",EDGE,"E621");
            var Q190;
            Q190=sQuery(id+"F16.wireOp",EDGE,"E622");
            var Q191;
            Q191=sQuery(id+"F16.wireOp",EDGE,"E623");
            var Q192;
            Q192=sQuery(id+"F16.wireOp",EDGE,"E624");
            var Q193;
            Q193=sQuery(id+"F16.wireOp",EDGE,"E625");
            var Q194;
            Q194=sQuery(id+"F16.wireOp",EDGE,"E626");
            var Q195;
            Q195=sQuery(id+"F16.wireOp",EDGE,"E627");
            var Q196;
            Q196=sQuery(id+"F16.wireOp",EDGE,"E628");
            var Q197;
            Q197=sQuery(id+"F16.wireOp",EDGE,"E629");
            var Q198;
            Q198=sQuery(id+"F16.wireOp",EDGE,"E630");
            var Q199;
            Q199=sQuery(id+"F16.wireOp",EDGE,"E631");
            var Q200;
            Q200=sQuery(id+"F16.wireOp",EDGE,"E632");
            var Q201;
            Q201=sQuery(id+"F16.wireOp",EDGE,"E633");
            var Q202;
            Q202=sQuery(id+"F16.wireOp",EDGE,"E634");
            var Q203;
            Q203=sQuery(id+"F16.wireOp",EDGE,"E635");
            var Q204;
            Q204=sQuery(id+"F16.wireOp",EDGE,"E636");
            var Q205;
            Q205=sQuery(id+"F16.wireOp",EDGE,"E637");
            var Q206;
            Q206=sQuery(id+"F16.wireOp",EDGE,"E638");
            var Q207;
            Q207=sQuery(id+"F16.wireOp",EDGE,"E639");
            var Q208;
            Q208=sQuery(id+"F16.wireOp",EDGE,"E640");
            var Q209;
            Q209=sQuery(id+"F16.wireOp",EDGE,"E641");
            var Q210;
            Q210=sQuery(id+"F16.wireOp",EDGE,"E642");
            var Q211;
            Q211=sQuery(id+"F16.wireOp",EDGE,"E643");
            var Q212;
            Q212=sQuery(id+"F16.wireOp",EDGE,"E644");
            var Q213;
            Q213=sQuery(id+"F16.wireOp",EDGE,"E645");
            var Q214;
            Q214=sQuery(id+"F16.wireOp",EDGE,"E646");
            var Q215;
            Q215=sQuery(id+"F16.wireOp",EDGE,"E647");
            var Q216;
            Q216=sQuery(id+"F16.wireOp",EDGE,"E648");
            var Q217;
            Q217=sQuery(id+"F16.wireOp",EDGE,"E649");
            var Q218;
            Q218=sQuery(id+"F16.wireOp",EDGE,"E650");
            var Q219;
            Q219=sQuery(id+"F16.wireOp",EDGE,"E651");
            var Q220;
            Q220=sQuery(id+"F16.wireOp",EDGE,"E652");
            var Q221;
            Q221=sQuery(id+"F16.wireOp",EDGE,"E653");
            var Q222;
            Q222=sQuery(id+"F16.wireOp",EDGE,"E654");
            var Q223;
            Q223=sQuery(id+"F16.wireOp",EDGE,"E655");
            var Q224;
            Q224=sQuery(id+"F16.wireOp",EDGE,"E656");
            var Q225;
            Q225=sQuery(id+"F16.wireOp",EDGE,"E657");
            var Q226;
            Q226=sQuery(id+"F16.wireOp",EDGE,"E658");
            var Q227;
            Q227=sQuery(id+"F16.wireOp",EDGE,"E659");
            var Q228;
            Q228=sQuery(id+"F16.wireOp",EDGE,"E660");
            var Q229;
            Q229=sQuery(id+"F16.wireOp",EDGE,"E661");
            var Q230;
            Q230=sQuery(id+"F16.wireOp",EDGE,"E662");
            var Q231;
            Q231=sQuery(id+"F16.wireOp",EDGE,"E663");
            var Q232;
            Q232=sQuery(id+"F16.wireOp",EDGE,"E664");
            var Q233;
            Q233=sQuery(id+"F16.wireOp",EDGE,"E665");
            var Q234;
            Q234=sQuery(id+"F16.wireOp",EDGE,"E666");
            var Q235;
            Q235=sQuery(id+"F16.wireOp",EDGE,"E667");
            var Q236;
            Q236=sQuery(id+"F16.wireOp",EDGE,"E668");
            var Q237;
            Q237=sQuery(id+"F16.wireOp",EDGE,"E669");
            var Q238;
            Q238=sQuery(id+"F16.wireOp",EDGE,"E670");
            var Q239;
            Q239=sQuery(id+"F16.wireOp",EDGE,"E671");
            var Q240;
            Q240=sQuery(id+"F16.wireOp",EDGE,"E672");
            var Q241;
            Q241=sQuery(id+"F16.wireOp",EDGE,"E673");
            var Q242;
            Q242=sQuery(id+"F16.wireOp",EDGE,"E674");
            var Q243;
            Q243=sQuery(id+"F16.wireOp",EDGE,"E675");
            var Q244;
            Q244=sQuery(id+"F16.wireOp",EDGE,"E676");
            var Q245;
            Q245=sQuery(id+"F16.wireOp",EDGE,"E677");
            var Q246;
            Q246=sQuery(id+"F16.wireOp",EDGE,"E678");
            var Q247;
            Q247=sQuery(id+"F16.wireOp",EDGE,"E679");
            var Q248;
            Q248=sQuery(id+"F16.wireOp",EDGE,"E680");
            var Q249;
            Q249=sQuery(id+"F16.wireOp",EDGE,"E681");
            var Q250;
            Q250=sQuery(id+"F16.wireOp",EDGE,"E682");
            var Q251;
            Q251=sQuery(id+"F16.wireOp",EDGE,"E683");
            var Q252;
            Q252=sQuery(id+"F16.wireOp",EDGE,"E684");
            var Q253;
            Q253=sQuery(id+"F16.wireOp",EDGE,"E685");
            var Q254;
            Q254=sQuery(id+"F16.wireOp",EDGE,"E686");
            var Q255;
            Q255=sQuery(id+"F16.wireOp",EDGE,"E687");
            var Q256;
            Q256=sQuery(id+"F16.wireOp",EDGE,"E688");
            var Q257;
            Q257=sQuery(id+"F16.wireOp",EDGE,"E689");
            var Q258;
            Q258=sQuery(id+"F16.wireOp",EDGE,"E690");
            var Q259;
            Q259=sQuery(id+"F16.wireOp",EDGE,"E691");
            var Q260;
            Q260=sQuery(id+"F16.wireOp",EDGE,"E692");
            var Q261;
            Q261=sQuery(id+"F16.wireOp",EDGE,"E693");
            var Q262;
            Q262=sQuery(id+"F16.wireOp",EDGE,"E694");
            var Q263;
            Q263=sQuery(id+"F16.wireOp",EDGE,"E695");
            var Q264;
            Q264=sQuery(id+"F16.wireOp",EDGE,"E696");
            var Q265;
            Q265=sQuery(id+"F16.wireOp",EDGE,"E697");
            var Q266;
            Q266=sQuery(id+"F16.wireOp",EDGE,"E698");
            var Q267;
            Q267=sQuery(id+"F16.wireOp",EDGE,"E699");
            var Q268;
            Q268=sQuery(id+"F16.wireOp",EDGE,"E700");
            var Q269;
            Q269=sQuery(id+"F16.wireOp",EDGE,"E701");
            var Q270;
            Q270=sQuery(id+"F16.wireOp",EDGE,"E702");
            var Q271;
            Q271=sQuery(id+"F16.wireOp",EDGE,"E703");
            var Q272;
            Q272=sQuery(id+"F16.wireOp",EDGE,"E704");
            var Q273;
            Q273=sQuery(id+"F16.wireOp",EDGE,"E705");
            var Q274;
            Q274=sQuery(id+"F16.wireOp",EDGE,"E706");
            var Q275;
            Q275=sQuery(id+"F16.wireOp",EDGE,"E707");
            var Q276;
            Q276=sQuery(id+"F16.wireOp",EDGE,"E708");
            var Q277;
            Q277=sQuery(id+"F16.wireOp",EDGE,"E709");
            var Q278;
            Q278=sQuery(id+"F16.wireOp",EDGE,"E710");
            var Q279;
            Q279=sQuery(id+"F16.wireOp",EDGE,"E711");
            var Q280;
            Q280=sQuery(id+"F16.wireOp",EDGE,"E712");
            var Q281;
            Q281=sQuery(id+"F16.wireOp",EDGE,"E713");
            var Q282;
            Q282=sQuery(id+"F16.wireOp",EDGE,"E714");
            var Q283;
            Q283=sQuery(id+"F16.wireOp",EDGE,"E715");
            var Q284;
            Q284=sQuery(id+"F16.wireOp",EDGE,"E716");
            var Q285;
            Q285=sQuery(id+"F16.wireOp",EDGE,"E717");
            var Q286;
            Q286=sQuery(id+"F16.wireOp",EDGE,"E718");
            var Q287;
            Q287=sQuery(id+"F16.wireOp",EDGE,"E719");
            var Q288;
            Q288=sQuery(id+"F16.wireOp",EDGE,"E720");
            var Q289;
            Q289=sQuery(id+"F16.wireOp",EDGE,"E721");
            var Q290;
            Q290=sQuery(id+"F16.wireOp",EDGE,"E722");
            var Q291;
            Q291=sQuery(id+"F16.wireOp",EDGE,"E723");
            var Q292;
            Q292=sQuery(id+"F16.wireOp",EDGE,"E724");
            var Q293;
            Q293=sQuery(id+"F16.wireOp",EDGE,"E725");
            var Q294;
            Q294=sQuery(id+"F16.wireOp",EDGE,"E726");
            var Q295;
            Q295=sQuery(id+"F16.wireOp",EDGE,"E727");
            var Q296;
            Q296=sQuery(id+"F16.wireOp",EDGE,"E728");
            var Q297;
            Q297=sQuery(id+"F16.wireOp",EDGE,"E729");
            var Q298;
            Q298=sQuery(id+"F16.wireOp",EDGE,"E730");
            var Q299;
            Q299=sQuery(id+"F16.wireOp",EDGE,"E731");
            var Q300;
            Q300=sQuery(id+"F16.wireOp",EDGE,"E732");
            var Q301;
            Q301=sQuery(id+"F16.wireOp",EDGE,"E733");
            var Q302;
            Q302=sQuery(id+"F16.wireOp",EDGE,"E734");
            var Q303;
            Q303=sQuery(id+"F16.wireOp",EDGE,"E735");
            var Q304;
            Q304=sQuery(id+"F16.wireOp",EDGE,"E736");
            var Q305;
            Q305=sQuery(id+"F16.wireOp",EDGE,"E737");
            var Q306;
            Q306=sQuery(id+"F16.wireOp",EDGE,"E738");
            var Q307;
            Q307=sQuery(id+"F16.wireOp",EDGE,"E739");
            var Q308;
            Q308=sQuery(id+"F16.wireOp",EDGE,"E740");
            var Q309;
            Q309=sQuery(id+"F16.wireOp",EDGE,"E741");
            var Q310;
            Q310=sQuery(id+"F16.wireOp",EDGE,"E742");
            var Q311;
            Q311=sQuery(id+"F16.wireOp",EDGE,"E743");
            var Q312;
            Q312=sQuery(id+"F16.wireOp",EDGE,"E744");
            var Q313;
            Q313=sQuery(id+"F16.wireOp",EDGE,"E745");
            var Q314;
            Q314=sQuery(id+"F16.wireOp",EDGE,"E746");
            var Q315;
            Q315=sQuery(id+"F16.wireOp",EDGE,"E747");
            var Q316;
            Q316=sQuery(id+"F16.wireOp",EDGE,"E748");
            var Q317;
            Q317=sQuery(id+"F16.wireOp",EDGE,"E749");
            var Q318;
            Q318=sQuery(id+"F16.wireOp",EDGE,"E750");
            var Q319;
            Q319=sQuery(id+"F16.wireOp",EDGE,"E751");
            var Q320;
            Q320=sQuery(id+"F16.wireOp",EDGE,"E752");
            var Q321;
            Q321=sQuery(id+"F16.wireOp",EDGE,"E753");
            var Q322;
            Q322=sQuery(id+"F16.wireOp",EDGE,"E754");
            var Q323;
            Q323=sQuery(id+"F16.wireOp",EDGE,"E755");
            var Q324;
            Q324=sQuery(id+"F16.wireOp",EDGE,"E756");
            var Q325;
            Q325=sQuery(id+"F16.wireOp",EDGE,"E757");
            var Q326;
            Q326=sQuery(id+"F16.wireOp",EDGE,"E758");
            var Q327;
            Q327=sQuery(id+"F16.wireOp",EDGE,"E759");
            var Q328;
            Q328=sQuery(id+"F16.wireOp",EDGE,"E760");
            var Q329;
            Q329=sQuery(id+"F16.wireOp",EDGE,"E761");
            var Q330;
            Q330=sQuery(id+"F16.wireOp",EDGE,"E762");
            var Q331;
            Q331=sQuery(id+"F16.wireOp",EDGE,"E763");
            var Q332;
            Q332=sQuery(id+"F16.wireOp",EDGE,"E764");
            var Q333;
            Q333=sQuery(id+"F16.wireOp",EDGE,"E765");
            var Q334;
            Q334=sQuery(id+"F16.wireOp",EDGE,"E766");
            var Q335;
            Q335=sQuery(id+"F16.wireOp",EDGE,"E767");
            var Q336;
            Q336=sQuery(id+"F16.wireOp",EDGE,"E768");
            var Q337;
            Q337=sQuery(id+"F16.wireOp",EDGE,"E769");
            var Q338;
            Q338=sQuery(id+"F16.wireOp",EDGE,"E770");
            var Q339;
            Q339=sQuery(id+"F16.wireOp",EDGE,"E771");
            var Q340;
            Q340=sQuery(id+"F16.wireOp",EDGE,"E772");
            var Q341;
            Q341=sQuery(id+"F16.wireOp",EDGE,"E773");
            var Q342;
            Q342=sQuery(id+"F16.wireOp",EDGE,"E774");
            var Q343;
            Q343=sQuery(id+"F16.wireOp",EDGE,"E775");
            var Q344;
            Q344=sQuery(id+"F16.wireOp",EDGE,"E776");
            var Q345;
            Q345=sQuery(id+"F16.wireOp",EDGE,"E777");
            var Q346;
            Q346=sQuery(id+"F16.wireOp",EDGE,"E778");
            var Q347;
            Q347=sQuery(id+"F16.wireOp",EDGE,"E779");
            var Q348;
            Q348=sQuery(id+"F16.wireOp",EDGE,"E780");
            var Q349;
            Q349=sQuery(id+"F16.wireOp",EDGE,"E781");
            var Q350;
            Q350=sQuery(id+"F16.wireOp",EDGE,"E782");
            var Q351;
            Q351=sQuery(id+"F16.wireOp",EDGE,"E783");
            var Q352;
            Q352=sQuery(id+"F16.wireOp",EDGE,"E784");
            var Q353;
            Q353=sQuery(id+"F16.wireOp",EDGE,"E785");
            var Q354;
            Q354=sQuery(id+"F16.wireOp",EDGE,"E786");
            var Q355;
            Q355=sQuery(id+"F16.wireOp",EDGE,"E787");
            var Q356;
            Q356=sQuery(id+"F16.wireOp",EDGE,"E788");
            var Q357;
            Q357=sQuery(id+"F16.wireOp",EDGE,"E789");
            var Q358;
            Q358=sQuery(id+"F16.wireOp",EDGE,"E790");
            var Q359;
            Q359=sQuery(id+"F16.wireOp",EDGE,"E791");
            var Q360;
            Q360=sQuery(id+"F16.wireOp",EDGE,"E792");
            var Q361;
            Q361=sQuery(id+"F16.wireOp",EDGE,"E793");
            var Q362;
            Q362=sQuery(id+"F16.wireOp",EDGE,"E794");
            var Q363;
            Q363=sQuery(id+"F16.wireOp",EDGE,"E795");
            var Q364;
            Q364=sQuery(id+"F16.wireOp",EDGE,"E796");
            var Q365;
            Q365=sQuery(id+"F16.wireOp",EDGE,"E797");
            var Q366;
            Q366=sQuery(id+"F16.wireOp",EDGE,"E798");
            var Q367;
            Q367=sQuery(id+"F16.wireOp",EDGE,"E799");
            var Q368;
            Q368=sQuery(id+"F16.wireOp",EDGE,"E800");
            var Q369;
            Q369=sQuery(id+"F16.wireOp",EDGE,"E801");
            var Q370;
            Q370=sQuery(id+"F16.wireOp",EDGE,"E802");
            var Q371;
            Q371=sQuery(id+"F16.wireOp",EDGE,"E803");
            var Q372;
            Q372=sQuery(id+"F16.wireOp",EDGE,"E804");
            var Q373;
            Q373=sQuery(id+"F16.wireOp",EDGE,"E805");
            var Q374;
            Q374=sQuery(id+"F16.wireOp",EDGE,"E806");
            var Q375;
            Q375=sQuery(id+"F16.wireOp",EDGE,"E807");
            var Q376;
            Q376=sQuery(id+"F16.wireOp",EDGE,"E808");
            var Q377;
            Q377=sQuery(id+"F16.wireOp",EDGE,"E809");
            var Q378;
            Q378=sQuery(id+"F16.wireOp",EDGE,"E810");
            var Q379;
            Q379=sQuery(id+"F16.wireOp",EDGE,"E811");
            var Q380;
            Q380=sQuery(id+"F16.wireOp",EDGE,"E812");
            var Q381;
            Q381=sQuery(id+"F16.wireOp",EDGE,"E813");
            var Q382;
            Q382=sQuery(id+"F16.wireOp",EDGE,"E814");
            var Q383;
            Q383=sQuery(id+"F16.wireOp",EDGE,"E815");
            var Q384;
            Q384=sQuery(id+"F16.wireOp",EDGE,"E816");
            var Q385;
            Q385=sQuery(id+"F16.wireOp",EDGE,"E817");
            var Q386;
            Q386=sQuery(id+"F16.wireOp",EDGE,"E818");
            var Q387;
            Q387=sQuery(id+"F16.wireOp",EDGE,"E819");
            var Q388;
            Q388=sQuery(id+"F16.wireOp",EDGE,"E820");
            var Q389;
            Q389=sQuery(id+"F16.wireOp",EDGE,"E821");
            var Q390;
            Q390=sQuery(id+"F16.wireOp",EDGE,"E822");
            var Q391;
            Q391=sQuery(id+"F16.wireOp",EDGE,"E823");
            var Q392;
            Q392=sQuery(id+"F16.wireOp",EDGE,"E824");
            var Q393;
            Q393=sQuery(id+"F16.wireOp",EDGE,"E825");
            var Q394;
            Q394=sQuery(id+"F16.wireOp",EDGE,"E826");
            var Q395;
            Q395=sQuery(id+"F16.wireOp",EDGE,"E827");
            var Q396;
            Q396=sQuery(id+"F16.wireOp",EDGE,"E828");
            var Q397;
            Q397=sQuery(id+"F16.wireOp",EDGE,"E829");
            var Q398;
            Q398=sQuery(id+"F16.wireOp",EDGE,"E830");
            var Q399;
            Q399=sQuery(id+"F16.wireOp",EDGE,"E831");
            var Q400;
            Q400=sQuery(id+"F16.wireOp",EDGE,"E832");
            var Q401;
            Q401=sQuery(id+"F16.wireOp",EDGE,"E833");
            var Q402;
            Q402=sQuery(id+"F16.wireOp",EDGE,"E834");
            var Q403;
            Q403=sQuery(id+"F16.wireOp",EDGE,"E835");
            var Q404;
            Q404=sQuery(id+"F16.wireOp",EDGE,"E836");
            var Q405;
            Q405=sQuery(id+"F16.wireOp",EDGE,"E837");
            var Q406;
            Q406=sQuery(id+"F16.wireOp",EDGE,"E838");
            var Q407;
            Q407=sQuery(id+"F16.wireOp",EDGE,"E839");
            var Q408;
            Q408=sQuery(id+"F16.wireOp",EDGE,"E840");
            var Q409;
            Q409=sQuery(id+"F16.wireOp",EDGE,"E841");
            var Q410;
            Q410=sQuery(id+"F16.wireOp",EDGE,"E842");
            var Q411;
            Q411=sQuery(id+"F16.wireOp",EDGE,"E843");
            var Q412;
            Q412=sQuery(id+"F16.wireOp",EDGE,"E844");
            var Q413;
            Q413=sQuery(id+"F16.wireOp",EDGE,"E845");
            var Q414;
            Q414=sQuery(id+"F16.wireOp",EDGE,"E846");
            var Q415;
            Q415=sQuery(id+"F16.wireOp",EDGE,"E847");
            var Q416;
            Q416=sQuery(id+"F16.wireOp",EDGE,"E848");
            var Q417;
            Q417=sQuery(id+"F16.wireOp",EDGE,"E849");
            var Q418;
            Q418=sQuery(id+"F16.wireOp",EDGE,"E850");
            var Q419;
            Q419=sQuery(id+"F16.wireOp",EDGE,"E851");
            var Q420;
            Q420=sQuery(id+"F16.wireOp",EDGE,"E852");
            var Q421;
            Q421=sQuery(id+"F16.wireOp",EDGE,"E853");
            var Q422;
            Q422=sQuery(id+"F16.wireOp",EDGE,"E854");
            var Q423;
            Q423=sQuery(id+"F16.wireOp",EDGE,"E855");
            var Q424;
            Q424=sQuery(id+"F16.wireOp",EDGE,"E856");
            var Q425;
            Q425=sQuery(id+"F16.wireOp",EDGE,"E857");
            var Q426;
            Q426=sQuery(id+"F16.wireOp",EDGE,"E858");
            extrude(context, id + "F17", {"entities" : qUnion([Q0, Q1, Q2, Q3, Q4]), "operationType" : NewBodyOperationType.REMOVE, "surfaceEntities" : qUnion([Q5, Q6, Q7, Q8, Q9, Q10, Q11, Q12, Q13, Q14, Q15, Q16, Q17, Q18, Q19, Q20, Q21, Q22, Q23, Q24, Q25, Q26, Q27, Q28, Q29, Q30, Q31, Q32, Q33, Q34, Q35, Q36, Q37, Q38, Q39, Q40, Q41, Q42, Q43, Q44, Q45, Q46, Q47, Q48, Q49, Q50, Q51, Q52, Q53, Q54, Q55, Q56, Q57, Q58, Q59, Q60, Q61, Q62, Q63, Q64, Q65, Q66, Q67, Q68, Q69, Q70, Q71, Q72, Q73, Q74, Q75, Q76, Q77, Q78, Q79, Q80, Q81, Q82, Q83, Q84, Q85, Q86, Q87, Q88, Q89, Q90, Q91, Q92, Q93, Q94, Q95, Q96, Q97, Q98, Q99, Q100, Q101, Q102, Q103, Q104, Q105, Q106, Q107, Q108, Q109, Q110, Q111, Q112, Q113, Q114, Q115, Q116, Q117, Q118, Q119, Q120, Q121, Q122, Q123, Q124, Q125, Q126, Q127, Q128, Q129, Q130, Q131, Q132, Q133, Q134, Q135, Q136, Q137, Q138, Q139, Q140, Q141, Q142, Q143, Q144, Q145, Q146, Q147, Q148, Q149, Q150, Q151, Q152, Q153, Q154, Q155, Q156, Q157, Q158, Q159, Q160, Q161, Q162, Q163, Q164, Q165, Q166, Q167, Q168, Q169, Q170, Q171, Q172, Q173, Q174, Q175, Q176, Q177, Q178, Q179, Q180, Q181, Q182, Q183, Q184, Q185, Q186, Q187, Q188, Q189, Q190, Q191, Q192, Q193, Q194, Q195, Q196, Q197, Q198, Q199, Q200, Q201, Q202, Q203, Q204, Q205, Q206, Q207, Q208, Q209, Q210, Q211, Q212, Q213, Q214, Q215, Q216, Q217, Q218, Q219, Q220, Q221, Q222, Q223, Q224, Q225, Q226, Q227, Q228, Q229, Q230, Q231, Q232, Q233, Q234, Q235, Q236, Q237, Q238, Q239, Q240, Q241, Q242, Q243, Q244, Q245, Q246, Q247, Q248, Q249, Q250, Q251, Q252, Q253, Q254, Q255, Q256, Q257, Q258, Q259, Q260, Q261, Q262, Q263, Q264, Q265, Q266, Q267, Q268, Q269, Q270, Q271, Q272, Q273, Q274, Q275, Q276, Q277, Q278, Q279, Q280, Q281, Q282, Q283, Q284, Q285, Q286, Q287, Q288, Q289, Q290, Q291, Q292, Q293, Q294, Q295, Q296, Q297, Q298, Q299, Q300, Q301, Q302, Q303, Q304, Q305, Q306, Q307, Q308, Q309, Q310, Q311, Q312, Q313, Q314, Q315, Q316, Q317, Q318, Q319, Q320, Q321, Q322, Q323, Q324, Q325, Q326, Q327, Q328, Q329, Q330, Q331, Q332, Q333, Q334, Q335, Q336, Q337, Q338, Q339, Q340, Q341, Q342, Q343, Q344, Q345, Q346, Q347, Q348, Q349, Q350, Q351, Q352, Q353, Q354, Q355, Q356, Q357, Q358, Q359, Q360, Q361, Q362, Q363, Q364, Q365, Q366, Q367, Q368, Q369, Q370, Q371, Q372, Q373, Q374, Q375, Q376, Q377, Q378, Q379, Q380, Q381, Q382, Q383, Q384, Q385, Q386, Q387, Q388, Q389, Q390, Q391, Q392, Q393, Q394, Q395, Q396, Q397, Q398, Q399, Q400, Q401, Q402, Q403, Q404, Q405, Q406, Q407, Q408, Q409, Q410, Q411, Q412, Q413, Q414, Q415, Q416, Q417, Q418, Q419, Q420, Q421, Q422, Q423, Q424, Q425, Q426]), "oppositeDirection" : true, "depth" : .7 * mm, "offsetDistance" : 25 * mm});
        }
        {
            var Q0;
            Q0=makeQuery(id+"F5.boolean.opBoolean","INTERSECT",EDGE,{"derivedFrom":[makeQuery(id+"F1.opExtrude","SWEPT_FACE",FACE,{"disambiguationData":[OSD([sQuery(id+"F0.wireOp",EDGE,"E1.3")])]}),makeQuery(id+"F5.opExtrude","SWEPT_FACE",FACE,{"disambiguationData":[OSD([sQuery(id+"F4.wireOp",EDGE,"E3")])]})]});
            var Q1;
            Q1=makeQuery(id+"F5.boolean.opBoolean","COPY",EDGE,{"derivedFrom":makeQuery(id+"F5.opExtrude","SWEPT_EDGE",EDGE,{"disambiguationData":[OSD([sQuery(id+"F0.wireOp",EDGE,"E1.0"),sQuery(id+"F0.wireOp",EDGE,"E1.1"),sQuery(id+"F4.wireOp",EDGE,"E3")])]})});
            var Q2;
            Q2=makeQuery(id+"F5.boolean.opBoolean","COPY",EDGE,{"derivedFrom":makeQuery(id+"F5.opExtrude","CAP_EDGE",EDGE,{"disambiguationData":[OSD([sQuery(id+"F4.wireOp",EDGE,"E3")])],"isStart":true})});
            var Q3;
            Q3=makeQuery(id+"F5.boolean.opBoolean","COPY",EDGE,{"derivedFrom":makeQuery(id+"F5.opExtrude","SWEPT_EDGE",EDGE,{"disambiguationData":[OSD([sQuery(id+"F0.wireOp",EDGE,"E1.1"),sQuery(id+"F0.wireOp",EDGE,"E1.2"),sQuery(id+"F4.wireOp",EDGE,"E3")])]})});
            chamfer(context, id + "F18", {"entities" : qUnion([Q0, Q1, Q2, Q3]), "width" : 1 * mm, "tangentPropagation" : true});
        }
        {
            var Q0;
            Q0=makeQuery(id+"F7.opExtrude","CAP_EDGE",EDGE,{"disambiguationData":[OSD([sQuery(id+"F6.wireOp",EDGE,"E8.2")])],"isStart":true});
            var Q1;
            Q1=makeQuery(id+"F7.opExtrude","CAP_EDGE",EDGE,{"disambiguationData":[OSD([sQuery(id+"F6.wireOp",EDGE,"E8.0")])],"isStart":true});
            var Q2;
            {var subQ0=sQuery(id+"F6.wireOp",EDGE,"E8.3");var subQ1=sQuery(id+"F6.wireOp",EDGE,"E8.0");Q2=makeQuery(id+"F15.boolean.opBoolean","SPLIT",EDGE,{"disambiguationData":[TD([makeQuery(id+"F7.opExtrude","SWEPT_FACE",FACE,{"disambiguationData":[OSD([subQ1])]})])],"derivedFrom":makeQuery(id+"F7.opExtrude","CAP_EDGE",EDGE,{"disambiguationData":[OSD([subQ0])],"isStart":true})});}
            var Q3;
            {var subQ0=sQuery(id+"F6.wireOp",EDGE,"E8.3");var subQ1=sQuery(id+"F6.wireOp",EDGE,"E8.2");Q3=makeQuery(id+"F15.boolean.opBoolean","SPLIT",EDGE,{"disambiguationData":[TD([makeQuery(id+"F7.opExtrude","SWEPT_FACE",FACE,{"disambiguationData":[OSD([subQ1])]})])],"derivedFrom":makeQuery(id+"F7.opExtrude","CAP_EDGE",EDGE,{"disambiguationData":[OSD([subQ0])],"isStart":true})});}
            var Q4;
            {var subQ0=sQuery(id+"F6.wireOp",EDGE,"E8.2");var subQ1=sQuery(id+"F6.wireOp",EDGE,"E8.1");Q4=makeQuery(id+"F15.boolean.opBoolean","SPLIT",EDGE,{"disambiguationData":[TD([makeQuery(id+"F7.opExtrude","SWEPT_FACE",FACE,{"disambiguationData":[OSD([subQ0])]})])],"derivedFrom":makeQuery(id+"F7.opExtrude","CAP_EDGE",EDGE,{"disambiguationData":[OSD([subQ1])],"isStart":true})});}
            var Q5;
            {var subQ0=sQuery(id+"F6.wireOp",EDGE,"E8.1");var subQ1=sQuery(id+"F6.wireOp",EDGE,"E8.0");Q5=makeQuery(id+"F15.boolean.opBoolean","SPLIT",EDGE,{"disambiguationData":[TD([makeQuery(id+"F7.opExtrude","SWEPT_FACE",FACE,{"disambiguationData":[OSD([subQ1])]})])],"derivedFrom":makeQuery(id+"F7.opExtrude","CAP_EDGE",EDGE,{"disambiguationData":[OSD([subQ0])],"isStart":true})});}
            chamfer(context, id + "F19", {"entities" : qUnion([Q0, Q1, Q2, Q3, Q4, Q5]), "width" : 1 * mm, "tangentPropagation" : true});
        }
        {
            var Q0;
            Q0=makeQuery(id+"F7.opExtrude","SWEPT_FACE",FACE,{"disambiguationData":[OSD([sQuery(id+"F6.wireOp",EDGE,"E8.1")])]});
            var sketch = newSketch(context, id + "F20", { "sketchPlane" : qUnion([Q0])});
            skCircle(sketch, "E859", {"center": v(-8.23, 7) * mm, "radius": 3 * mm});
            skLineSegment(sketch, "E860", {"start": v(24.17, 101) * mm, "end": v(24.17, 10) * mm, "construction": true});
            skCircle(sketch, "E861.MirrorC", {"center": v(56.57, 7) * mm, "radius": 3 * mm});
            skSolve(sketch);
        }
        {
            var Q0;
            Q0=makeQuery(id+"F20.imprint","IMPRINT",FACE,{"disambiguationData":[TD([[makeQuery(id+"F20.imprint","IMPRINT",EDGE,{"derivedFrom":sQuery(id+"F20.wireOp",EDGE,"E861.MirrorC")}),-1.0]])]});
            var Q1;
            Q1=makeQuery(id+"F20.imprint","IMPRINT",FACE,{"disambiguationData":[TD([[makeQuery(id+"F20.imprint","IMPRINT",EDGE,{"derivedFrom":sQuery(id+"F20.wireOp",EDGE,"E859")}),1.0]])]});
            extrude(context, id + "F21", {"entities" : qUnion([Q0, Q1]), "operationType" : NewBodyOperationType.REMOVE, "oppositeDirection" : true, "depth" : 1.2 * mm, "offsetDistance" : 25 * mm});
        }
        {
            var Q0;
            Q0=makeQuery(id+"F7.opExtrude","SWEPT_FACE",FACE,{"disambiguationData":[OSD([sQuery(id+"F6.wireOp",EDGE,"E8.3")])]});
            var sketch = newSketch(context, id + "F22", { "sketchPlane" : qUnion([Q0])});
            skCircle(sketch, "E862.0", {"center": v(8.23, 7) * mm, "radius": 3 * mm});
            skCircle(sketch, "E863.0", {"center": v(-56.57, 7) * mm, "radius": 3 * mm});
            skSolve(sketch);
        }
        {
            var Q0;
            Q0=makeQuery(id+"F22.imprint","IMPRINT",FACE,{"disambiguationData":[TD([[makeQuery(id+"F22.imprint","IMPRINT",EDGE,{"derivedFrom":sQuery(id+"F22.wireOp",EDGE,"E862.0")}),-1.0]])]});
            var Q1;
            Q1=makeQuery(id+"F22.imprint","IMPRINT",FACE,{"disambiguationData":[TD([[makeQuery(id+"F22.imprint","IMPRINT",EDGE,{"derivedFrom":sQuery(id+"F22.wireOp",EDGE,"E863.0")}),1.0]])]});
            extrude(context, id + "F23", {"entities" : qUnion([Q0, Q1]), "operationType" : NewBodyOperationType.REMOVE, "oppositeDirection" : true, "depth" : 1.2 * mm, "offsetDistance" : 25 * mm});
        }
        {
            var Q0;
            Q0=makeQuery(id+"F20.imprint","IMPRINT",FACE,{"disambiguationData":[TD([[makeQuery(id+"F20.imprint","IMPRINT",EDGE,{"derivedFrom":sQuery(id+"F20.wireOp",EDGE,"E859")}),-1.0]])]});
            var sketch = newSketch(context, id + "F24", { "sketchPlane" : qUnion([Q0])});
            skCircle(sketch, "E864.0", {"center": v(56.57, 7) * mm, "radius": 3 * mm});
            skCircle(sketch, "E865.0", {"center": v(-8.23, 7) * mm, "radius": 3 * mm});
            skSolve(sketch);
        }
        {
            var Q0;
            Q0=makeQuery(id+"F24.imprint","IMPRINT",FACE,{"disambiguationData":[TD([[makeQuery(id+"F24.imprint","IMPRINT",EDGE,{"derivedFrom":sQuery(id+"F24.wireOp",EDGE,"E864.0")}),-1.0]])]});
            var Q1;
            Q1=makeQuery(id+"F20.imprint","IMPRINT",FACE,{"disambiguationData":[TD([[makeQuery(id+"F20.imprint","IMPRINT",EDGE,{"derivedFrom":sQuery(id+"F20.wireOp",EDGE,"E859")}),1.0]])]});
            extrude(context, id + "F25", {"entities" : qUnion([Q0, Q1]), "operationType" : NewBodyOperationType.REMOVE, "depth" : 1.2 * mm, "offsetDistance" : 25 * mm});
        }
        {
            var Q0;
            Q0=makeQuery(id+"F1.opExtrude","SWEPT_FACE",FACE,{"disambiguationData":[OSD([sQuery(id+"F0.wireOp",EDGE,"E1.3")])]});
            var sketch = newSketch(context, id + "F26", { "sketchPlane" : qUnion([Q0])});
            skCircle(sketch, "E866.0", {"center": v(56.57, 7) * mm, "radius": 3 * mm});
            skCircle(sketch, "E867.0", {"center": v(-8.23, 7) * mm, "radius": 3 * mm});
            skSolve(sketch);
        }
        {
            var Q0;
            Q0=makeQuery(id+"F26.imprint","IMPRINT",FACE,{"disambiguationData":[TD([[makeQuery(id+"F26.imprint","IMPRINT",EDGE,{"derivedFrom":sQuery(id+"F26.wireOp",EDGE,"E867.0")}),1.0]])]});
            var Q1;
            Q1=makeQuery(id+"F26.imprint","IMPRINT",FACE,{"disambiguationData":[TD([[makeQuery(id+"F26.imprint","IMPRINT",EDGE,{"derivedFrom":sQuery(id+"F26.wireOp",EDGE,"E866.0")}),1.0]])]});
            extrude(context, id + "F27", {"entities" : qUnion([Q0, Q1]), "operationType" : NewBodyOperationType.REMOVE, "oppositeDirection" : true, "depth" : 1.2 * mm, "offsetDistance" : 25 * mm});
        }
        {
            var Q0;
            Q0=makeQuery(id+"F13.boolean.opBoolean","COPY",EDGE,{"derivedFrom":makeQuery(id+"F13.opExtrude","CAP_EDGE",EDGE,{"disambiguationData":[OSD([sQuery(id+"F12.wireOp",EDGE,"E324")])],"isStart":false})});
            var Q1;
            Q1=makeQuery(id+"F13.boolean.opBoolean","COPY",EDGE,{"derivedFrom":makeQuery(id+"F13.opExtrude","CAP_EDGE",EDGE,{"disambiguationData":[OSD([sQuery(id+"F12.wireOp",EDGE,"E323")])],"isStart":false})});
            var Q2;
            Q2=makeQuery(id+"F13.boolean.opBoolean","COPY",EDGE,{"derivedFrom":makeQuery(id+"F13.opExtrude","CAP_EDGE",EDGE,{"disambiguationData":[OSD([sQuery(id+"F12.wireOp",EDGE,"E325")])],"isStart":false})});
            var Q3;
            Q3=makeQuery(id+"F13.boolean.opBoolean","COPY",EDGE,{"derivedFrom":makeQuery(id+"F13.opExtrude","CAP_EDGE",EDGE,{"disambiguationData":[OSD([sQuery(id+"F12.wireOp",EDGE,"E322")])],"isStart":false})});
            var Q4;
            Q4=makeQuery(id+"F13.boolean.opBoolean","COPY",EDGE,{"derivedFrom":makeQuery(id+"F13.opExtrude","CAP_EDGE",EDGE,{"disambiguationData":[OSD([sQuery(id+"F12.wireOp",EDGE,"E321")])],"isStart":false})});
            var Q5;
            Q5=makeQuery(id+"F13.boolean.opBoolean","COPY",EDGE,{"derivedFrom":makeQuery(id+"F13.opExtrude","CAP_EDGE",EDGE,{"disambiguationData":[OSD([sQuery(id+"F12.wireOp",EDGE,"E320")])],"isStart":false})});
            var Q6;
            Q6=makeQuery(id+"F13.boolean.opBoolean","COPY",EDGE,{"derivedFrom":makeQuery(id+"F13.opExtrude","CAP_EDGE",EDGE,{"disambiguationData":[OSD([sQuery(id+"F12.wireOp",EDGE,"E319")])],"isStart":false})});
            var Q7;
            Q7=makeQuery(id+"F13.boolean.opBoolean","COPY",EDGE,{"derivedFrom":makeQuery(id+"F13.opExtrude","CAP_EDGE",EDGE,{"disambiguationData":[OSD([sQuery(id+"F12.wireOp",EDGE,"E326")])],"isStart":false})});
            var Q8;
            Q8=makeQuery(id+"F13.boolean.opBoolean","COPY",EDGE,{"derivedFrom":makeQuery(id+"F13.opExtrude","CAP_EDGE",EDGE,{"disambiguationData":[OSD([sQuery(id+"F12.wireOp",EDGE,"E350")])],"isStart":false})});
            var Q9;
            Q9=makeQuery(id+"F13.boolean.opBoolean","COPY",EDGE,{"derivedFrom":makeQuery(id+"F13.opExtrude","CAP_EDGE",EDGE,{"disambiguationData":[OSD([sQuery(id+"F12.wireOp",EDGE,"E349")])],"isStart":false})});
            var Q10;
            Q10=makeQuery(id+"F13.boolean.opBoolean","COPY",EDGE,{"derivedFrom":makeQuery(id+"F13.opExtrude","CAP_EDGE",EDGE,{"disambiguationData":[OSD([sQuery(id+"F12.wireOp",EDGE,"E348")])],"isStart":false})});
            var Q11;
            Q11=makeQuery(id+"F13.boolean.opBoolean","COPY",EDGE,{"derivedFrom":makeQuery(id+"F13.opExtrude","CAP_EDGE",EDGE,{"disambiguationData":[OSD([sQuery(id+"F12.wireOp",EDGE,"E347")])],"isStart":false})});
            var Q12;
            Q12=makeQuery(id+"F13.boolean.opBoolean","COPY",EDGE,{"derivedFrom":makeQuery(id+"F13.opExtrude","CAP_EDGE",EDGE,{"disambiguationData":[OSD([sQuery(id+"F12.wireOp",EDGE,"E346")])],"isStart":false})});
            var Q13;
            Q13=makeQuery(id+"F13.boolean.opBoolean","COPY",EDGE,{"derivedFrom":makeQuery(id+"F13.opExtrude","CAP_EDGE",EDGE,{"disambiguationData":[OSD([sQuery(id+"F12.wireOp",EDGE,"E345")])],"isStart":false})});
            var Q14;
            Q14=makeQuery(id+"F13.boolean.opBoolean","COPY",EDGE,{"derivedFrom":makeQuery(id+"F13.opExtrude","CAP_EDGE",EDGE,{"disambiguationData":[OSD([sQuery(id+"F12.wireOp",EDGE,"E344")])],"isStart":false})});
            var Q15;
            Q15=makeQuery(id+"F13.boolean.opBoolean","COPY",EDGE,{"derivedFrom":makeQuery(id+"F13.opExtrude","CAP_EDGE",EDGE,{"disambiguationData":[OSD([sQuery(id+"F12.wireOp",EDGE,"E343")])],"isStart":false})});
            chamfer(context, id + "F28", {"entities" : qUnion([Q0, Q1, Q2, Q3, Q4, Q5, Q6, Q7, Q8, Q9, Q10, Q11, Q12, Q13, Q14, Q15]), "width" : .7 * mm, "tangentPropagation" : true});
        }
        {
            var Q0;
            Q0=makeQuery(id+"F13.boolean.opBoolean","COPY",EDGE,{"derivedFrom":makeQuery(id+"F13.opExtrude","CAP_EDGE",EDGE,{"disambiguationData":[OSD([sQuery(id+"F12.wireOp",EDGE,"E427")])],"isStart":false})});
            var Q1;
            Q1=makeQuery(id+"F13.boolean.opBoolean","COPY",EDGE,{"derivedFrom":makeQuery(id+"F13.opExtrude","CAP_EDGE",EDGE,{"disambiguationData":[OSD([sQuery(id+"F12.wireOp",EDGE,"E426")])],"isStart":false})});
            var Q2;
            Q2=makeQuery(id+"F13.boolean.opBoolean","COPY",EDGE,{"derivedFrom":makeQuery(id+"F13.opExtrude","CAP_EDGE",EDGE,{"disambiguationData":[OSD([sQuery(id+"F12.wireOp",EDGE,"E425")])],"isStart":false})});
            var Q3;
            Q3=makeQuery(id+"F13.boolean.opBoolean","COPY",EDGE,{"derivedFrom":makeQuery(id+"F13.opExtrude","CAP_EDGE",EDGE,{"disambiguationData":[OSD([sQuery(id+"F12.wireOp",EDGE,"E424")])],"isStart":false})});
            var Q4;
            Q4=makeQuery(id+"F13.boolean.opBoolean","COPY",EDGE,{"derivedFrom":makeQuery(id+"F13.opExtrude","CAP_EDGE",EDGE,{"disambiguationData":[OSD([sQuery(id+"F12.wireOp",EDGE,"E423")])],"isStart":false})});
            var Q5;
            Q5=makeQuery(id+"F13.boolean.opBoolean","COPY",EDGE,{"derivedFrom":makeQuery(id+"F13.opExtrude","CAP_EDGE",EDGE,{"disambiguationData":[OSD([sQuery(id+"F12.wireOp",EDGE,"E429")])],"isStart":false})});
            var Q6;
            Q6=makeQuery(id+"F13.boolean.opBoolean","COPY",EDGE,{"derivedFrom":makeQuery(id+"F13.opExtrude","CAP_EDGE",EDGE,{"disambiguationData":[OSD([sQuery(id+"F12.wireOp",EDGE,"E430")])],"isStart":false})});
            var Q7;
            Q7=makeQuery(id+"F13.boolean.opBoolean","COPY",EDGE,{"derivedFrom":makeQuery(id+"F13.opExtrude","CAP_EDGE",EDGE,{"disambiguationData":[OSD([sQuery(id+"F12.wireOp",EDGE,"E431")])],"isStart":false})});
            var Q8;
            Q8=makeQuery(id+"F13.boolean.opBoolean","COPY",EDGE,{"derivedFrom":makeQuery(id+"F13.opExtrude","CAP_EDGE",EDGE,{"disambiguationData":[OSD([sQuery(id+"F12.wireOp",EDGE,"E434")])],"isStart":false})});
            var Q9;
            Q9=makeQuery(id+"F13.boolean.opBoolean","COPY",EDGE,{"derivedFrom":makeQuery(id+"F13.opExtrude","CAP_EDGE",EDGE,{"disambiguationData":[OSD([sQuery(id+"F12.wireOp",EDGE,"E433")])],"isStart":false})});
            var Q10;
            Q10=makeQuery(id+"F13.boolean.opBoolean","COPY",EDGE,{"derivedFrom":makeQuery(id+"F13.opExtrude","CAP_EDGE",EDGE,{"disambiguationData":[OSD([sQuery(id+"F12.wireOp",EDGE,"E432")])],"isStart":false})});
            var Q11;
            Q11=makeQuery(id+"F13.boolean.opBoolean","COPY",EDGE,{"derivedFrom":makeQuery(id+"F13.opExtrude","CAP_EDGE",EDGE,{"disambiguationData":[OSD([sQuery(id+"F12.wireOp",EDGE,"E422")])],"isStart":false})});
            var Q12;
            Q12=makeQuery(id+"F13.boolean.opBoolean","COPY",EDGE,{"derivedFrom":makeQuery(id+"F13.opExtrude","CAP_EDGE",EDGE,{"disambiguationData":[OSD([sQuery(id+"F12.wireOp",EDGE,"E421")])],"isStart":false})});
            var Q13;
            Q13=makeQuery(id+"F13.boolean.opBoolean","COPY",EDGE,{"derivedFrom":makeQuery(id+"F13.opExtrude","CAP_EDGE",EDGE,{"disambiguationData":[OSD([sQuery(id+"F12.wireOp",EDGE,"E420")])],"isStart":false})});
            var Q14;
            Q14=makeQuery(id+"F13.boolean.opBoolean","COPY",EDGE,{"derivedFrom":makeQuery(id+"F13.opExtrude","CAP_EDGE",EDGE,{"disambiguationData":[OSD([sQuery(id+"F12.wireOp",EDGE,"E428")])],"isStart":false})});
            chamfer(context, id + "F29", {"entities" : qUnion([Q0, Q1, Q2, Q3, Q4, Q5, Q6, Q7, Q8, Q9, Q10, Q11, Q12, Q13, Q14]), "width" : .8 * mm, "tangentPropagation" : true});
        }
    });
